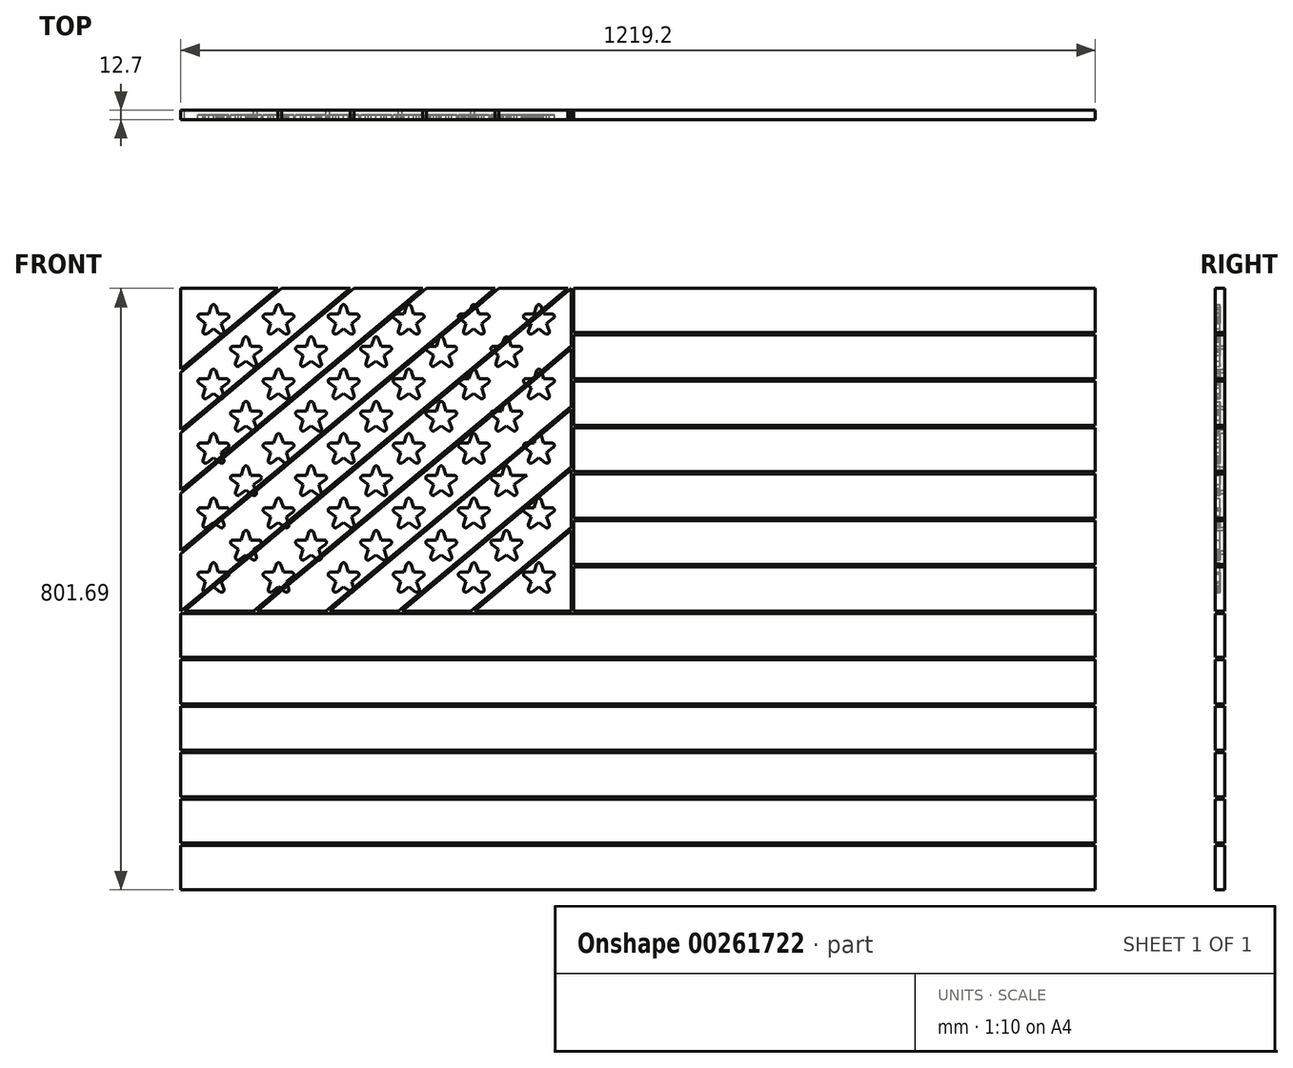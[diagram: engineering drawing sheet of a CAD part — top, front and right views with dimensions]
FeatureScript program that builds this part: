
annotation { "Feature Type Name" : "Feature", "Feature Type Description" : "" }
export const myFeature = defineFeature(function(context is Context, id is Id, definition is map)
    precondition{}
    {
        {
            var Q0;
            Q0=qCreatedBy(makeId("Front.planeOp"),FACE);
            var sketch = newSketch(context, id + "F0", { "sketchPlane" : qUnion([Q0])});
            skLineSegment(sketch, "E0.bottom", {"start": v(0, 0) * mm, "end": v(1219.2, 0) * mm});
            skLineSegment(sketch, "E0.top", {"start": v(0, 58.74) * mm, "end": v(1219.2, 58.74) * mm});
            skLineSegment(sketch, "E0.left", {"start": v(0, 0) * mm, "end": v(0, 58.74) * mm});
            skLineSegment(sketch, "E0.right", {"start": v(1219.2, 0) * mm, "end": v(1219.2, 58.74) * mm});
            skLineSegment(sketch, "E1.0.1.0", {"start": v(0, 120.65) * mm, "end": v(1219.2, 120.65) * mm});
            skLineSegment(sketch, "E1.0.1.1", {"start": v(0, 61.91) * mm, "end": v(1219.2, 61.91) * mm});
            skLineSegment(sketch, "E1.0.1.2", {"start": v(0, 61.91) * mm, "end": v(0, 120.65) * mm});
            skLineSegment(sketch, "E1.0.1.3", {"start": v(1219.2, 61.91) * mm, "end": v(1219.2, 120.65) * mm});
            skLineSegment(sketch, "E1.0.2.0", {"start": v(0, 182.56) * mm, "end": v(1219.2, 182.56) * mm});
            skLineSegment(sketch, "E1.0.2.1", {"start": v(0, 123.82) * mm, "end": v(1219.2, 123.82) * mm});
            skLineSegment(sketch, "E1.0.2.2", {"start": v(0, 123.82) * mm, "end": v(0, 182.56) * mm});
            skLineSegment(sketch, "E1.0.2.3", {"start": v(1219.2, 123.82) * mm, "end": v(1219.2, 182.56) * mm});
            skLineSegment(sketch, "E1.0.3.0", {"start": v(0, 244.47) * mm, "end": v(1219.2, 244.47) * mm});
            skLineSegment(sketch, "E1.0.3.1", {"start": v(0, 185.74) * mm, "end": v(1219.2, 185.74) * mm});
            skLineSegment(sketch, "E1.0.3.2", {"start": v(0, 185.74) * mm, "end": v(0, 244.47) * mm});
            skLineSegment(sketch, "E1.0.3.3", {"start": v(1219.2, 185.74) * mm, "end": v(1219.2, 244.47) * mm});
            skLineSegment(sketch, "E1.0.4.0", {"start": v(0, 306.39) * mm, "end": v(1219.2, 306.39) * mm});
            skLineSegment(sketch, "E1.0.4.1", {"start": v(0, 247.65) * mm, "end": v(1219.2, 247.65) * mm});
            skLineSegment(sketch, "E1.0.4.2", {"start": v(0, 247.65) * mm, "end": v(0, 306.39) * mm});
            skLineSegment(sketch, "E1.0.4.3", {"start": v(1219.2, 247.65) * mm, "end": v(1219.2, 306.39) * mm});
            skLineSegment(sketch, "E1.0.5.0", {"start": v(0, 368.3) * mm, "end": v(1219.2, 368.3) * mm});
            skLineSegment(sketch, "E1.0.5.1", {"start": v(0, 309.56) * mm, "end": v(1219.2, 309.56) * mm});
            skLineSegment(sketch, "E1.0.5.2", {"start": v(0, 309.56) * mm, "end": v(0, 368.3) * mm});
            skLineSegment(sketch, "E1.0.5.3", {"start": v(1219.2, 309.56) * mm, "end": v(1219.2, 368.3) * mm});
            skLineSegment(sketch, "E1.direction1", {"start": v(0, 0) * mm, "end": v(1219.2, 0) * mm, "construction": true});
            skLineSegment(sketch, "E1.direction2", {"start": v(0, 0) * mm, "end": v(0, 61.91) * mm, "construction": true});
            skLineSegment(sketch, "E2.bottom", {"start": v(523.88, 371.48) * mm, "end": v(1219.2, 371.48) * mm});
            skLineSegment(sketch, "E2.top", {"start": v(523.88, 430.21) * mm, "end": v(1219.2, 430.21) * mm});
            skLineSegment(sketch, "E2.left", {"start": v(523.88, 371.48) * mm, "end": v(523.88, 430.21) * mm});
            skLineSegment(sketch, "E2.right", {"start": v(1219.2, 371.48) * mm, "end": v(1219.2, 430.21) * mm});
            skLineSegment(sketch, "E3.0.1.0", {"start": v(523.88, 492.12) * mm, "end": v(1219.2, 492.12) * mm});
            skLineSegment(sketch, "E3.0.1.1", {"start": v(1219.2, 433.39) * mm, "end": v(1219.2, 492.12) * mm});
            skLineSegment(sketch, "E3.0.1.2", {"start": v(523.88, 433.39) * mm, "end": v(523.88, 492.12) * mm});
            skLineSegment(sketch, "E3.0.1.3", {"start": v(523.88, 433.39) * mm, "end": v(1219.2, 433.39) * mm});
            skLineSegment(sketch, "E3.0.2.0", {"start": v(523.88, 554.04) * mm, "end": v(1219.2, 554.04) * mm});
            skLineSegment(sketch, "E3.0.2.1", {"start": v(1219.2, 495.3) * mm, "end": v(1219.2, 554.04) * mm});
            skLineSegment(sketch, "E3.0.2.2", {"start": v(523.88, 495.3) * mm, "end": v(523.88, 554.04) * mm});
            skLineSegment(sketch, "E3.0.2.3", {"start": v(523.88, 495.3) * mm, "end": v(1219.2, 495.3) * mm});
            skLineSegment(sketch, "E3.0.3.0", {"start": v(523.88, 615.95) * mm, "end": v(1219.2, 615.95) * mm});
            skLineSegment(sketch, "E3.0.3.1", {"start": v(1219.2, 557.21) * mm, "end": v(1219.2, 615.95) * mm});
            skLineSegment(sketch, "E3.0.3.2", {"start": v(523.88, 557.21) * mm, "end": v(523.88, 615.95) * mm});
            skLineSegment(sketch, "E3.0.3.3", {"start": v(523.88, 557.21) * mm, "end": v(1219.2, 557.21) * mm});
            skLineSegment(sketch, "E3.0.4.0", {"start": v(523.88, 677.86) * mm, "end": v(1219.2, 677.86) * mm});
            skLineSegment(sketch, "E3.0.4.1", {"start": v(1219.2, 619.12) * mm, "end": v(1219.2, 677.86) * mm});
            skLineSegment(sketch, "E3.0.4.2", {"start": v(523.88, 619.12) * mm, "end": v(523.88, 677.86) * mm});
            skLineSegment(sketch, "E3.0.4.3", {"start": v(523.88, 619.12) * mm, "end": v(1219.2, 619.12) * mm});
            skLineSegment(sketch, "E3.0.5.0", {"start": v(523.88, 739.77) * mm, "end": v(1219.2, 739.77) * mm});
            skLineSegment(sketch, "E3.0.5.1", {"start": v(1219.2, 681.04) * mm, "end": v(1219.2, 739.77) * mm});
            skLineSegment(sketch, "E3.0.5.2", {"start": v(523.88, 681.04) * mm, "end": v(523.88, 739.77) * mm});
            skLineSegment(sketch, "E3.0.5.3", {"start": v(523.88, 681.04) * mm, "end": v(1219.2, 681.04) * mm});
            skLineSegment(sketch, "E3.0.6.0", {"start": v(523.88, 801.69) * mm, "end": v(1219.2, 801.69) * mm});
            skLineSegment(sketch, "E3.0.6.1", {"start": v(1219.2, 742.95) * mm, "end": v(1219.2, 801.69) * mm});
            skLineSegment(sketch, "E3.0.6.2", {"start": v(523.88, 742.95) * mm, "end": v(523.88, 801.69) * mm});
            skLineSegment(sketch, "E3.0.6.3", {"start": v(523.88, 742.95) * mm, "end": v(1219.2, 742.95) * mm});
            skLineSegment(sketch, "E3.direction1", {"start": v(523.88, 371.48) * mm, "end": v(1219.2, 371.48) * mm, "construction": true});
            skLineSegment(sketch, "E3.direction2", {"start": v(523.88, 371.48) * mm, "end": v(523.88, 433.39) * mm, "construction": true});
            skLineSegment(sketch, "E4", {"start": v(520.7, 801.69) * mm, "end": v(4.96, 371.47) * mm});
            skLineSegment(sketch, "E5", {"start": v(520.7, 725.2) * mm, "end": v(96.65, 371.47) * mm});
            skLineSegment(sketch, "E6", {"start": v(520.7, 721.06) * mm, "end": v(101.61, 371.47) * mm});
            skLineSegment(sketch, "E7", {"start": v(193.3, 371.47) * mm, "end": v(520.7, 644.57) * mm});
            skLineSegment(sketch, "E8", {"start": v(520.7, 640.44) * mm, "end": v(198.26, 371.47) * mm});
            skLineSegment(sketch, "E9", {"start": v(520.7, 563.95) * mm, "end": v(289.96, 371.47) * mm});
            skLineSegment(sketch, "E10", {"start": v(520.7, 483.32) * mm, "end": v(386.62, 371.48) * mm});
            skLineSegment(sketch, "E11", {"start": v(520.7, 559.81) * mm, "end": v(294.92, 371.47) * mm});
            skLineSegment(sketch, "E12", {"start": v(520.7, 479.19) * mm, "end": v(391.57, 371.47) * mm});
            skLineSegment(sketch, "E13", {"start": v(520.7, 801.69) * mm, "end": v(520.7, 725.2) * mm});
            skLineSegment(sketch, "E14", {"start": v(520.7, 721.06) * mm, "end": v(520.7, 644.57) * mm});
            skLineSegment(sketch, "E15", {"start": v(520.7, 640.44) * mm, "end": v(520.7, 563.95) * mm});
            skLineSegment(sketch, "E16", {"start": v(520.7, 559.81) * mm, "end": v(520.7, 483.32) * mm});
            skLineSegment(sketch, "E17", {"start": v(520.7, 479.19) * mm, "end": v(520.7, 371.48) * mm});
            skLineSegment(sketch, "E18", {"start": v(4.96, 371.47) * mm, "end": v(96.65, 371.47) * mm});
            skLineSegment(sketch, "E19", {"start": v(193.3, 371.47) * mm, "end": v(101.61, 371.47) * mm});
            skLineSegment(sketch, "E20", {"start": v(198.26, 371.47) * mm, "end": v(289.96, 371.47) * mm});
            skLineSegment(sketch, "E21", {"start": v(294.92, 371.47) * mm, "end": v(386.62, 371.47) * mm});
            skLineSegment(sketch, "E22", {"start": v(391.57, 371.47) * mm, "end": v(520.7, 371.48) * mm});
            skLineSegment(sketch, "E23", {"start": v(515.74, 801.69) * mm, "end": v(0, 371.47) * mm});
            skLineSegment(sketch, "E24", {"start": v(424.05, 801.69) * mm, "end": v(0, 447.97) * mm});
            skLineSegment(sketch, "E25", {"start": v(0, 452.1) * mm, "end": v(419.09, 801.69) * mm});
            skLineSegment(sketch, "E26", {"start": v(0, 528.59) * mm, "end": v(327.4, 801.69) * mm});
            skLineSegment(sketch, "E27", {"start": v(322.44, 801.69) * mm, "end": v(0, 532.72) * mm});
            skLineSegment(sketch, "E28", {"start": v(0, 609.21) * mm, "end": v(230.74, 801.69) * mm});
            skLineSegment(sketch, "E29", {"start": v(225.78, 801.69) * mm, "end": v(0, 613.35) * mm});
            skLineSegment(sketch, "E30", {"start": v(134.08, 801.69) * mm, "end": v(0, 689.84) * mm});
            skLineSegment(sketch, "E31", {"start": v(129.13, 801.69) * mm, "end": v(0, 693.97) * mm});
            skLineSegment(sketch, "E32", {"start": v(0, 447.97) * mm, "end": v(0, 371.47) * mm});
            skLineSegment(sketch, "E33", {"start": v(0, 528.59) * mm, "end": v(0, 452.1) * mm});
            skLineSegment(sketch, "E34", {"start": v(0, 532.72) * mm, "end": v(0, 609.21) * mm});
            skLineSegment(sketch, "E35", {"start": v(0, 613.35) * mm, "end": v(0, 689.84) * mm});
            skLineSegment(sketch, "E36", {"start": v(0, 693.97) * mm, "end": v(0, 801.69) * mm});
            skLineSegment(sketch, "E37", {"start": v(515.74, 801.69) * mm, "end": v(424.05, 801.69) * mm});
            skLineSegment(sketch, "E38", {"start": v(419.09, 801.69) * mm, "end": v(327.4, 801.69) * mm});
            skLineSegment(sketch, "E39", {"start": v(322.44, 801.69) * mm, "end": v(230.74, 801.69) * mm});
            skLineSegment(sketch, "E40", {"start": v(225.78, 801.69) * mm, "end": v(134.08, 801.69) * mm});
            skLineSegment(sketch, "E41", {"start": v(129.13, 801.69) * mm, "end": v(0, 801.69) * mm});
            skSolve(sketch);
        }
        {
            var Q0;
            Q0=qCreatedBy(makeId("Front.planeOp"),FACE);
            var sketch = newSketch(context, id + "F1", { "sketchPlane" : qUnion([Q0])});
            skLineSegment(sketch, "E42", {"start": v(43.4, 801.69) * mm, "end": v(43.4, 371.47) * mm, "construction": true});
            skLineSegment(sketch, "E43", {"start": v(520.7, 801.69) * mm, "end": v(0, 801.69) * mm, "construction": true});
            skLineSegment(sketch, "E44", {"start": v(0, 801.69) * mm, "end": v(0, 371.47) * mm, "construction": true});
            skLineSegment(sketch, "E45", {"start": v(0, 371.47) * mm, "end": v(520.7, 371.47) * mm, "construction": true});
            skLineSegment(sketch, "E46", {"start": v(520.7, 371.48) * mm, "end": v(520.7, 801.69) * mm, "construction": true});
            skLineSegment(sketch, "E47", {"start": v(0, 414.5) * mm, "end": v(520.7, 414.5) * mm, "construction": true});
            skLineSegment(sketch, "E48.1.0.0", {"start": v(86.78, 801.69) * mm, "end": v(86.78, 371.47) * mm, "construction": true});
            skLineSegment(sketch, "E48.2.0.0", {"start": v(130.17, 801.69) * mm, "end": v(130.17, 371.47) * mm, "construction": true});
            skLineSegment(sketch, "E48.3.0.0", {"start": v(173.56, 801.69) * mm, "end": v(173.56, 371.47) * mm, "construction": true});
            skLineSegment(sketch, "E48.4.0.0", {"start": v(216.95, 801.69) * mm, "end": v(216.95, 371.47) * mm, "construction": true});
            skLineSegment(sketch, "E48.5.0.0", {"start": v(260.34, 801.69) * mm, "end": v(260.34, 371.47) * mm, "construction": true});
            skLineSegment(sketch, "E48.6.0.0", {"start": v(303.74, 801.69) * mm, "end": v(303.74, 371.47) * mm, "construction": true});
            skLineSegment(sketch, "E48.7.0.0", {"start": v(347.13, 801.69) * mm, "end": v(347.13, 371.47) * mm, "construction": true});
            skLineSegment(sketch, "E48.8.0.0", {"start": v(390.52, 801.69) * mm, "end": v(390.52, 371.47) * mm, "construction": true});
            skLineSegment(sketch, "E48.9.0.0", {"start": v(433.9, 801.69) * mm, "end": v(433.9, 371.47) * mm, "construction": true});
            skLineSegment(sketch, "E48.10.0.0", {"start": v(477.3, 801.69) * mm, "end": v(477.3, 371.47) * mm, "construction": true});
            skLineSegment(sketch, "E48.direction1", {"start": v(43.4, 371.47) * mm, "end": v(86.78, 371.47) * mm, "construction": true});
            skLineSegment(sketch, "E49", {"start": v(43.4, 371.47) * mm, "end": v(0, 371.47) * mm, "construction": true});
            skLineSegment(sketch, "E50", {"start": v(0, 414.5) * mm, "end": v(0, 371.47) * mm, "construction": true});
            skLineSegment(sketch, "E51.0.1.0", {"start": v(0, 457.51) * mm, "end": v(520.7, 457.51) * mm, "construction": true});
            skLineSegment(sketch, "E51.0.2.0", {"start": v(0, 500.53) * mm, "end": v(520.7, 500.53) * mm, "construction": true});
            skLineSegment(sketch, "E51.0.3.0", {"start": v(0, 543.55) * mm, "end": v(520.7, 543.55) * mm, "construction": true});
            skLineSegment(sketch, "E51.0.4.0", {"start": v(0, 586.57) * mm, "end": v(520.7, 586.57) * mm, "construction": true});
            skLineSegment(sketch, "E51.0.5.0", {"start": v(0, 629.6) * mm, "end": v(520.7, 629.6) * mm, "construction": true});
            skLineSegment(sketch, "E51.0.6.0", {"start": v(0, 672.61) * mm, "end": v(520.7, 672.61) * mm, "construction": true});
            skLineSegment(sketch, "E51.0.7.0", {"start": v(0, 715.63) * mm, "end": v(520.7, 715.63) * mm, "construction": true});
            skLineSegment(sketch, "E51.0.8.0", {"start": v(0, 758.65) * mm, "end": v(520.7, 758.65) * mm, "construction": true});
            skLineSegment(sketch, "E51.direction2", {"start": v(0, 414.5) * mm, "end": v(0, 457.51) * mm, "construction": true});
            skPoint(sketch, "E52", {"position": v(43.4, 758.65) * mm});
            skPoint(sketch, "E53", {"position": v(130.17, 758.65) * mm});
            skPoint(sketch, "E54", {"position": v(216.95, 758.65) * mm});
            skPoint(sketch, "E55", {"position": v(303.74, 758.65) * mm});
            skPoint(sketch, "E56", {"position": v(390.52, 758.65) * mm});
            skPoint(sketch, "E57", {"position": v(477.3, 758.65) * mm});
            skPoint(sketch, "E58", {"position": v(86.78, 715.63) * mm});
            skPoint(sketch, "E59", {"position": v(173.56, 715.63) * mm});
            skPoint(sketch, "E60", {"position": v(260.34, 715.63) * mm});
            skPoint(sketch, "E61", {"position": v(347.13, 715.63) * mm});
            skPoint(sketch, "E62", {"position": v(433.9, 715.63) * mm});
            skPoint(sketch, "E63", {"position": v(477.3, 672.61) * mm});
            skPoint(sketch, "E64", {"position": v(390.52, 672.61) * mm});
            skPoint(sketch, "E65", {"position": v(303.74, 672.61) * mm});
            skPoint(sketch, "E66", {"position": v(216.95, 672.61) * mm});
            skPoint(sketch, "E67", {"position": v(130.17, 672.61) * mm});
            skPoint(sketch, "E68", {"position": v(43.4, 672.61) * mm});
            skPoint(sketch, "E69", {"position": v(86.78, 629.6) * mm});
            skPoint(sketch, "E70", {"position": v(173.56, 629.6) * mm});
            skPoint(sketch, "E71", {"position": v(260.34, 629.6) * mm});
            skPoint(sketch, "E72", {"position": v(347.13, 629.6) * mm});
            skPoint(sketch, "E73", {"position": v(433.9, 629.6) * mm});
            skPoint(sketch, "E74", {"position": v(130.17, 586.57) * mm});
            skPoint(sketch, "E75", {"position": v(216.95, 586.57) * mm});
            skPoint(sketch, "E76", {"position": v(303.74, 586.57) * mm});
            skPoint(sketch, "E77", {"position": v(390.52, 586.57) * mm});
            skPoint(sketch, "E78", {"position": v(433.9, 543.55) * mm});
            skPoint(sketch, "E79", {"position": v(260.34, 543.55) * mm});
            skPoint(sketch, "E80", {"position": v(173.56, 543.55) * mm});
            skPoint(sketch, "E81", {"position": v(130.17, 500.53) * mm});
            skPoint(sketch, "E82", {"position": v(216.95, 500.53) * mm});
            skPoint(sketch, "E83", {"position": v(390.52, 500.53) * mm});
            skPoint(sketch, "E84", {"position": v(477.3, 500.53) * mm});
            skPoint(sketch, "E85", {"position": v(433.9, 457.51) * mm});
            skPoint(sketch, "E86", {"position": v(347.13, 457.51) * mm});
            skPoint(sketch, "E87", {"position": v(173.56, 457.51) * mm});
            skPoint(sketch, "E88", {"position": v(86.78, 457.51) * mm});
            skPoint(sketch, "E89", {"position": v(130.17, 414.5) * mm});
            skPoint(sketch, "E90", {"position": v(216.95, 414.5) * mm});
            skPoint(sketch, "E91", {"position": v(303.74, 414.5) * mm});
            skPoint(sketch, "E92", {"position": v(477.3, 414.5) * mm});
            skCircle(sketch, "E93", {"center": v(0, 845.78) * mm, "radius": 28.58 * mm, "construction": true});
            skLineSegment(sketch, "E94", {"start": v(-27.18, 854.61) * mm, "end": v(-6.42, 854.61) * mm, "construction": true});
            skLineSegment(sketch, "E95", {"start": v(27.18, 854.61) * mm, "end": v(10.38, 842.4) * mm, "construction": true});
            skLineSegment(sketch, "E96", {"start": v(-6.42, 854.61) * mm, "end": v(0, 874.36) * mm, "construction": true});
            skLineSegment(sketch, "E97", {"start": v(0, 874.36) * mm, "end": v(6.42, 854.61) * mm, "construction": true});
            skLineSegment(sketch, "E98", {"start": v(16.8, 822.66) * mm, "end": v(0, 834.87) * mm, "construction": true});
            skLineSegment(sketch, "E99", {"start": v(-16.8, 822.66) * mm, "end": v(0, 834.87) * mm, "construction": true});
            skLineSegment(sketch, "E100", {"start": v(-27.18, 854.61) * mm, "end": v(-10.38, 842.4) * mm, "construction": true});
            skLineSegment(sketch, "E101", {"start": v(-10.38, 842.4) * mm, "end": v(-16.8, 822.66) * mm, "construction": true});
            skLineSegment(sketch, "E102", {"start": v(16.8, 822.66) * mm, "end": v(10.38, 842.4) * mm, "construction": true});
            skLineSegment(sketch, "E103", {"start": v(27.18, 854.61) * mm, "end": v(6.42, 854.61) * mm, "construction": true});
            skCircle(sketch, "E104", {"center": v(43.4, 758.65) * mm, "radius": 28.58 * mm, "construction": true});
            skLineSegment(sketch, "E105", {"start": v(16.21, 767.48) * mm, "end": v(36.98, 767.48) * mm});
            skLineSegment(sketch, "E106", {"start": v(70.57, 767.48) * mm, "end": v(53.77, 755.28) * mm});
            skLineSegment(sketch, "E107", {"start": v(36.98, 767.48) * mm, "end": v(43.4, 787.23) * mm});
            skLineSegment(sketch, "E108", {"start": v(43.4, 787.23) * mm, "end": v(49.8, 767.48) * mm});
            skLineSegment(sketch, "E109", {"start": v(60.19, 735.54) * mm, "end": v(43.4, 747.74) * mm});
            skLineSegment(sketch, "E110", {"start": v(26.6, 735.54) * mm, "end": v(43.4, 747.74) * mm});
            skLineSegment(sketch, "E111", {"start": v(16.21, 767.48) * mm, "end": v(33.01, 755.28) * mm});
            skLineSegment(sketch, "E112", {"start": v(33.01, 755.28) * mm, "end": v(26.6, 735.54) * mm});
            skLineSegment(sketch, "E113", {"start": v(60.19, 735.54) * mm, "end": v(53.77, 755.28) * mm});
            skLineSegment(sketch, "E114", {"start": v(70.57, 767.48) * mm, "end": v(49.8, 767.48) * mm});
            skCircle(sketch, "E115", {"center": v(477.3, 586.57) * mm, "radius": 28.58 * mm, "construction": true});
            skLineSegment(sketch, "E116", {"start": v(450.12, 595.4) * mm, "end": v(470.88, 595.4) * mm});
            skLineSegment(sketch, "E117", {"start": v(504.48, 595.4) * mm, "end": v(487.68, 583.2) * mm});
            skLineSegment(sketch, "E118", {"start": v(470.88, 595.4) * mm, "end": v(477.3, 615.15) * mm});
            skLineSegment(sketch, "E119", {"start": v(477.3, 615.15) * mm, "end": v(483.71, 595.4) * mm});
            skLineSegment(sketch, "E120", {"start": v(494.1, 563.46) * mm, "end": v(477.3, 575.66) * mm});
            skLineSegment(sketch, "E121", {"start": v(460.5, 563.46) * mm, "end": v(477.3, 575.66) * mm});
            skLineSegment(sketch, "E122", {"start": v(450.12, 595.4) * mm, "end": v(466.92, 583.2) * mm});
            skLineSegment(sketch, "E123", {"start": v(466.92, 583.2) * mm, "end": v(460.5, 563.46) * mm});
            skLineSegment(sketch, "E124", {"start": v(494.1, 563.46) * mm, "end": v(487.68, 583.2) * mm});
            skLineSegment(sketch, "E125", {"start": v(504.48, 595.4) * mm, "end": v(483.71, 595.4) * mm});
            skCircle(sketch, "E126", {"center": v(390.52, 758.65) * mm, "radius": 28.58 * mm, "construction": true});
            skLineSegment(sketch, "E127", {"start": v(363.34, 767.48) * mm, "end": v(384.1, 767.48) * mm});
            skLineSegment(sketch, "E128", {"start": v(417.7, 767.48) * mm, "end": v(400.9, 755.28) * mm});
            skLineSegment(sketch, "E129", {"start": v(384.1, 767.48) * mm, "end": v(390.52, 787.23) * mm});
            skLineSegment(sketch, "E130", {"start": v(390.52, 787.23) * mm, "end": v(396.93, 767.48) * mm});
            skLineSegment(sketch, "E131", {"start": v(407.31, 735.54) * mm, "end": v(390.52, 747.74) * mm});
            skLineSegment(sketch, "E132", {"start": v(373.72, 735.54) * mm, "end": v(390.52, 747.74) * mm});
            skLineSegment(sketch, "E133", {"start": v(363.34, 767.48) * mm, "end": v(380.14, 755.28) * mm});
            skLineSegment(sketch, "E134", {"start": v(380.14, 755.28) * mm, "end": v(373.72, 735.54) * mm});
            skLineSegment(sketch, "E135", {"start": v(407.31, 735.54) * mm, "end": v(400.9, 755.28) * mm});
            skLineSegment(sketch, "E136", {"start": v(417.7, 767.48) * mm, "end": v(396.93, 767.48) * mm});
            skCircle(sketch, "E137", {"center": v(303.74, 758.65) * mm, "radius": 28.58 * mm, "construction": true});
            skLineSegment(sketch, "E138", {"start": v(276.56, 767.48) * mm, "end": v(297.32, 767.48) * mm});
            skLineSegment(sketch, "E139", {"start": v(330.91, 767.48) * mm, "end": v(314.12, 755.28) * mm});
            skLineSegment(sketch, "E140", {"start": v(297.32, 767.48) * mm, "end": v(303.74, 787.23) * mm});
            skLineSegment(sketch, "E141", {"start": v(303.74, 787.23) * mm, "end": v(310.15, 767.48) * mm});
            skLineSegment(sketch, "E142", {"start": v(320.53, 735.54) * mm, "end": v(303.74, 747.74) * mm});
            skLineSegment(sketch, "E143", {"start": v(286.94, 735.54) * mm, "end": v(303.74, 747.74) * mm});
            skLineSegment(sketch, "E144", {"start": v(276.56, 767.48) * mm, "end": v(293.36, 755.28) * mm});
            skLineSegment(sketch, "E145", {"start": v(293.36, 755.28) * mm, "end": v(286.94, 735.54) * mm});
            skLineSegment(sketch, "E146", {"start": v(320.53, 735.54) * mm, "end": v(314.12, 755.28) * mm});
            skLineSegment(sketch, "E147", {"start": v(330.91, 767.48) * mm, "end": v(310.15, 767.48) * mm});
            skCircle(sketch, "E148", {"center": v(216.95, 758.65) * mm, "radius": 28.58 * mm, "construction": true});
            skLineSegment(sketch, "E149", {"start": v(189.78, 767.48) * mm, "end": v(210.54, 767.48) * mm});
            skLineSegment(sketch, "E150", {"start": v(244.13, 767.48) * mm, "end": v(227.33, 755.28) * mm});
            skLineSegment(sketch, "E151", {"start": v(210.54, 767.48) * mm, "end": v(216.95, 787.23) * mm});
            skLineSegment(sketch, "E152", {"start": v(216.95, 787.23) * mm, "end": v(223.37, 767.48) * mm});
            skLineSegment(sketch, "E153", {"start": v(233.75, 735.54) * mm, "end": v(216.95, 747.74) * mm});
            skLineSegment(sketch, "E154", {"start": v(200.16, 735.54) * mm, "end": v(216.95, 747.74) * mm});
            skLineSegment(sketch, "E155", {"start": v(189.78, 767.48) * mm, "end": v(206.57, 755.28) * mm});
            skLineSegment(sketch, "E156", {"start": v(206.57, 755.28) * mm, "end": v(200.16, 735.54) * mm});
            skLineSegment(sketch, "E157", {"start": v(233.75, 735.54) * mm, "end": v(227.33, 755.28) * mm});
            skLineSegment(sketch, "E158", {"start": v(244.13, 767.48) * mm, "end": v(223.37, 767.48) * mm});
            skCircle(sketch, "E159", {"center": v(130.17, 758.65) * mm, "radius": 28.58 * mm, "construction": true});
            skLineSegment(sketch, "E160", {"start": v(103, 767.48) * mm, "end": v(123.76, 767.48) * mm});
            skLineSegment(sketch, "E161", {"start": v(157.35, 767.48) * mm, "end": v(140.55, 755.28) * mm});
            skLineSegment(sketch, "E162", {"start": v(123.76, 767.48) * mm, "end": v(130.17, 787.23) * mm});
            skLineSegment(sketch, "E163", {"start": v(130.17, 787.23) * mm, "end": v(136.59, 767.48) * mm});
            skLineSegment(sketch, "E164", {"start": v(146.97, 735.54) * mm, "end": v(130.17, 747.74) * mm});
            skLineSegment(sketch, "E165", {"start": v(113.38, 735.54) * mm, "end": v(130.17, 747.74) * mm});
            skLineSegment(sketch, "E166", {"start": v(103, 767.48) * mm, "end": v(119.8, 755.28) * mm});
            skLineSegment(sketch, "E167", {"start": v(119.8, 755.28) * mm, "end": v(113.38, 735.54) * mm});
            skLineSegment(sketch, "E168", {"start": v(146.97, 735.54) * mm, "end": v(140.55, 755.28) * mm});
            skLineSegment(sketch, "E169", {"start": v(157.35, 767.48) * mm, "end": v(136.59, 767.48) * mm});
            skCircle(sketch, "E170", {"center": v(477.3, 758.65) * mm, "radius": 28.58 * mm, "construction": true});
            skLineSegment(sketch, "E171", {"start": v(450.12, 767.48) * mm, "end": v(470.88, 767.48) * mm});
            skLineSegment(sketch, "E172", {"start": v(504.48, 767.48) * mm, "end": v(487.68, 755.28) * mm});
            skLineSegment(sketch, "E173", {"start": v(470.88, 767.48) * mm, "end": v(477.3, 787.23) * mm});
            skLineSegment(sketch, "E174", {"start": v(477.3, 787.23) * mm, "end": v(483.71, 767.48) * mm});
            skLineSegment(sketch, "E175", {"start": v(494.1, 735.54) * mm, "end": v(477.3, 747.74) * mm});
            skLineSegment(sketch, "E176", {"start": v(460.5, 735.54) * mm, "end": v(477.3, 747.74) * mm});
            skLineSegment(sketch, "E177", {"start": v(450.12, 767.48) * mm, "end": v(466.92, 755.28) * mm});
            skLineSegment(sketch, "E178", {"start": v(466.92, 755.28) * mm, "end": v(460.5, 735.54) * mm});
            skLineSegment(sketch, "E179", {"start": v(494.1, 735.54) * mm, "end": v(487.68, 755.28) * mm});
            skLineSegment(sketch, "E180", {"start": v(504.48, 767.48) * mm, "end": v(483.71, 767.48) * mm});
            skCircle(sketch, "E181", {"center": v(347.13, 715.63) * mm, "radius": 28.58 * mm, "construction": true});
            skLineSegment(sketch, "E182", {"start": v(319.95, 724.47) * mm, "end": v(340.71, 724.47) * mm});
            skLineSegment(sketch, "E183", {"start": v(374.3, 724.47) * mm, "end": v(357.5, 712.26) * mm});
            skLineSegment(sketch, "E184", {"start": v(340.71, 724.47) * mm, "end": v(347.13, 744.2) * mm});
            skLineSegment(sketch, "E185", {"start": v(347.13, 744.2) * mm, "end": v(353.54, 724.47) * mm});
            skLineSegment(sketch, "E186", {"start": v(363.92, 692.52) * mm, "end": v(347.13, 704.72) * mm});
            skLineSegment(sketch, "E187", {"start": v(330.33, 692.52) * mm, "end": v(347.13, 704.72) * mm});
            skLineSegment(sketch, "E188", {"start": v(319.95, 724.47) * mm, "end": v(336.75, 712.26) * mm});
            skLineSegment(sketch, "E189", {"start": v(336.75, 712.26) * mm, "end": v(330.33, 692.52) * mm});
            skLineSegment(sketch, "E190", {"start": v(363.92, 692.52) * mm, "end": v(357.5, 712.26) * mm});
            skLineSegment(sketch, "E191", {"start": v(374.3, 724.47) * mm, "end": v(353.54, 724.47) * mm});
            skCircle(sketch, "E192", {"center": v(260.34, 715.63) * mm, "radius": 28.58 * mm, "construction": true});
            skLineSegment(sketch, "E193", {"start": v(233.17, 724.47) * mm, "end": v(253.93, 724.47) * mm});
            skLineSegment(sketch, "E194", {"start": v(287.52, 724.47) * mm, "end": v(270.73, 712.26) * mm});
            skLineSegment(sketch, "E195", {"start": v(253.93, 724.47) * mm, "end": v(260.34, 744.2) * mm});
            skLineSegment(sketch, "E196", {"start": v(260.34, 744.2) * mm, "end": v(266.76, 724.47) * mm});
            skLineSegment(sketch, "E197", {"start": v(277.14, 692.52) * mm, "end": v(260.34, 704.72) * mm});
            skLineSegment(sketch, "E198", {"start": v(243.55, 692.52) * mm, "end": v(260.34, 704.72) * mm});
            skLineSegment(sketch, "E199", {"start": v(233.17, 724.47) * mm, "end": v(249.96, 712.26) * mm});
            skLineSegment(sketch, "E200", {"start": v(249.96, 712.26) * mm, "end": v(243.55, 692.52) * mm});
            skLineSegment(sketch, "E201", {"start": v(277.14, 692.52) * mm, "end": v(270.73, 712.26) * mm});
            skLineSegment(sketch, "E202", {"start": v(287.52, 724.47) * mm, "end": v(266.76, 724.47) * mm});
            skCircle(sketch, "E203", {"center": v(173.56, 715.63) * mm, "radius": 28.58 * mm, "construction": true});
            skLineSegment(sketch, "E204", {"start": v(146.39, 724.47) * mm, "end": v(167.15, 724.47) * mm});
            skLineSegment(sketch, "E205", {"start": v(200.74, 724.47) * mm, "end": v(183.94, 712.26) * mm});
            skLineSegment(sketch, "E206", {"start": v(167.15, 724.47) * mm, "end": v(173.56, 744.2) * mm});
            skLineSegment(sketch, "E207", {"start": v(173.56, 744.2) * mm, "end": v(179.98, 724.47) * mm});
            skLineSegment(sketch, "E208", {"start": v(190.36, 692.52) * mm, "end": v(173.56, 704.72) * mm});
            skLineSegment(sketch, "E209", {"start": v(156.77, 692.52) * mm, "end": v(173.56, 704.72) * mm});
            skLineSegment(sketch, "E210", {"start": v(146.39, 724.47) * mm, "end": v(163.18, 712.26) * mm});
            skLineSegment(sketch, "E211", {"start": v(163.18, 712.26) * mm, "end": v(156.77, 692.52) * mm});
            skLineSegment(sketch, "E212", {"start": v(190.36, 692.52) * mm, "end": v(183.94, 712.26) * mm});
            skLineSegment(sketch, "E213", {"start": v(200.74, 724.47) * mm, "end": v(179.98, 724.47) * mm});
            skCircle(sketch, "E214", {"center": v(86.78, 715.63) * mm, "radius": 28.58 * mm, "construction": true});
            skLineSegment(sketch, "E215", {"start": v(59.6, 724.47) * mm, "end": v(80.37, 724.47) * mm});
            skLineSegment(sketch, "E216", {"start": v(113.96, 724.47) * mm, "end": v(97.16, 712.26) * mm});
            skLineSegment(sketch, "E217", {"start": v(80.37, 724.47) * mm, "end": v(86.78, 744.2) * mm});
            skLineSegment(sketch, "E218", {"start": v(86.78, 744.2) * mm, "end": v(93.2, 724.47) * mm});
            skLineSegment(sketch, "E219", {"start": v(103.58, 692.52) * mm, "end": v(86.78, 704.72) * mm});
            skLineSegment(sketch, "E220", {"start": v(69.99, 692.52) * mm, "end": v(86.78, 704.72) * mm});
            skLineSegment(sketch, "E221", {"start": v(59.6, 724.47) * mm, "end": v(76.4, 712.26) * mm});
            skLineSegment(sketch, "E222", {"start": v(76.4, 712.26) * mm, "end": v(69.99, 692.52) * mm});
            skLineSegment(sketch, "E223", {"start": v(103.58, 692.52) * mm, "end": v(97.16, 712.26) * mm});
            skLineSegment(sketch, "E224", {"start": v(113.96, 724.47) * mm, "end": v(93.2, 724.47) * mm});
            skCircle(sketch, "E225", {"center": v(433.9, 715.63) * mm, "radius": 28.58 * mm, "construction": true});
            skLineSegment(sketch, "E226", {"start": v(406.73, 724.47) * mm, "end": v(427.5, 724.47) * mm});
            skLineSegment(sketch, "E227", {"start": v(461.08, 724.47) * mm, "end": v(444.29, 712.26) * mm});
            skLineSegment(sketch, "E228", {"start": v(427.5, 724.47) * mm, "end": v(433.9, 744.2) * mm});
            skLineSegment(sketch, "E229", {"start": v(433.9, 744.2) * mm, "end": v(440.32, 724.47) * mm});
            skLineSegment(sketch, "E230", {"start": v(450.7, 692.52) * mm, "end": v(433.9, 704.72) * mm});
            skLineSegment(sketch, "E231", {"start": v(417.11, 692.52) * mm, "end": v(433.9, 704.72) * mm});
            skLineSegment(sketch, "E232", {"start": v(406.73, 724.47) * mm, "end": v(423.53, 712.26) * mm});
            skLineSegment(sketch, "E233", {"start": v(423.53, 712.26) * mm, "end": v(417.11, 692.52) * mm});
            skLineSegment(sketch, "E234", {"start": v(450.7, 692.52) * mm, "end": v(444.29, 712.26) * mm});
            skLineSegment(sketch, "E235", {"start": v(461.08, 724.47) * mm, "end": v(440.32, 724.47) * mm});
            skCircle(sketch, "E236", {"center": v(130.17, 672.61) * mm, "radius": 28.58 * mm, "construction": true});
            skLineSegment(sketch, "E237", {"start": v(103, 681.45) * mm, "end": v(123.76, 681.45) * mm});
            skLineSegment(sketch, "E238", {"start": v(157.35, 681.45) * mm, "end": v(140.55, 669.24) * mm});
            skLineSegment(sketch, "E239", {"start": v(123.76, 681.45) * mm, "end": v(130.17, 701.19) * mm});
            skLineSegment(sketch, "E240", {"start": v(130.17, 701.19) * mm, "end": v(136.59, 681.45) * mm});
            skLineSegment(sketch, "E241", {"start": v(146.97, 649.5) * mm, "end": v(130.17, 661.7) * mm});
            skLineSegment(sketch, "E242", {"start": v(113.38, 649.5) * mm, "end": v(130.17, 661.7) * mm});
            skLineSegment(sketch, "E243", {"start": v(103, 681.45) * mm, "end": v(119.8, 669.24) * mm});
            skLineSegment(sketch, "E244", {"start": v(119.8, 669.24) * mm, "end": v(113.38, 649.5) * mm});
            skLineSegment(sketch, "E245", {"start": v(146.97, 649.5) * mm, "end": v(140.55, 669.24) * mm});
            skLineSegment(sketch, "E246", {"start": v(157.35, 681.45) * mm, "end": v(136.59, 681.45) * mm});
            skPoint(sketch, "E247", {"position": v(43.4, 586.57) * mm});
            skCircle(sketch, "E248", {"center": v(130.17, 586.57) * mm, "radius": 28.58 * mm, "construction": true});
            skLineSegment(sketch, "E249", {"start": v(103, 595.4) * mm, "end": v(123.76, 595.4) * mm});
            skLineSegment(sketch, "E250", {"start": v(157.35, 595.4) * mm, "end": v(140.55, 583.2) * mm});
            skLineSegment(sketch, "E251", {"start": v(123.76, 595.4) * mm, "end": v(130.17, 615.15) * mm});
            skLineSegment(sketch, "E252", {"start": v(130.17, 615.15) * mm, "end": v(136.59, 595.4) * mm});
            skLineSegment(sketch, "E253", {"start": v(146.97, 563.46) * mm, "end": v(130.17, 575.66) * mm});
            skLineSegment(sketch, "E254", {"start": v(113.38, 563.46) * mm, "end": v(130.17, 575.66) * mm});
            skLineSegment(sketch, "E255", {"start": v(103, 595.4) * mm, "end": v(119.8, 583.2) * mm});
            skLineSegment(sketch, "E256", {"start": v(119.8, 583.2) * mm, "end": v(113.38, 563.46) * mm});
            skLineSegment(sketch, "E257", {"start": v(146.97, 563.46) * mm, "end": v(140.55, 583.2) * mm});
            skLineSegment(sketch, "E258", {"start": v(157.35, 595.4) * mm, "end": v(136.59, 595.4) * mm});
            skCircle(sketch, "E259", {"center": v(173.56, 629.6) * mm, "radius": 28.58 * mm, "construction": true});
            skLineSegment(sketch, "E260", {"start": v(146.39, 638.43) * mm, "end": v(167.15, 638.43) * mm});
            skLineSegment(sketch, "E261", {"start": v(200.74, 638.43) * mm, "end": v(183.94, 626.22) * mm});
            skLineSegment(sketch, "E262", {"start": v(167.15, 638.43) * mm, "end": v(173.56, 658.17) * mm});
            skLineSegment(sketch, "E263", {"start": v(173.56, 658.17) * mm, "end": v(179.98, 638.43) * mm});
            skLineSegment(sketch, "E264", {"start": v(190.36, 606.48) * mm, "end": v(173.56, 618.68) * mm});
            skLineSegment(sketch, "E265", {"start": v(156.77, 606.48) * mm, "end": v(173.56, 618.68) * mm});
            skLineSegment(sketch, "E266", {"start": v(146.39, 638.43) * mm, "end": v(163.18, 626.22) * mm});
            skLineSegment(sketch, "E267", {"start": v(163.18, 626.22) * mm, "end": v(156.77, 606.48) * mm});
            skLineSegment(sketch, "E268", {"start": v(190.36, 606.48) * mm, "end": v(183.94, 626.22) * mm});
            skLineSegment(sketch, "E269", {"start": v(200.74, 638.43) * mm, "end": v(179.98, 638.43) * mm});
            skCircle(sketch, "E270", {"center": v(390.52, 672.61) * mm, "radius": 28.58 * mm, "construction": true});
            skLineSegment(sketch, "E271", {"start": v(363.34, 681.45) * mm, "end": v(384.1, 681.45) * mm});
            skLineSegment(sketch, "E272", {"start": v(417.7, 681.45) * mm, "end": v(400.9, 669.24) * mm});
            skLineSegment(sketch, "E273", {"start": v(384.1, 681.45) * mm, "end": v(390.52, 701.19) * mm});
            skLineSegment(sketch, "E274", {"start": v(390.52, 701.19) * mm, "end": v(396.93, 681.45) * mm});
            skLineSegment(sketch, "E275", {"start": v(407.31, 649.5) * mm, "end": v(390.52, 661.7) * mm});
            skLineSegment(sketch, "E276", {"start": v(373.72, 649.5) * mm, "end": v(390.52, 661.7) * mm});
            skLineSegment(sketch, "E277", {"start": v(363.34, 681.45) * mm, "end": v(380.14, 669.24) * mm});
            skLineSegment(sketch, "E278", {"start": v(380.14, 669.24) * mm, "end": v(373.72, 649.5) * mm});
            skLineSegment(sketch, "E279", {"start": v(407.31, 649.5) * mm, "end": v(400.9, 669.24) * mm});
            skLineSegment(sketch, "E280", {"start": v(417.7, 681.45) * mm, "end": v(396.93, 681.45) * mm});
            skCircle(sketch, "E281", {"center": v(347.13, 629.6) * mm, "radius": 28.58 * mm, "construction": true});
            skLineSegment(sketch, "E282", {"start": v(319.95, 638.43) * mm, "end": v(340.71, 638.43) * mm});
            skLineSegment(sketch, "E283", {"start": v(374.3, 638.43) * mm, "end": v(357.5, 626.22) * mm});
            skLineSegment(sketch, "E284", {"start": v(340.71, 638.43) * mm, "end": v(347.13, 658.17) * mm});
            skLineSegment(sketch, "E285", {"start": v(347.13, 658.17) * mm, "end": v(353.54, 638.43) * mm});
            skLineSegment(sketch, "E286", {"start": v(363.92, 606.48) * mm, "end": v(347.13, 618.68) * mm});
            skLineSegment(sketch, "E287", {"start": v(330.33, 606.48) * mm, "end": v(347.13, 618.68) * mm});
            skLineSegment(sketch, "E288", {"start": v(319.95, 638.43) * mm, "end": v(336.75, 626.22) * mm});
            skLineSegment(sketch, "E289", {"start": v(336.75, 626.22) * mm, "end": v(330.33, 606.48) * mm});
            skLineSegment(sketch, "E290", {"start": v(363.92, 606.48) * mm, "end": v(357.5, 626.22) * mm});
            skLineSegment(sketch, "E291", {"start": v(374.3, 638.43) * mm, "end": v(353.54, 638.43) * mm});
            skCircle(sketch, "E292", {"center": v(43.4, 672.61) * mm, "radius": 28.58 * mm, "construction": true});
            skLineSegment(sketch, "E293", {"start": v(16.21, 681.45) * mm, "end": v(36.98, 681.45) * mm});
            skLineSegment(sketch, "E294", {"start": v(70.57, 681.45) * mm, "end": v(53.77, 669.24) * mm});
            skLineSegment(sketch, "E295", {"start": v(36.98, 681.45) * mm, "end": v(43.4, 701.19) * mm});
            skLineSegment(sketch, "E296", {"start": v(43.4, 701.19) * mm, "end": v(49.8, 681.45) * mm});
            skLineSegment(sketch, "E297", {"start": v(60.19, 649.5) * mm, "end": v(43.4, 661.7) * mm});
            skLineSegment(sketch, "E298", {"start": v(26.6, 649.5) * mm, "end": v(43.4, 661.7) * mm});
            skLineSegment(sketch, "E299", {"start": v(16.21, 681.45) * mm, "end": v(33.01, 669.24) * mm});
            skLineSegment(sketch, "E300", {"start": v(33.01, 669.24) * mm, "end": v(26.6, 649.5) * mm});
            skLineSegment(sketch, "E301", {"start": v(60.19, 649.5) * mm, "end": v(53.77, 669.24) * mm});
            skLineSegment(sketch, "E302", {"start": v(70.57, 681.45) * mm, "end": v(49.8, 681.45) * mm});
            skCircle(sketch, "E303", {"center": v(260.34, 629.6) * mm, "radius": 28.58 * mm, "construction": true});
            skLineSegment(sketch, "E304", {"start": v(233.17, 638.43) * mm, "end": v(253.93, 638.43) * mm});
            skLineSegment(sketch, "E305", {"start": v(287.52, 638.43) * mm, "end": v(270.73, 626.22) * mm});
            skLineSegment(sketch, "E306", {"start": v(253.93, 638.43) * mm, "end": v(260.34, 658.17) * mm});
            skLineSegment(sketch, "E307", {"start": v(260.34, 658.17) * mm, "end": v(266.76, 638.43) * mm});
            skLineSegment(sketch, "E308", {"start": v(277.14, 606.48) * mm, "end": v(260.34, 618.68) * mm});
            skLineSegment(sketch, "E309", {"start": v(243.55, 606.48) * mm, "end": v(260.34, 618.68) * mm});
            skLineSegment(sketch, "E310", {"start": v(233.17, 638.43) * mm, "end": v(249.96, 626.22) * mm});
            skLineSegment(sketch, "E311", {"start": v(249.96, 626.22) * mm, "end": v(243.55, 606.48) * mm});
            skLineSegment(sketch, "E312", {"start": v(277.14, 606.48) * mm, "end": v(270.73, 626.22) * mm});
            skLineSegment(sketch, "E313", {"start": v(287.52, 638.43) * mm, "end": v(266.76, 638.43) * mm});
            skCircle(sketch, "E314", {"center": v(433.9, 629.6) * mm, "radius": 28.58 * mm, "construction": true});
            skLineSegment(sketch, "E315", {"start": v(406.73, 638.43) * mm, "end": v(427.5, 638.43) * mm});
            skLineSegment(sketch, "E316", {"start": v(461.08, 638.43) * mm, "end": v(444.29, 626.22) * mm});
            skLineSegment(sketch, "E317", {"start": v(427.5, 638.43) * mm, "end": v(433.9, 658.17) * mm});
            skLineSegment(sketch, "E318", {"start": v(433.9, 658.17) * mm, "end": v(440.32, 638.43) * mm});
            skLineSegment(sketch, "E319", {"start": v(450.7, 606.48) * mm, "end": v(433.9, 618.68) * mm});
            skLineSegment(sketch, "E320", {"start": v(417.11, 606.48) * mm, "end": v(433.9, 618.68) * mm});
            skLineSegment(sketch, "E321", {"start": v(406.73, 638.43) * mm, "end": v(423.53, 626.22) * mm});
            skLineSegment(sketch, "E322", {"start": v(423.53, 626.22) * mm, "end": v(417.11, 606.48) * mm});
            skLineSegment(sketch, "E323", {"start": v(450.7, 606.48) * mm, "end": v(444.29, 626.22) * mm});
            skLineSegment(sketch, "E324", {"start": v(461.08, 638.43) * mm, "end": v(440.32, 638.43) * mm});
            skCircle(sketch, "E325", {"center": v(43.4, 586.57) * mm, "radius": 28.58 * mm, "construction": true});
            skLineSegment(sketch, "E326", {"start": v(16.21, 595.4) * mm, "end": v(36.98, 595.4) * mm});
            skLineSegment(sketch, "E327", {"start": v(70.57, 595.4) * mm, "end": v(53.77, 583.2) * mm});
            skLineSegment(sketch, "E328", {"start": v(36.98, 595.4) * mm, "end": v(43.4, 615.15) * mm});
            skLineSegment(sketch, "E329", {"start": v(43.4, 615.15) * mm, "end": v(49.8, 595.4) * mm});
            skLineSegment(sketch, "E330", {"start": v(60.19, 563.46) * mm, "end": v(43.4, 575.66) * mm});
            skLineSegment(sketch, "E331", {"start": v(26.6, 563.46) * mm, "end": v(43.4, 575.66) * mm});
            skLineSegment(sketch, "E332", {"start": v(16.21, 595.4) * mm, "end": v(33.01, 583.2) * mm});
            skLineSegment(sketch, "E333", {"start": v(33.01, 583.2) * mm, "end": v(26.6, 563.46) * mm});
            skLineSegment(sketch, "E334", {"start": v(60.19, 563.46) * mm, "end": v(53.77, 583.2) * mm});
            skLineSegment(sketch, "E335", {"start": v(70.57, 595.4) * mm, "end": v(49.8, 595.4) * mm});
            skCircle(sketch, "E336", {"center": v(86.78, 629.6) * mm, "radius": 28.58 * mm, "construction": true});
            skLineSegment(sketch, "E337", {"start": v(59.6, 638.43) * mm, "end": v(80.37, 638.43) * mm});
            skLineSegment(sketch, "E338", {"start": v(113.96, 638.43) * mm, "end": v(97.16, 626.22) * mm});
            skLineSegment(sketch, "E339", {"start": v(80.37, 638.43) * mm, "end": v(86.78, 658.17) * mm});
            skLineSegment(sketch, "E340", {"start": v(86.78, 658.17) * mm, "end": v(93.2, 638.43) * mm});
            skLineSegment(sketch, "E341", {"start": v(103.58, 606.48) * mm, "end": v(86.78, 618.68) * mm});
            skLineSegment(sketch, "E342", {"start": v(69.99, 606.48) * mm, "end": v(86.78, 618.68) * mm});
            skLineSegment(sketch, "E343", {"start": v(59.6, 638.43) * mm, "end": v(76.4, 626.22) * mm});
            skLineSegment(sketch, "E344", {"start": v(76.4, 626.22) * mm, "end": v(69.99, 606.48) * mm});
            skLineSegment(sketch, "E345", {"start": v(103.58, 606.48) * mm, "end": v(97.16, 626.22) * mm});
            skLineSegment(sketch, "E346", {"start": v(113.96, 638.43) * mm, "end": v(93.2, 638.43) * mm});
            skCircle(sketch, "E347", {"center": v(390.52, 586.57) * mm, "radius": 28.58 * mm, "construction": true});
            skLineSegment(sketch, "E348", {"start": v(363.34, 595.4) * mm, "end": v(384.1, 595.4) * mm});
            skLineSegment(sketch, "E349", {"start": v(417.7, 595.4) * mm, "end": v(400.9, 583.2) * mm});
            skLineSegment(sketch, "E350", {"start": v(384.1, 595.4) * mm, "end": v(390.52, 615.15) * mm});
            skLineSegment(sketch, "E351", {"start": v(390.52, 615.15) * mm, "end": v(396.93, 595.4) * mm});
            skLineSegment(sketch, "E352", {"start": v(407.31, 563.46) * mm, "end": v(390.52, 575.66) * mm});
            skLineSegment(sketch, "E353", {"start": v(373.72, 563.46) * mm, "end": v(390.52, 575.66) * mm});
            skLineSegment(sketch, "E354", {"start": v(363.34, 595.4) * mm, "end": v(380.14, 583.2) * mm});
            skLineSegment(sketch, "E355", {"start": v(380.14, 583.2) * mm, "end": v(373.72, 563.46) * mm});
            skLineSegment(sketch, "E356", {"start": v(407.31, 563.46) * mm, "end": v(400.9, 583.2) * mm});
            skLineSegment(sketch, "E357", {"start": v(417.7, 595.4) * mm, "end": v(396.93, 595.4) * mm});
            skCircle(sketch, "E358", {"center": v(303.74, 672.61) * mm, "radius": 28.58 * mm, "construction": true});
            skLineSegment(sketch, "E359", {"start": v(276.56, 681.45) * mm, "end": v(297.32, 681.45) * mm});
            skLineSegment(sketch, "E360", {"start": v(330.91, 681.45) * mm, "end": v(314.12, 669.24) * mm});
            skLineSegment(sketch, "E361", {"start": v(297.32, 681.45) * mm, "end": v(303.74, 701.19) * mm});
            skLineSegment(sketch, "E362", {"start": v(303.74, 701.19) * mm, "end": v(310.15, 681.45) * mm});
            skLineSegment(sketch, "E363", {"start": v(320.53, 649.5) * mm, "end": v(303.74, 661.7) * mm});
            skLineSegment(sketch, "E364", {"start": v(286.94, 649.5) * mm, "end": v(303.74, 661.7) * mm});
            skLineSegment(sketch, "E365", {"start": v(276.56, 681.45) * mm, "end": v(293.36, 669.24) * mm});
            skLineSegment(sketch, "E366", {"start": v(293.36, 669.24) * mm, "end": v(286.94, 649.5) * mm});
            skLineSegment(sketch, "E367", {"start": v(320.53, 649.5) * mm, "end": v(314.12, 669.24) * mm});
            skLineSegment(sketch, "E368", {"start": v(330.91, 681.45) * mm, "end": v(310.15, 681.45) * mm});
            skCircle(sketch, "E369", {"center": v(477.3, 672.61) * mm, "radius": 28.58 * mm, "construction": true});
            skLineSegment(sketch, "E370", {"start": v(450.12, 681.45) * mm, "end": v(470.88, 681.45) * mm});
            skLineSegment(sketch, "E371", {"start": v(504.48, 681.45) * mm, "end": v(487.68, 669.24) * mm});
            skLineSegment(sketch, "E372", {"start": v(470.88, 681.45) * mm, "end": v(477.3, 701.19) * mm});
            skLineSegment(sketch, "E373", {"start": v(477.3, 701.19) * mm, "end": v(483.71, 681.45) * mm});
            skLineSegment(sketch, "E374", {"start": v(494.1, 649.5) * mm, "end": v(477.3, 661.7) * mm});
            skLineSegment(sketch, "E375", {"start": v(460.5, 649.5) * mm, "end": v(477.3, 661.7) * mm});
            skLineSegment(sketch, "E376", {"start": v(450.12, 681.45) * mm, "end": v(466.92, 669.24) * mm});
            skLineSegment(sketch, "E377", {"start": v(466.92, 669.24) * mm, "end": v(460.5, 649.5) * mm});
            skLineSegment(sketch, "E378", {"start": v(494.1, 649.5) * mm, "end": v(487.68, 669.24) * mm});
            skLineSegment(sketch, "E379", {"start": v(504.48, 681.45) * mm, "end": v(483.71, 681.45) * mm});
            skCircle(sketch, "E380", {"center": v(216.95, 586.57) * mm, "radius": 28.58 * mm, "construction": true});
            skLineSegment(sketch, "E381", {"start": v(189.78, 595.4) * mm, "end": v(210.54, 595.4) * mm});
            skLineSegment(sketch, "E382", {"start": v(244.13, 595.4) * mm, "end": v(227.33, 583.2) * mm});
            skLineSegment(sketch, "E383", {"start": v(210.54, 595.4) * mm, "end": v(216.95, 615.15) * mm});
            skLineSegment(sketch, "E384", {"start": v(216.95, 615.15) * mm, "end": v(223.37, 595.4) * mm});
            skLineSegment(sketch, "E385", {"start": v(233.75, 563.46) * mm, "end": v(216.95, 575.66) * mm});
            skLineSegment(sketch, "E386", {"start": v(200.16, 563.46) * mm, "end": v(216.95, 575.66) * mm});
            skLineSegment(sketch, "E387", {"start": v(189.78, 595.4) * mm, "end": v(206.57, 583.2) * mm});
            skLineSegment(sketch, "E388", {"start": v(206.57, 583.2) * mm, "end": v(200.16, 563.46) * mm});
            skLineSegment(sketch, "E389", {"start": v(233.75, 563.46) * mm, "end": v(227.33, 583.2) * mm});
            skLineSegment(sketch, "E390", {"start": v(244.13, 595.4) * mm, "end": v(223.37, 595.4) * mm});
            skCircle(sketch, "E391", {"center": v(303.74, 586.57) * mm, "radius": 28.58 * mm, "construction": true});
            skLineSegment(sketch, "E392", {"start": v(276.56, 595.4) * mm, "end": v(297.32, 595.4) * mm});
            skLineSegment(sketch, "E393", {"start": v(330.91, 595.4) * mm, "end": v(314.12, 583.2) * mm});
            skLineSegment(sketch, "E394", {"start": v(297.32, 595.4) * mm, "end": v(303.74, 615.15) * mm});
            skLineSegment(sketch, "E395", {"start": v(303.74, 615.15) * mm, "end": v(310.15, 595.4) * mm});
            skLineSegment(sketch, "E396", {"start": v(320.53, 563.46) * mm, "end": v(303.74, 575.66) * mm});
            skLineSegment(sketch, "E397", {"start": v(286.94, 563.46) * mm, "end": v(303.74, 575.66) * mm});
            skLineSegment(sketch, "E398", {"start": v(276.56, 595.4) * mm, "end": v(293.36, 583.2) * mm});
            skLineSegment(sketch, "E399", {"start": v(293.36, 583.2) * mm, "end": v(286.94, 563.46) * mm});
            skLineSegment(sketch, "E400", {"start": v(320.53, 563.46) * mm, "end": v(314.12, 583.2) * mm});
            skLineSegment(sketch, "E401", {"start": v(330.91, 595.4) * mm, "end": v(310.15, 595.4) * mm});
            skCircle(sketch, "E402", {"center": v(216.95, 672.61) * mm, "radius": 28.58 * mm, "construction": true});
            skLineSegment(sketch, "E403", {"start": v(189.78, 681.45) * mm, "end": v(210.54, 681.45) * mm});
            skLineSegment(sketch, "E404", {"start": v(244.13, 681.45) * mm, "end": v(227.33, 669.24) * mm});
            skLineSegment(sketch, "E405", {"start": v(210.54, 681.45) * mm, "end": v(216.95, 701.19) * mm});
            skLineSegment(sketch, "E406", {"start": v(216.95, 701.19) * mm, "end": v(223.37, 681.45) * mm});
            skLineSegment(sketch, "E407", {"start": v(233.75, 649.5) * mm, "end": v(216.95, 661.7) * mm});
            skLineSegment(sketch, "E408", {"start": v(200.16, 649.5) * mm, "end": v(216.95, 661.7) * mm});
            skLineSegment(sketch, "E409", {"start": v(189.78, 681.45) * mm, "end": v(206.57, 669.24) * mm});
            skLineSegment(sketch, "E410", {"start": v(206.57, 669.24) * mm, "end": v(200.16, 649.5) * mm});
            skLineSegment(sketch, "E411", {"start": v(233.75, 649.5) * mm, "end": v(227.33, 669.24) * mm});
            skLineSegment(sketch, "E412", {"start": v(244.13, 681.45) * mm, "end": v(223.37, 681.45) * mm});
            skPoint(sketch, "E413", {"position": v(86.78, 543.55) * mm});
            skCircle(sketch, "E414", {"center": v(477.3, 500.53) * mm, "radius": 28.58 * mm, "construction": true});
            skLineSegment(sketch, "E415", {"start": v(450.12, 509.37) * mm, "end": v(470.88, 509.37) * mm});
            skLineSegment(sketch, "E416", {"start": v(504.48, 509.37) * mm, "end": v(487.68, 497.16) * mm});
            skLineSegment(sketch, "E417", {"start": v(470.88, 509.37) * mm, "end": v(477.3, 529.1) * mm});
            skLineSegment(sketch, "E418", {"start": v(477.3, 529.1) * mm, "end": v(483.71, 509.37) * mm});
            skLineSegment(sketch, "E419", {"start": v(494.1, 477.42) * mm, "end": v(477.3, 489.62) * mm});
            skLineSegment(sketch, "E420", {"start": v(460.5, 477.42) * mm, "end": v(477.3, 489.62) * mm});
            skLineSegment(sketch, "E421", {"start": v(450.12, 509.37) * mm, "end": v(466.92, 497.16) * mm});
            skLineSegment(sketch, "E422", {"start": v(466.92, 497.16) * mm, "end": v(460.5, 477.42) * mm});
            skLineSegment(sketch, "E423", {"start": v(494.1, 477.42) * mm, "end": v(487.68, 497.16) * mm});
            skLineSegment(sketch, "E424", {"start": v(504.48, 509.37) * mm, "end": v(483.71, 509.37) * mm});
            skCircle(sketch, "E425", {"center": v(433.9, 543.55) * mm, "radius": 28.58 * mm, "construction": true});
            skLineSegment(sketch, "E426", {"start": v(406.73, 552.39) * mm, "end": v(427.5, 552.39) * mm});
            skLineSegment(sketch, "E427", {"start": v(461.08, 552.39) * mm, "end": v(444.29, 540.18) * mm});
            skLineSegment(sketch, "E428", {"start": v(427.5, 552.39) * mm, "end": v(433.9, 572.13) * mm});
            skLineSegment(sketch, "E429", {"start": v(433.9, 572.13) * mm, "end": v(440.32, 552.39) * mm});
            skLineSegment(sketch, "E430", {"start": v(450.7, 520.44) * mm, "end": v(433.9, 532.64) * mm});
            skLineSegment(sketch, "E431", {"start": v(417.11, 520.44) * mm, "end": v(433.9, 532.64) * mm});
            skLineSegment(sketch, "E432", {"start": v(406.73, 552.39) * mm, "end": v(423.53, 540.18) * mm});
            skLineSegment(sketch, "E433", {"start": v(423.53, 540.18) * mm, "end": v(417.11, 520.44) * mm});
            skLineSegment(sketch, "E434", {"start": v(450.7, 520.44) * mm, "end": v(444.29, 540.18) * mm});
            skLineSegment(sketch, "E435", {"start": v(461.08, 552.39) * mm, "end": v(440.32, 552.39) * mm});
            skCircle(sketch, "E436", {"center": v(477.3, 414.5) * mm, "radius": 28.58 * mm, "construction": true});
            skLineSegment(sketch, "E437", {"start": v(450.12, 423.33) * mm, "end": v(470.88, 423.33) * mm});
            skLineSegment(sketch, "E438", {"start": v(504.48, 423.33) * mm, "end": v(487.68, 411.12) * mm});
            skLineSegment(sketch, "E439", {"start": v(470.88, 423.33) * mm, "end": v(477.3, 443.07) * mm});
            skLineSegment(sketch, "E440", {"start": v(477.3, 443.07) * mm, "end": v(483.71, 423.33) * mm});
            skLineSegment(sketch, "E441", {"start": v(494.1, 391.38) * mm, "end": v(477.3, 403.58) * mm});
            skLineSegment(sketch, "E442", {"start": v(460.5, 391.38) * mm, "end": v(477.3, 403.58) * mm});
            skLineSegment(sketch, "E443", {"start": v(450.12, 423.33) * mm, "end": v(466.92, 411.12) * mm});
            skLineSegment(sketch, "E444", {"start": v(466.92, 411.12) * mm, "end": v(460.5, 391.38) * mm});
            skLineSegment(sketch, "E445", {"start": v(494.1, 391.38) * mm, "end": v(487.68, 411.12) * mm});
            skLineSegment(sketch, "E446", {"start": v(504.48, 423.33) * mm, "end": v(483.71, 423.33) * mm});
            skCircle(sketch, "E447", {"center": v(433.9, 457.51) * mm, "radius": 28.58 * mm, "construction": true});
            skLineSegment(sketch, "E448", {"start": v(406.73, 466.35) * mm, "end": v(427.5, 466.35) * mm});
            skLineSegment(sketch, "E449", {"start": v(461.08, 466.35) * mm, "end": v(444.29, 454.14) * mm});
            skLineSegment(sketch, "E450", {"start": v(427.5, 466.35) * mm, "end": v(433.9, 486.09) * mm});
            skLineSegment(sketch, "E451", {"start": v(433.9, 486.09) * mm, "end": v(440.32, 466.35) * mm});
            skLineSegment(sketch, "E452", {"start": v(450.7, 434.4) * mm, "end": v(433.9, 446.6) * mm});
            skLineSegment(sketch, "E453", {"start": v(417.11, 434.4) * mm, "end": v(433.9, 446.6) * mm});
            skLineSegment(sketch, "E454", {"start": v(406.73, 466.35) * mm, "end": v(423.53, 454.14) * mm});
            skLineSegment(sketch, "E455", {"start": v(423.53, 454.14) * mm, "end": v(417.11, 434.4) * mm});
            skLineSegment(sketch, "E456", {"start": v(450.7, 434.4) * mm, "end": v(444.29, 454.14) * mm});
            skLineSegment(sketch, "E457", {"start": v(461.08, 466.35) * mm, "end": v(440.32, 466.35) * mm});
            skCircle(sketch, "E458", {"center": v(260.34, 543.55) * mm, "radius": 28.58 * mm, "construction": true});
            skLineSegment(sketch, "E459", {"start": v(233.17, 552.39) * mm, "end": v(253.93, 552.39) * mm});
            skLineSegment(sketch, "E460", {"start": v(287.52, 552.39) * mm, "end": v(270.73, 540.18) * mm});
            skLineSegment(sketch, "E461", {"start": v(253.93, 552.39) * mm, "end": v(260.34, 572.13) * mm});
            skLineSegment(sketch, "E462", {"start": v(260.34, 572.13) * mm, "end": v(266.76, 552.39) * mm});
            skLineSegment(sketch, "E463", {"start": v(277.14, 520.44) * mm, "end": v(260.34, 532.64) * mm});
            skLineSegment(sketch, "E464", {"start": v(243.55, 520.44) * mm, "end": v(260.34, 532.64) * mm});
            skLineSegment(sketch, "E465", {"start": v(233.17, 552.39) * mm, "end": v(249.96, 540.18) * mm});
            skLineSegment(sketch, "E466", {"start": v(249.96, 540.18) * mm, "end": v(243.55, 520.44) * mm});
            skLineSegment(sketch, "E467", {"start": v(277.14, 520.44) * mm, "end": v(270.73, 540.18) * mm});
            skLineSegment(sketch, "E468", {"start": v(287.52, 552.39) * mm, "end": v(266.76, 552.39) * mm});
            skCircle(sketch, "E469", {"center": v(260.34, 457.51) * mm, "radius": 28.58 * mm, "construction": true});
            skLineSegment(sketch, "E470", {"start": v(233.17, 466.35) * mm, "end": v(253.93, 466.35) * mm});
            skLineSegment(sketch, "E471", {"start": v(287.52, 466.35) * mm, "end": v(270.73, 454.14) * mm});
            skLineSegment(sketch, "E472", {"start": v(253.93, 466.35) * mm, "end": v(260.34, 486.09) * mm});
            skLineSegment(sketch, "E473", {"start": v(260.34, 486.09) * mm, "end": v(266.76, 466.35) * mm});
            skLineSegment(sketch, "E474", {"start": v(277.14, 434.4) * mm, "end": v(260.34, 446.6) * mm});
            skLineSegment(sketch, "E475", {"start": v(243.55, 434.4) * mm, "end": v(260.34, 446.6) * mm});
            skLineSegment(sketch, "E476", {"start": v(233.17, 466.35) * mm, "end": v(249.96, 454.14) * mm});
            skLineSegment(sketch, "E477", {"start": v(249.96, 454.14) * mm, "end": v(243.55, 434.4) * mm});
            skLineSegment(sketch, "E478", {"start": v(277.14, 434.4) * mm, "end": v(270.73, 454.14) * mm});
            skLineSegment(sketch, "E479", {"start": v(287.52, 466.35) * mm, "end": v(266.76, 466.35) * mm});
            skCircle(sketch, "E480", {"center": v(347.13, 457.51) * mm, "radius": 28.57 * mm, "construction": true});
            skLineSegment(sketch, "E481", {"start": v(319.95, 466.35) * mm, "end": v(340.71, 466.35) * mm});
            skLineSegment(sketch, "E482", {"start": v(374.3, 466.35) * mm, "end": v(357.5, 454.14) * mm});
            skLineSegment(sketch, "E483", {"start": v(340.71, 466.35) * mm, "end": v(347.13, 486.09) * mm});
            skLineSegment(sketch, "E484", {"start": v(347.13, 486.09) * mm, "end": v(353.54, 466.35) * mm});
            skLineSegment(sketch, "E485", {"start": v(363.92, 434.4) * mm, "end": v(347.13, 446.6) * mm});
            skLineSegment(sketch, "E486", {"start": v(330.33, 434.4) * mm, "end": v(347.13, 446.6) * mm});
            skLineSegment(sketch, "E487", {"start": v(319.95, 466.35) * mm, "end": v(336.75, 454.14) * mm});
            skLineSegment(sketch, "E488", {"start": v(336.75, 454.14) * mm, "end": v(330.33, 434.4) * mm});
            skLineSegment(sketch, "E489", {"start": v(363.92, 434.4) * mm, "end": v(357.5, 454.14) * mm});
            skLineSegment(sketch, "E490", {"start": v(374.3, 466.35) * mm, "end": v(353.54, 466.35) * mm});
            skCircle(sketch, "E491", {"center": v(390.52, 414.5) * mm, "radius": 28.58 * mm, "construction": true});
            skLineSegment(sketch, "E492", {"start": v(363.34, 423.33) * mm, "end": v(384.1, 423.33) * mm});
            skLineSegment(sketch, "E493", {"start": v(417.7, 423.33) * mm, "end": v(400.9, 411.12) * mm});
            skLineSegment(sketch, "E494", {"start": v(384.1, 423.33) * mm, "end": v(390.52, 443.07) * mm});
            skLineSegment(sketch, "E495", {"start": v(390.52, 443.07) * mm, "end": v(396.93, 423.33) * mm});
            skLineSegment(sketch, "E496", {"start": v(407.31, 391.38) * mm, "end": v(390.52, 403.58) * mm});
            skLineSegment(sketch, "E497", {"start": v(373.72, 391.38) * mm, "end": v(390.52, 403.58) * mm});
            skLineSegment(sketch, "E498", {"start": v(363.34, 423.33) * mm, "end": v(380.14, 411.12) * mm});
            skLineSegment(sketch, "E499", {"start": v(380.14, 411.12) * mm, "end": v(373.72, 391.38) * mm});
            skLineSegment(sketch, "E500", {"start": v(407.31, 391.38) * mm, "end": v(400.9, 411.12) * mm});
            skLineSegment(sketch, "E501", {"start": v(417.7, 423.33) * mm, "end": v(396.93, 423.33) * mm});
            skCircle(sketch, "E502", {"center": v(390.52, 500.53) * mm, "radius": 28.58 * mm, "construction": true});
            skLineSegment(sketch, "E503", {"start": v(363.34, 509.37) * mm, "end": v(384.1, 509.37) * mm});
            skLineSegment(sketch, "E504", {"start": v(417.7, 509.37) * mm, "end": v(400.9, 497.16) * mm});
            skLineSegment(sketch, "E505", {"start": v(384.1, 509.37) * mm, "end": v(390.52, 529.1) * mm});
            skLineSegment(sketch, "E506", {"start": v(390.52, 529.1) * mm, "end": v(396.93, 509.37) * mm});
            skLineSegment(sketch, "E507", {"start": v(407.31, 477.42) * mm, "end": v(390.52, 489.62) * mm});
            skLineSegment(sketch, "E508", {"start": v(373.72, 477.42) * mm, "end": v(390.52, 489.62) * mm});
            skLineSegment(sketch, "E509", {"start": v(363.34, 509.37) * mm, "end": v(380.14, 497.16) * mm});
            skLineSegment(sketch, "E510", {"start": v(380.14, 497.16) * mm, "end": v(373.72, 477.42) * mm});
            skLineSegment(sketch, "E511", {"start": v(407.31, 477.42) * mm, "end": v(400.9, 497.16) * mm});
            skLineSegment(sketch, "E512", {"start": v(417.7, 509.37) * mm, "end": v(396.93, 509.37) * mm});
            skPoint(sketch, "E513", {"position": v(43.4, 500.53) * mm});
            skPoint(sketch, "E514", {"position": v(303.74, 500.53) * mm});
            skPoint(sketch, "E515", {"position": v(347.13, 543.55) * mm});
            skCircle(sketch, "E516", {"center": v(303.74, 500.53) * mm, "radius": 28.58 * mm, "construction": true});
            skLineSegment(sketch, "E517", {"start": v(276.56, 509.37) * mm, "end": v(297.32, 509.37) * mm});
            skLineSegment(sketch, "E518", {"start": v(330.91, 509.37) * mm, "end": v(314.12, 497.16) * mm});
            skLineSegment(sketch, "E519", {"start": v(297.32, 509.37) * mm, "end": v(303.74, 529.1) * mm});
            skLineSegment(sketch, "E520", {"start": v(303.74, 529.1) * mm, "end": v(310.15, 509.37) * mm});
            skLineSegment(sketch, "E521", {"start": v(320.53, 477.42) * mm, "end": v(303.74, 489.62) * mm});
            skLineSegment(sketch, "E522", {"start": v(286.94, 477.42) * mm, "end": v(303.74, 489.62) * mm});
            skLineSegment(sketch, "E523", {"start": v(276.56, 509.37) * mm, "end": v(293.36, 497.16) * mm});
            skLineSegment(sketch, "E524", {"start": v(293.36, 497.16) * mm, "end": v(286.94, 477.42) * mm});
            skLineSegment(sketch, "E525", {"start": v(320.53, 477.42) * mm, "end": v(314.12, 497.16) * mm});
            skLineSegment(sketch, "E526", {"start": v(330.91, 509.37) * mm, "end": v(310.15, 509.37) * mm});
            skCircle(sketch, "E527", {"center": v(347.13, 543.55) * mm, "radius": 28.58 * mm, "construction": true});
            skLineSegment(sketch, "E528", {"start": v(319.95, 552.39) * mm, "end": v(340.71, 552.39) * mm});
            skLineSegment(sketch, "E529", {"start": v(374.3, 552.39) * mm, "end": v(357.5, 540.18) * mm});
            skLineSegment(sketch, "E530", {"start": v(340.71, 552.39) * mm, "end": v(347.13, 572.13) * mm});
            skLineSegment(sketch, "E531", {"start": v(347.13, 572.13) * mm, "end": v(353.54, 552.39) * mm});
            skLineSegment(sketch, "E532", {"start": v(363.92, 520.44) * mm, "end": v(347.13, 532.64) * mm});
            skLineSegment(sketch, "E533", {"start": v(330.33, 520.44) * mm, "end": v(347.13, 532.64) * mm});
            skLineSegment(sketch, "E534", {"start": v(319.95, 552.39) * mm, "end": v(336.75, 540.18) * mm});
            skLineSegment(sketch, "E535", {"start": v(336.75, 540.18) * mm, "end": v(330.33, 520.44) * mm});
            skLineSegment(sketch, "E536", {"start": v(363.92, 520.44) * mm, "end": v(357.5, 540.18) * mm});
            skLineSegment(sketch, "E537", {"start": v(374.3, 552.39) * mm, "end": v(353.54, 552.39) * mm});
            skCircle(sketch, "E538", {"center": v(303.74, 414.5) * mm, "radius": 28.58 * mm, "construction": true});
            skLineSegment(sketch, "E539", {"start": v(276.56, 423.33) * mm, "end": v(297.32, 423.33) * mm});
            skLineSegment(sketch, "E540", {"start": v(330.91, 423.33) * mm, "end": v(314.12, 411.12) * mm});
            skLineSegment(sketch, "E541", {"start": v(297.32, 423.33) * mm, "end": v(303.74, 443.07) * mm});
            skLineSegment(sketch, "E542", {"start": v(303.74, 443.07) * mm, "end": v(310.15, 423.33) * mm});
            skLineSegment(sketch, "E543", {"start": v(320.53, 391.38) * mm, "end": v(303.74, 403.58) * mm});
            skLineSegment(sketch, "E544", {"start": v(286.94, 391.38) * mm, "end": v(303.74, 403.58) * mm});
            skLineSegment(sketch, "E545", {"start": v(276.56, 423.33) * mm, "end": v(293.36, 411.12) * mm});
            skLineSegment(sketch, "E546", {"start": v(293.36, 411.12) * mm, "end": v(286.94, 391.38) * mm});
            skLineSegment(sketch, "E547", {"start": v(320.53, 391.38) * mm, "end": v(314.12, 411.12) * mm});
            skLineSegment(sketch, "E548", {"start": v(330.91, 423.33) * mm, "end": v(310.15, 423.33) * mm});
            skCircle(sketch, "E549", {"center": v(216.95, 414.5) * mm, "radius": 28.58 * mm, "construction": true});
            skLineSegment(sketch, "E550", {"start": v(189.78, 423.33) * mm, "end": v(210.54, 423.33) * mm});
            skLineSegment(sketch, "E551", {"start": v(244.13, 423.33) * mm, "end": v(227.33, 411.12) * mm});
            skLineSegment(sketch, "E552", {"start": v(210.54, 423.33) * mm, "end": v(216.95, 443.07) * mm});
            skLineSegment(sketch, "E553", {"start": v(216.95, 443.07) * mm, "end": v(223.37, 423.33) * mm});
            skLineSegment(sketch, "E554", {"start": v(233.75, 391.38) * mm, "end": v(216.95, 403.58) * mm});
            skLineSegment(sketch, "E555", {"start": v(200.16, 391.38) * mm, "end": v(216.95, 403.58) * mm});
            skLineSegment(sketch, "E556", {"start": v(189.78, 423.33) * mm, "end": v(206.57, 411.12) * mm});
            skLineSegment(sketch, "E557", {"start": v(206.57, 411.12) * mm, "end": v(200.16, 391.38) * mm});
            skLineSegment(sketch, "E558", {"start": v(233.75, 391.38) * mm, "end": v(227.33, 411.12) * mm});
            skLineSegment(sketch, "E559", {"start": v(244.13, 423.33) * mm, "end": v(223.37, 423.33) * mm});
            skCircle(sketch, "E560", {"center": v(130.17, 414.5) * mm, "radius": 28.58 * mm, "construction": true});
            skLineSegment(sketch, "E561", {"start": v(103, 423.33) * mm, "end": v(123.76, 423.33) * mm});
            skLineSegment(sketch, "E562", {"start": v(157.35, 423.33) * mm, "end": v(140.55, 411.12) * mm});
            skLineSegment(sketch, "E563", {"start": v(123.76, 423.33) * mm, "end": v(130.17, 443.07) * mm});
            skLineSegment(sketch, "E564", {"start": v(130.17, 443.07) * mm, "end": v(136.59, 423.33) * mm});
            skLineSegment(sketch, "E565", {"start": v(146.97, 391.38) * mm, "end": v(130.17, 403.58) * mm});
            skLineSegment(sketch, "E566", {"start": v(113.38, 391.38) * mm, "end": v(130.17, 403.58) * mm});
            skLineSegment(sketch, "E567", {"start": v(103, 423.33) * mm, "end": v(119.8, 411.12) * mm});
            skLineSegment(sketch, "E568", {"start": v(119.8, 411.12) * mm, "end": v(113.38, 391.38) * mm});
            skLineSegment(sketch, "E569", {"start": v(146.97, 391.38) * mm, "end": v(140.55, 411.12) * mm});
            skLineSegment(sketch, "E570", {"start": v(157.35, 423.33) * mm, "end": v(136.59, 423.33) * mm});
            skCircle(sketch, "E571", {"center": v(173.56, 457.51) * mm, "radius": 28.58 * mm, "construction": true});
            skLineSegment(sketch, "E572", {"start": v(146.39, 466.35) * mm, "end": v(167.15, 466.35) * mm});
            skLineSegment(sketch, "E573", {"start": v(200.74, 466.35) * mm, "end": v(183.94, 454.14) * mm});
            skLineSegment(sketch, "E574", {"start": v(167.15, 466.35) * mm, "end": v(173.56, 486.09) * mm});
            skLineSegment(sketch, "E575", {"start": v(173.56, 486.09) * mm, "end": v(179.98, 466.35) * mm});
            skLineSegment(sketch, "E576", {"start": v(190.36, 434.4) * mm, "end": v(173.56, 446.6) * mm});
            skLineSegment(sketch, "E577", {"start": v(156.77, 434.4) * mm, "end": v(173.56, 446.6) * mm});
            skLineSegment(sketch, "E578", {"start": v(146.39, 466.35) * mm, "end": v(163.18, 454.14) * mm});
            skLineSegment(sketch, "E579", {"start": v(163.18, 454.14) * mm, "end": v(156.77, 434.4) * mm});
            skLineSegment(sketch, "E580", {"start": v(190.36, 434.4) * mm, "end": v(183.94, 454.14) * mm});
            skLineSegment(sketch, "E581", {"start": v(200.74, 466.35) * mm, "end": v(179.98, 466.35) * mm});
            skCircle(sketch, "E582", {"center": v(216.95, 500.53) * mm, "radius": 28.58 * mm, "construction": true});
            skLineSegment(sketch, "E583", {"start": v(189.78, 509.37) * mm, "end": v(210.54, 509.37) * mm});
            skLineSegment(sketch, "E584", {"start": v(244.13, 509.37) * mm, "end": v(227.33, 497.16) * mm});
            skLineSegment(sketch, "E585", {"start": v(210.54, 509.37) * mm, "end": v(216.95, 529.1) * mm});
            skLineSegment(sketch, "E586", {"start": v(216.95, 529.1) * mm, "end": v(223.37, 509.37) * mm});
            skLineSegment(sketch, "E587", {"start": v(233.75, 477.42) * mm, "end": v(216.95, 489.62) * mm});
            skLineSegment(sketch, "E588", {"start": v(200.16, 477.42) * mm, "end": v(216.95, 489.62) * mm});
            skLineSegment(sketch, "E589", {"start": v(189.78, 509.37) * mm, "end": v(206.57, 497.16) * mm});
            skLineSegment(sketch, "E590", {"start": v(206.57, 497.16) * mm, "end": v(200.16, 477.42) * mm});
            skLineSegment(sketch, "E591", {"start": v(233.75, 477.42) * mm, "end": v(227.33, 497.16) * mm});
            skLineSegment(sketch, "E592", {"start": v(244.13, 509.37) * mm, "end": v(223.37, 509.37) * mm});
            skCircle(sketch, "E593", {"center": v(86.78, 457.51) * mm, "radius": 28.58 * mm, "construction": true});
            skLineSegment(sketch, "E594", {"start": v(59.6, 466.35) * mm, "end": v(80.37, 466.35) * mm});
            skLineSegment(sketch, "E595", {"start": v(113.96, 466.35) * mm, "end": v(97.16, 454.14) * mm});
            skLineSegment(sketch, "E596", {"start": v(80.37, 466.35) * mm, "end": v(86.78, 486.09) * mm});
            skLineSegment(sketch, "E597", {"start": v(86.78, 486.09) * mm, "end": v(93.2, 466.35) * mm});
            skLineSegment(sketch, "E598", {"start": v(103.58, 434.4) * mm, "end": v(86.78, 446.6) * mm});
            skLineSegment(sketch, "E599", {"start": v(69.99, 434.4) * mm, "end": v(86.78, 446.6) * mm});
            skLineSegment(sketch, "E600", {"start": v(59.6, 466.35) * mm, "end": v(76.4, 454.14) * mm});
            skLineSegment(sketch, "E601", {"start": v(76.4, 454.14) * mm, "end": v(69.99, 434.4) * mm});
            skLineSegment(sketch, "E602", {"start": v(103.58, 434.4) * mm, "end": v(97.16, 454.14) * mm});
            skLineSegment(sketch, "E603", {"start": v(113.96, 466.35) * mm, "end": v(93.2, 466.35) * mm});
            skCircle(sketch, "E604", {"center": v(130.17, 500.53) * mm, "radius": 28.58 * mm, "construction": true});
            skLineSegment(sketch, "E605", {"start": v(103, 509.37) * mm, "end": v(123.76, 509.37) * mm});
            skLineSegment(sketch, "E606", {"start": v(157.35, 509.37) * mm, "end": v(140.55, 497.16) * mm});
            skLineSegment(sketch, "E607", {"start": v(123.76, 509.37) * mm, "end": v(130.17, 529.1) * mm});
            skLineSegment(sketch, "E608", {"start": v(130.17, 529.1) * mm, "end": v(136.59, 509.37) * mm});
            skLineSegment(sketch, "E609", {"start": v(146.97, 477.42) * mm, "end": v(130.17, 489.62) * mm});
            skLineSegment(sketch, "E610", {"start": v(113.38, 477.42) * mm, "end": v(130.17, 489.62) * mm});
            skLineSegment(sketch, "E611", {"start": v(103, 509.37) * mm, "end": v(119.8, 497.16) * mm});
            skLineSegment(sketch, "E612", {"start": v(119.8, 497.16) * mm, "end": v(113.38, 477.42) * mm});
            skLineSegment(sketch, "E613", {"start": v(146.97, 477.42) * mm, "end": v(140.55, 497.16) * mm});
            skLineSegment(sketch, "E614", {"start": v(157.35, 509.37) * mm, "end": v(136.59, 509.37) * mm});
            skPoint(sketch, "E615", {"position": v(43.4, 414.5) * mm});
            skCircle(sketch, "E616", {"center": v(43.4, 414.5) * mm, "radius": 28.58 * mm, "construction": true});
            skLineSegment(sketch, "E617", {"start": v(16.21, 423.33) * mm, "end": v(36.98, 423.33) * mm});
            skLineSegment(sketch, "E618", {"start": v(70.57, 423.33) * mm, "end": v(53.77, 411.12) * mm});
            skLineSegment(sketch, "E619", {"start": v(36.98, 423.33) * mm, "end": v(43.4, 443.07) * mm});
            skLineSegment(sketch, "E620", {"start": v(43.4, 443.07) * mm, "end": v(49.8, 423.33) * mm});
            skLineSegment(sketch, "E621", {"start": v(60.19, 391.38) * mm, "end": v(43.4, 403.58) * mm});
            skLineSegment(sketch, "E622", {"start": v(26.6, 391.38) * mm, "end": v(43.4, 403.58) * mm});
            skLineSegment(sketch, "E623", {"start": v(16.21, 423.33) * mm, "end": v(33.01, 411.12) * mm});
            skLineSegment(sketch, "E624", {"start": v(33.01, 411.12) * mm, "end": v(26.6, 391.38) * mm});
            skLineSegment(sketch, "E625", {"start": v(60.19, 391.38) * mm, "end": v(53.77, 411.12) * mm});
            skLineSegment(sketch, "E626", {"start": v(70.57, 423.33) * mm, "end": v(49.8, 423.33) * mm});
            skCircle(sketch, "E627", {"center": v(43.4, 500.53) * mm, "radius": 28.58 * mm, "construction": true});
            skLineSegment(sketch, "E628", {"start": v(16.21, 509.37) * mm, "end": v(36.98, 509.37) * mm});
            skLineSegment(sketch, "E629", {"start": v(70.57, 509.37) * mm, "end": v(53.77, 497.16) * mm});
            skLineSegment(sketch, "E630", {"start": v(36.98, 509.37) * mm, "end": v(43.4, 529.1) * mm});
            skLineSegment(sketch, "E631", {"start": v(43.4, 529.1) * mm, "end": v(49.8, 509.37) * mm});
            skLineSegment(sketch, "E632", {"start": v(60.19, 477.42) * mm, "end": v(43.4, 489.62) * mm});
            skLineSegment(sketch, "E633", {"start": v(26.6, 477.42) * mm, "end": v(43.4, 489.62) * mm});
            skLineSegment(sketch, "E634", {"start": v(16.21, 509.37) * mm, "end": v(33.01, 497.16) * mm});
            skLineSegment(sketch, "E635", {"start": v(33.01, 497.16) * mm, "end": v(26.6, 477.42) * mm});
            skLineSegment(sketch, "E636", {"start": v(60.19, 477.42) * mm, "end": v(53.77, 497.16) * mm});
            skLineSegment(sketch, "E637", {"start": v(70.57, 509.37) * mm, "end": v(49.8, 509.37) * mm});
            skCircle(sketch, "E638", {"center": v(86.78, 543.55) * mm, "radius": 28.58 * mm, "construction": true});
            skLineSegment(sketch, "E639", {"start": v(59.6, 552.39) * mm, "end": v(80.37, 552.39) * mm});
            skLineSegment(sketch, "E640", {"start": v(113.96, 552.39) * mm, "end": v(97.16, 540.18) * mm});
            skLineSegment(sketch, "E641", {"start": v(80.37, 552.39) * mm, "end": v(86.78, 572.13) * mm});
            skLineSegment(sketch, "E642", {"start": v(86.78, 572.13) * mm, "end": v(93.2, 552.39) * mm});
            skLineSegment(sketch, "E643", {"start": v(103.58, 520.44) * mm, "end": v(86.78, 532.64) * mm});
            skLineSegment(sketch, "E644", {"start": v(69.99, 520.44) * mm, "end": v(86.78, 532.64) * mm});
            skLineSegment(sketch, "E645", {"start": v(59.6, 552.39) * mm, "end": v(76.4, 540.18) * mm});
            skLineSegment(sketch, "E646", {"start": v(76.4, 540.18) * mm, "end": v(69.99, 520.44) * mm});
            skLineSegment(sketch, "E647", {"start": v(103.58, 520.44) * mm, "end": v(97.16, 540.18) * mm});
            skLineSegment(sketch, "E648", {"start": v(113.96, 552.39) * mm, "end": v(93.2, 552.39) * mm});
            skCircle(sketch, "E649", {"center": v(173.56, 543.55) * mm, "radius": 28.58 * mm, "construction": true});
            skLineSegment(sketch, "E650", {"start": v(146.39, 552.39) * mm, "end": v(167.15, 552.39) * mm});
            skLineSegment(sketch, "E651", {"start": v(200.74, 552.39) * mm, "end": v(183.94, 540.18) * mm});
            skLineSegment(sketch, "E652", {"start": v(167.15, 552.39) * mm, "end": v(173.56, 572.13) * mm});
            skLineSegment(sketch, "E653", {"start": v(173.56, 572.13) * mm, "end": v(179.98, 552.39) * mm});
            skLineSegment(sketch, "E654", {"start": v(190.36, 520.44) * mm, "end": v(173.56, 532.64) * mm});
            skLineSegment(sketch, "E655", {"start": v(156.77, 520.44) * mm, "end": v(173.56, 532.64) * mm});
            skLineSegment(sketch, "E656", {"start": v(146.39, 552.39) * mm, "end": v(163.18, 540.18) * mm});
            skLineSegment(sketch, "E657", {"start": v(163.18, 540.18) * mm, "end": v(156.77, 520.44) * mm});
            skLineSegment(sketch, "E658", {"start": v(190.36, 520.44) * mm, "end": v(183.94, 540.18) * mm});
            skLineSegment(sketch, "E659", {"start": v(200.74, 552.39) * mm, "end": v(179.98, 552.39) * mm});
            skSolve(sketch);
        }
        {
            var Q0;
            Q0=qCreatedBy(makeId("Front.planeOp"),FACE);
            var sketch = newSketch(context, id + "F2", { "sketchPlane" : qUnion([Q0])});
            skLineSegment(sketch, "E660.0.0", {"start": v(43.4, 747.74) * mm, "end": v(60.19, 735.54) * mm});
            skLineSegment(sketch, "E660.0.1", {"start": v(60.19, 735.54) * mm, "end": v(53.77, 755.28) * mm});
            skLineSegment(sketch, "E660.0.2", {"start": v(53.77, 755.28) * mm, "end": v(70.57, 767.48) * mm});
            skLineSegment(sketch, "E660.0.3", {"start": v(70.57, 767.48) * mm, "end": v(49.8, 767.48) * mm});
            skLineSegment(sketch, "E660.0.4", {"start": v(49.8, 767.48) * mm, "end": v(43.4, 787.23) * mm});
            skLineSegment(sketch, "E660.0.5", {"start": v(43.4, 787.23) * mm, "end": v(36.98, 767.48) * mm});
            skLineSegment(sketch, "E660.0.6", {"start": v(36.98, 767.48) * mm, "end": v(16.21, 767.48) * mm});
            skLineSegment(sketch, "E660.0.7", {"start": v(16.21, 767.48) * mm, "end": v(33.01, 755.28) * mm});
            skLineSegment(sketch, "E660.0.8", {"start": v(33.01, 755.28) * mm, "end": v(26.6, 735.54) * mm});
            skLineSegment(sketch, "E660.0.9", {"start": v(26.6, 735.54) * mm, "end": v(43.4, 747.74) * mm});
            skLineSegment(sketch, "E661.0.0", {"start": v(130.17, 747.74) * mm, "end": v(146.97, 735.54) * mm});
            skLineSegment(sketch, "E661.0.1", {"start": v(146.97, 735.54) * mm, "end": v(140.55, 755.28) * mm});
            skLineSegment(sketch, "E661.0.2", {"start": v(140.55, 755.28) * mm, "end": v(157.35, 767.48) * mm});
            skLineSegment(sketch, "E661.0.3", {"start": v(157.35, 767.48) * mm, "end": v(136.59, 767.48) * mm});
            skLineSegment(sketch, "E661.0.4", {"start": v(136.59, 767.48) * mm, "end": v(130.17, 787.23) * mm});
            skLineSegment(sketch, "E661.0.5", {"start": v(130.17, 787.23) * mm, "end": v(123.76, 767.48) * mm});
            skLineSegment(sketch, "E661.0.6", {"start": v(123.76, 767.48) * mm, "end": v(103, 767.48) * mm});
            skLineSegment(sketch, "E661.0.7", {"start": v(103, 767.48) * mm, "end": v(119.8, 755.28) * mm});
            skLineSegment(sketch, "E661.0.8", {"start": v(119.8, 755.28) * mm, "end": v(113.38, 735.54) * mm});
            skLineSegment(sketch, "E661.0.9", {"start": v(113.38, 735.54) * mm, "end": v(130.17, 747.74) * mm});
            skLineSegment(sketch, "E662.0.0", {"start": v(216.95, 747.74) * mm, "end": v(233.75, 735.54) * mm});
            skLineSegment(sketch, "E662.0.1", {"start": v(233.75, 735.54) * mm, "end": v(227.33, 755.28) * mm});
            skLineSegment(sketch, "E662.0.2", {"start": v(227.33, 755.28) * mm, "end": v(244.13, 767.48) * mm});
            skLineSegment(sketch, "E662.0.3", {"start": v(244.13, 767.48) * mm, "end": v(223.37, 767.48) * mm});
            skLineSegment(sketch, "E662.0.4", {"start": v(223.37, 767.48) * mm, "end": v(216.95, 787.23) * mm});
            skLineSegment(sketch, "E662.0.5", {"start": v(216.95, 787.23) * mm, "end": v(210.54, 767.48) * mm});
            skLineSegment(sketch, "E662.0.6", {"start": v(210.54, 767.48) * mm, "end": v(189.78, 767.48) * mm});
            skLineSegment(sketch, "E662.0.7", {"start": v(189.78, 767.48) * mm, "end": v(206.57, 755.28) * mm});
            skLineSegment(sketch, "E662.0.8", {"start": v(206.57, 755.28) * mm, "end": v(200.16, 735.54) * mm});
            skLineSegment(sketch, "E662.0.9", {"start": v(200.16, 735.54) * mm, "end": v(216.95, 747.74) * mm});
            skLineSegment(sketch, "E663.0.0", {"start": v(303.74, 747.74) * mm, "end": v(320.53, 735.54) * mm});
            skLineSegment(sketch, "E663.0.1", {"start": v(320.53, 735.54) * mm, "end": v(314.12, 755.28) * mm});
            skLineSegment(sketch, "E663.0.2", {"start": v(314.12, 755.28) * mm, "end": v(330.91, 767.48) * mm});
            skLineSegment(sketch, "E663.0.3", {"start": v(330.91, 767.48) * mm, "end": v(310.15, 767.48) * mm});
            skLineSegment(sketch, "E663.0.4", {"start": v(310.15, 767.48) * mm, "end": v(303.74, 787.23) * mm});
            skLineSegment(sketch, "E663.0.5", {"start": v(303.74, 787.23) * mm, "end": v(297.32, 767.48) * mm});
            skLineSegment(sketch, "E663.0.6", {"start": v(297.32, 767.48) * mm, "end": v(276.56, 767.48) * mm});
            skLineSegment(sketch, "E663.0.7", {"start": v(276.56, 767.48) * mm, "end": v(293.36, 755.28) * mm});
            skLineSegment(sketch, "E663.0.8", {"start": v(293.36, 755.28) * mm, "end": v(286.94, 735.54) * mm});
            skLineSegment(sketch, "E663.0.9", {"start": v(286.94, 735.54) * mm, "end": v(303.74, 747.74) * mm});
            skLineSegment(sketch, "E664.0.0", {"start": v(390.52, 747.74) * mm, "end": v(407.31, 735.54) * mm});
            skLineSegment(sketch, "E664.0.1", {"start": v(407.31, 735.54) * mm, "end": v(400.9, 755.28) * mm});
            skLineSegment(sketch, "E664.0.2", {"start": v(400.9, 755.28) * mm, "end": v(417.7, 767.48) * mm});
            skLineSegment(sketch, "E664.0.3", {"start": v(417.7, 767.48) * mm, "end": v(396.93, 767.48) * mm});
            skLineSegment(sketch, "E664.0.4", {"start": v(396.93, 767.48) * mm, "end": v(390.52, 787.23) * mm});
            skLineSegment(sketch, "E664.0.5", {"start": v(390.52, 787.23) * mm, "end": v(384.1, 767.48) * mm});
            skLineSegment(sketch, "E664.0.6", {"start": v(384.1, 767.48) * mm, "end": v(363.34, 767.48) * mm});
            skLineSegment(sketch, "E664.0.7", {"start": v(363.34, 767.48) * mm, "end": v(380.14, 755.28) * mm});
            skLineSegment(sketch, "E664.0.8", {"start": v(380.14, 755.28) * mm, "end": v(373.72, 735.54) * mm});
            skLineSegment(sketch, "E664.0.9", {"start": v(373.72, 735.54) * mm, "end": v(390.52, 747.74) * mm});
            skLineSegment(sketch, "E665.0.0", {"start": v(477.3, 747.74) * mm, "end": v(494.1, 735.54) * mm});
            skLineSegment(sketch, "E665.0.1", {"start": v(494.1, 735.54) * mm, "end": v(487.68, 755.28) * mm});
            skLineSegment(sketch, "E665.0.2", {"start": v(487.68, 755.28) * mm, "end": v(504.48, 767.48) * mm});
            skLineSegment(sketch, "E665.0.3", {"start": v(504.48, 767.48) * mm, "end": v(483.71, 767.48) * mm});
            skLineSegment(sketch, "E665.0.4", {"start": v(483.71, 767.48) * mm, "end": v(477.3, 787.23) * mm});
            skLineSegment(sketch, "E665.0.5", {"start": v(477.3, 787.23) * mm, "end": v(470.88, 767.48) * mm});
            skLineSegment(sketch, "E665.0.6", {"start": v(470.88, 767.48) * mm, "end": v(450.12, 767.48) * mm});
            skLineSegment(sketch, "E665.0.7", {"start": v(450.12, 767.48) * mm, "end": v(466.92, 755.28) * mm});
            skLineSegment(sketch, "E665.0.8", {"start": v(466.92, 755.28) * mm, "end": v(460.5, 735.54) * mm});
            skLineSegment(sketch, "E665.0.9", {"start": v(460.5, 735.54) * mm, "end": v(477.3, 747.74) * mm});
            skLineSegment(sketch, "E666.0.0", {"start": v(433.9, 704.72) * mm, "end": v(450.7, 692.52) * mm});
            skLineSegment(sketch, "E666.0.1", {"start": v(450.7, 692.52) * mm, "end": v(444.29, 712.26) * mm});
            skLineSegment(sketch, "E666.0.2", {"start": v(444.29, 712.26) * mm, "end": v(461.08, 724.47) * mm});
            skLineSegment(sketch, "E666.0.3", {"start": v(461.08, 724.47) * mm, "end": v(440.32, 724.47) * mm});
            skLineSegment(sketch, "E666.0.4", {"start": v(440.32, 724.47) * mm, "end": v(433.9, 744.2) * mm});
            skLineSegment(sketch, "E666.0.5", {"start": v(433.9, 744.2) * mm, "end": v(427.5, 724.47) * mm});
            skLineSegment(sketch, "E666.0.6", {"start": v(427.5, 724.47) * mm, "end": v(406.73, 724.47) * mm});
            skLineSegment(sketch, "E666.0.7", {"start": v(406.73, 724.47) * mm, "end": v(423.53, 712.26) * mm});
            skLineSegment(sketch, "E666.0.8", {"start": v(423.53, 712.26) * mm, "end": v(417.11, 692.52) * mm});
            skLineSegment(sketch, "E666.0.9", {"start": v(417.11, 692.52) * mm, "end": v(433.9, 704.72) * mm});
            skLineSegment(sketch, "E667.0.0", {"start": v(347.13, 704.72) * mm, "end": v(363.92, 692.52) * mm});
            skLineSegment(sketch, "E667.0.1", {"start": v(363.92, 692.52) * mm, "end": v(357.5, 712.26) * mm});
            skLineSegment(sketch, "E667.0.2", {"start": v(357.5, 712.26) * mm, "end": v(374.3, 724.47) * mm});
            skLineSegment(sketch, "E667.0.3", {"start": v(374.3, 724.47) * mm, "end": v(353.54, 724.47) * mm});
            skLineSegment(sketch, "E667.0.4", {"start": v(353.54, 724.47) * mm, "end": v(347.13, 744.2) * mm});
            skLineSegment(sketch, "E667.0.5", {"start": v(347.13, 744.2) * mm, "end": v(340.71, 724.47) * mm});
            skLineSegment(sketch, "E667.0.6", {"start": v(340.71, 724.47) * mm, "end": v(319.95, 724.47) * mm});
            skLineSegment(sketch, "E667.0.7", {"start": v(319.95, 724.47) * mm, "end": v(336.75, 712.26) * mm});
            skLineSegment(sketch, "E667.0.8", {"start": v(336.75, 712.26) * mm, "end": v(330.33, 692.52) * mm});
            skLineSegment(sketch, "E667.0.9", {"start": v(330.33, 692.52) * mm, "end": v(347.13, 704.72) * mm});
            skLineSegment(sketch, "E668.0.0", {"start": v(260.34, 704.72) * mm, "end": v(277.14, 692.52) * mm});
            skLineSegment(sketch, "E668.0.1", {"start": v(277.14, 692.52) * mm, "end": v(270.73, 712.26) * mm});
            skLineSegment(sketch, "E668.0.2", {"start": v(270.73, 712.26) * mm, "end": v(287.52, 724.47) * mm});
            skLineSegment(sketch, "E668.0.3", {"start": v(287.52, 724.47) * mm, "end": v(266.76, 724.47) * mm});
            skLineSegment(sketch, "E668.0.4", {"start": v(266.76, 724.47) * mm, "end": v(260.34, 744.2) * mm});
            skLineSegment(sketch, "E668.0.5", {"start": v(260.34, 744.2) * mm, "end": v(253.93, 724.47) * mm});
            skLineSegment(sketch, "E668.0.6", {"start": v(253.93, 724.47) * mm, "end": v(233.17, 724.47) * mm});
            skLineSegment(sketch, "E668.0.7", {"start": v(233.17, 724.47) * mm, "end": v(249.96, 712.26) * mm});
            skLineSegment(sketch, "E668.0.8", {"start": v(249.96, 712.26) * mm, "end": v(243.55, 692.52) * mm});
            skLineSegment(sketch, "E668.0.9", {"start": v(243.55, 692.52) * mm, "end": v(260.34, 704.72) * mm});
            skLineSegment(sketch, "E669.0.0", {"start": v(173.56, 704.72) * mm, "end": v(190.36, 692.52) * mm});
            skLineSegment(sketch, "E669.0.1", {"start": v(190.36, 692.52) * mm, "end": v(183.94, 712.26) * mm});
            skLineSegment(sketch, "E669.0.2", {"start": v(183.94, 712.26) * mm, "end": v(200.74, 724.47) * mm});
            skLineSegment(sketch, "E669.0.3", {"start": v(200.74, 724.47) * mm, "end": v(179.98, 724.47) * mm});
            skLineSegment(sketch, "E669.0.4", {"start": v(179.98, 724.47) * mm, "end": v(173.56, 744.2) * mm});
            skLineSegment(sketch, "E669.0.5", {"start": v(173.56, 744.2) * mm, "end": v(167.15, 724.47) * mm});
            skLineSegment(sketch, "E669.0.6", {"start": v(167.15, 724.47) * mm, "end": v(146.39, 724.47) * mm});
            skLineSegment(sketch, "E669.0.7", {"start": v(146.39, 724.47) * mm, "end": v(163.18, 712.26) * mm});
            skLineSegment(sketch, "E669.0.8", {"start": v(163.18, 712.26) * mm, "end": v(156.77, 692.52) * mm});
            skLineSegment(sketch, "E669.0.9", {"start": v(156.77, 692.52) * mm, "end": v(173.56, 704.72) * mm});
            skLineSegment(sketch, "E670.0.0", {"start": v(86.78, 704.72) * mm, "end": v(103.58, 692.52) * mm});
            skLineSegment(sketch, "E670.0.1", {"start": v(103.58, 692.52) * mm, "end": v(97.16, 712.26) * mm});
            skLineSegment(sketch, "E670.0.2", {"start": v(97.16, 712.26) * mm, "end": v(113.96, 724.47) * mm});
            skLineSegment(sketch, "E670.0.3", {"start": v(113.96, 724.47) * mm, "end": v(93.2, 724.47) * mm});
            skLineSegment(sketch, "E670.0.4", {"start": v(93.2, 724.47) * mm, "end": v(86.78, 744.2) * mm});
            skLineSegment(sketch, "E670.0.5", {"start": v(86.78, 744.2) * mm, "end": v(80.37, 724.47) * mm});
            skLineSegment(sketch, "E670.0.6", {"start": v(80.37, 724.47) * mm, "end": v(59.6, 724.47) * mm});
            skLineSegment(sketch, "E670.0.7", {"start": v(59.6, 724.47) * mm, "end": v(76.4, 712.26) * mm});
            skLineSegment(sketch, "E670.0.8", {"start": v(76.4, 712.26) * mm, "end": v(69.99, 692.52) * mm});
            skLineSegment(sketch, "E670.0.9", {"start": v(69.99, 692.52) * mm, "end": v(86.78, 704.72) * mm});
            skLineSegment(sketch, "E671.0.0", {"start": v(43.4, 661.7) * mm, "end": v(60.19, 649.5) * mm});
            skLineSegment(sketch, "E671.0.1", {"start": v(60.19, 649.5) * mm, "end": v(53.77, 669.24) * mm});
            skLineSegment(sketch, "E671.0.2", {"start": v(53.77, 669.24) * mm, "end": v(70.57, 681.45) * mm});
            skLineSegment(sketch, "E671.0.3", {"start": v(70.57, 681.45) * mm, "end": v(49.8, 681.45) * mm});
            skLineSegment(sketch, "E671.0.4", {"start": v(49.8, 681.45) * mm, "end": v(43.4, 701.19) * mm});
            skLineSegment(sketch, "E671.0.5", {"start": v(43.4, 701.19) * mm, "end": v(36.98, 681.45) * mm});
            skLineSegment(sketch, "E671.0.6", {"start": v(36.98, 681.45) * mm, "end": v(16.21, 681.45) * mm});
            skLineSegment(sketch, "E671.0.7", {"start": v(16.21, 681.45) * mm, "end": v(33.01, 669.24) * mm});
            skLineSegment(sketch, "E671.0.8", {"start": v(33.01, 669.24) * mm, "end": v(26.6, 649.5) * mm});
            skLineSegment(sketch, "E671.0.9", {"start": v(26.6, 649.5) * mm, "end": v(43.4, 661.7) * mm});
            skLineSegment(sketch, "E672.0.0", {"start": v(130.17, 661.7) * mm, "end": v(146.97, 649.5) * mm});
            skLineSegment(sketch, "E672.0.1", {"start": v(146.97, 649.5) * mm, "end": v(140.55, 669.24) * mm});
            skLineSegment(sketch, "E672.0.2", {"start": v(140.55, 669.24) * mm, "end": v(157.35, 681.45) * mm});
            skLineSegment(sketch, "E672.0.3", {"start": v(157.35, 681.45) * mm, "end": v(136.59, 681.45) * mm});
            skLineSegment(sketch, "E672.0.4", {"start": v(136.59, 681.45) * mm, "end": v(130.17, 701.19) * mm});
            skLineSegment(sketch, "E672.0.5", {"start": v(130.17, 701.19) * mm, "end": v(123.76, 681.45) * mm});
            skLineSegment(sketch, "E672.0.6", {"start": v(123.76, 681.45) * mm, "end": v(103, 681.45) * mm});
            skLineSegment(sketch, "E672.0.7", {"start": v(103, 681.45) * mm, "end": v(119.8, 669.24) * mm});
            skLineSegment(sketch, "E672.0.8", {"start": v(119.8, 669.24) * mm, "end": v(113.38, 649.5) * mm});
            skLineSegment(sketch, "E672.0.9", {"start": v(113.38, 649.5) * mm, "end": v(130.17, 661.7) * mm});
            skLineSegment(sketch, "E673.0.0", {"start": v(216.95, 661.7) * mm, "end": v(233.75, 649.5) * mm});
            skLineSegment(sketch, "E673.0.1", {"start": v(233.75, 649.5) * mm, "end": v(227.33, 669.24) * mm});
            skLineSegment(sketch, "E673.0.2", {"start": v(227.33, 669.24) * mm, "end": v(244.13, 681.45) * mm});
            skLineSegment(sketch, "E673.0.3", {"start": v(244.13, 681.45) * mm, "end": v(223.37, 681.45) * mm});
            skLineSegment(sketch, "E673.0.4", {"start": v(223.37, 681.45) * mm, "end": v(216.95, 701.19) * mm});
            skLineSegment(sketch, "E673.0.5", {"start": v(216.95, 701.19) * mm, "end": v(210.54, 681.45) * mm});
            skLineSegment(sketch, "E673.0.6", {"start": v(210.54, 681.45) * mm, "end": v(189.78, 681.45) * mm});
            skLineSegment(sketch, "E673.0.7", {"start": v(189.78, 681.45) * mm, "end": v(206.57, 669.24) * mm});
            skLineSegment(sketch, "E673.0.8", {"start": v(206.57, 669.24) * mm, "end": v(200.16, 649.5) * mm});
            skLineSegment(sketch, "E673.0.9", {"start": v(200.16, 649.5) * mm, "end": v(216.95, 661.7) * mm});
            skLineSegment(sketch, "E674.0.0", {"start": v(303.74, 661.7) * mm, "end": v(320.53, 649.5) * mm});
            skLineSegment(sketch, "E674.0.1", {"start": v(320.53, 649.5) * mm, "end": v(314.12, 669.24) * mm});
            skLineSegment(sketch, "E674.0.2", {"start": v(314.12, 669.24) * mm, "end": v(330.91, 681.45) * mm});
            skLineSegment(sketch, "E674.0.3", {"start": v(330.91, 681.45) * mm, "end": v(310.15, 681.45) * mm});
            skLineSegment(sketch, "E674.0.4", {"start": v(310.15, 681.45) * mm, "end": v(303.74, 701.19) * mm});
            skLineSegment(sketch, "E674.0.5", {"start": v(303.74, 701.19) * mm, "end": v(297.32, 681.45) * mm});
            skLineSegment(sketch, "E674.0.6", {"start": v(297.32, 681.45) * mm, "end": v(276.56, 681.45) * mm});
            skLineSegment(sketch, "E674.0.7", {"start": v(276.56, 681.45) * mm, "end": v(293.36, 669.24) * mm});
            skLineSegment(sketch, "E674.0.8", {"start": v(293.36, 669.24) * mm, "end": v(286.94, 649.5) * mm});
            skLineSegment(sketch, "E674.0.9", {"start": v(286.94, 649.5) * mm, "end": v(303.74, 661.7) * mm});
            skLineSegment(sketch, "E675.0.0", {"start": v(390.52, 661.7) * mm, "end": v(407.31, 649.5) * mm});
            skLineSegment(sketch, "E675.0.1", {"start": v(407.31, 649.5) * mm, "end": v(400.9, 669.24) * mm});
            skLineSegment(sketch, "E675.0.2", {"start": v(400.9, 669.24) * mm, "end": v(417.7, 681.45) * mm});
            skLineSegment(sketch, "E675.0.3", {"start": v(417.7, 681.45) * mm, "end": v(396.93, 681.45) * mm});
            skLineSegment(sketch, "E675.0.4", {"start": v(396.93, 681.45) * mm, "end": v(390.52, 701.19) * mm});
            skLineSegment(sketch, "E675.0.5", {"start": v(390.52, 701.19) * mm, "end": v(384.1, 681.45) * mm});
            skLineSegment(sketch, "E675.0.6", {"start": v(384.1, 681.45) * mm, "end": v(363.34, 681.45) * mm});
            skLineSegment(sketch, "E675.0.7", {"start": v(363.34, 681.45) * mm, "end": v(380.14, 669.24) * mm});
            skLineSegment(sketch, "E675.0.8", {"start": v(380.14, 669.24) * mm, "end": v(373.72, 649.5) * mm});
            skLineSegment(sketch, "E675.0.9", {"start": v(373.72, 649.5) * mm, "end": v(390.52, 661.7) * mm});
            skLineSegment(sketch, "E676.0.0", {"start": v(477.3, 661.7) * mm, "end": v(494.1, 649.5) * mm});
            skLineSegment(sketch, "E676.0.1", {"start": v(494.1, 649.5) * mm, "end": v(487.68, 669.24) * mm});
            skLineSegment(sketch, "E676.0.2", {"start": v(487.68, 669.24) * mm, "end": v(504.48, 681.45) * mm});
            skLineSegment(sketch, "E676.0.3", {"start": v(504.48, 681.45) * mm, "end": v(483.71, 681.45) * mm});
            skLineSegment(sketch, "E676.0.4", {"start": v(483.71, 681.45) * mm, "end": v(477.3, 701.19) * mm});
            skLineSegment(sketch, "E676.0.5", {"start": v(477.3, 701.19) * mm, "end": v(470.88, 681.45) * mm});
            skLineSegment(sketch, "E676.0.6", {"start": v(470.88, 681.45) * mm, "end": v(450.12, 681.45) * mm});
            skLineSegment(sketch, "E676.0.7", {"start": v(450.12, 681.45) * mm, "end": v(466.92, 669.24) * mm});
            skLineSegment(sketch, "E676.0.8", {"start": v(466.92, 669.24) * mm, "end": v(460.5, 649.5) * mm});
            skLineSegment(sketch, "E676.0.9", {"start": v(460.5, 649.5) * mm, "end": v(477.3, 661.7) * mm});
            skLineSegment(sketch, "E677.0.0", {"start": v(86.78, 618.68) * mm, "end": v(103.58, 606.48) * mm});
            skLineSegment(sketch, "E677.0.1", {"start": v(103.58, 606.48) * mm, "end": v(97.16, 626.22) * mm});
            skLineSegment(sketch, "E677.0.2", {"start": v(97.16, 626.22) * mm, "end": v(113.96, 638.43) * mm});
            skLineSegment(sketch, "E677.0.3", {"start": v(113.96, 638.43) * mm, "end": v(93.2, 638.43) * mm});
            skLineSegment(sketch, "E677.0.4", {"start": v(93.2, 638.43) * mm, "end": v(86.78, 658.17) * mm});
            skLineSegment(sketch, "E677.0.5", {"start": v(86.78, 658.17) * mm, "end": v(80.37, 638.43) * mm});
            skLineSegment(sketch, "E677.0.6", {"start": v(80.37, 638.43) * mm, "end": v(59.6, 638.43) * mm});
            skLineSegment(sketch, "E677.0.7", {"start": v(59.6, 638.43) * mm, "end": v(76.4, 626.22) * mm});
            skLineSegment(sketch, "E677.0.8", {"start": v(76.4, 626.22) * mm, "end": v(69.99, 606.48) * mm});
            skLineSegment(sketch, "E677.0.9", {"start": v(69.99, 606.48) * mm, "end": v(86.78, 618.68) * mm});
            skLineSegment(sketch, "E678.0.0", {"start": v(173.56, 618.68) * mm, "end": v(190.36, 606.48) * mm});
            skLineSegment(sketch, "E678.0.1", {"start": v(190.36, 606.48) * mm, "end": v(183.94, 626.22) * mm});
            skLineSegment(sketch, "E678.0.2", {"start": v(183.94, 626.22) * mm, "end": v(200.74, 638.43) * mm});
            skLineSegment(sketch, "E678.0.3", {"start": v(200.74, 638.43) * mm, "end": v(179.98, 638.43) * mm});
            skLineSegment(sketch, "E678.0.4", {"start": v(179.98, 638.43) * mm, "end": v(173.56, 658.17) * mm});
            skLineSegment(sketch, "E678.0.5", {"start": v(173.56, 658.17) * mm, "end": v(167.15, 638.43) * mm});
            skLineSegment(sketch, "E678.0.6", {"start": v(167.15, 638.43) * mm, "end": v(146.39, 638.43) * mm});
            skLineSegment(sketch, "E678.0.7", {"start": v(146.39, 638.43) * mm, "end": v(163.18, 626.22) * mm});
            skLineSegment(sketch, "E678.0.8", {"start": v(163.18, 626.22) * mm, "end": v(156.77, 606.48) * mm});
            skLineSegment(sketch, "E678.0.9", {"start": v(156.77, 606.48) * mm, "end": v(173.56, 618.68) * mm});
            skLineSegment(sketch, "E679.0.0", {"start": v(260.34, 618.68) * mm, "end": v(277.14, 606.48) * mm});
            skLineSegment(sketch, "E679.0.1", {"start": v(277.14, 606.48) * mm, "end": v(270.73, 626.22) * mm});
            skLineSegment(sketch, "E679.0.2", {"start": v(270.73, 626.22) * mm, "end": v(287.52, 638.43) * mm});
            skLineSegment(sketch, "E679.0.3", {"start": v(287.52, 638.43) * mm, "end": v(266.76, 638.43) * mm});
            skLineSegment(sketch, "E679.0.4", {"start": v(266.76, 638.43) * mm, "end": v(260.34, 658.17) * mm});
            skLineSegment(sketch, "E679.0.5", {"start": v(260.34, 658.17) * mm, "end": v(253.93, 638.43) * mm});
            skLineSegment(sketch, "E679.0.6", {"start": v(253.93, 638.43) * mm, "end": v(233.17, 638.43) * mm});
            skLineSegment(sketch, "E679.0.7", {"start": v(233.17, 638.43) * mm, "end": v(249.96, 626.22) * mm});
            skLineSegment(sketch, "E679.0.8", {"start": v(249.96, 626.22) * mm, "end": v(243.55, 606.48) * mm});
            skLineSegment(sketch, "E679.0.9", {"start": v(243.55, 606.48) * mm, "end": v(260.34, 618.68) * mm});
            skLineSegment(sketch, "E680.0.0", {"start": v(347.13, 618.68) * mm, "end": v(363.92, 606.48) * mm});
            skLineSegment(sketch, "E680.0.1", {"start": v(363.92, 606.48) * mm, "end": v(357.5, 626.22) * mm});
            skLineSegment(sketch, "E680.0.2", {"start": v(357.5, 626.22) * mm, "end": v(374.3, 638.43) * mm});
            skLineSegment(sketch, "E680.0.3", {"start": v(374.3, 638.43) * mm, "end": v(353.54, 638.43) * mm});
            skLineSegment(sketch, "E680.0.4", {"start": v(353.54, 638.43) * mm, "end": v(347.13, 658.17) * mm});
            skLineSegment(sketch, "E680.0.5", {"start": v(347.13, 658.17) * mm, "end": v(340.71, 638.43) * mm});
            skLineSegment(sketch, "E680.0.6", {"start": v(340.71, 638.43) * mm, "end": v(319.95, 638.43) * mm});
            skLineSegment(sketch, "E680.0.7", {"start": v(319.95, 638.43) * mm, "end": v(336.75, 626.22) * mm});
            skLineSegment(sketch, "E680.0.8", {"start": v(336.75, 626.22) * mm, "end": v(330.33, 606.48) * mm});
            skLineSegment(sketch, "E680.0.9", {"start": v(330.33, 606.48) * mm, "end": v(347.13, 618.68) * mm});
            skLineSegment(sketch, "E681.0.0", {"start": v(433.9, 618.68) * mm, "end": v(450.7, 606.48) * mm});
            skLineSegment(sketch, "E681.0.1", {"start": v(450.7, 606.48) * mm, "end": v(444.29, 626.22) * mm});
            skLineSegment(sketch, "E681.0.2", {"start": v(444.29, 626.22) * mm, "end": v(461.08, 638.43) * mm});
            skLineSegment(sketch, "E681.0.3", {"start": v(461.08, 638.43) * mm, "end": v(440.32, 638.43) * mm});
            skLineSegment(sketch, "E681.0.4", {"start": v(440.32, 638.43) * mm, "end": v(433.9, 658.17) * mm});
            skLineSegment(sketch, "E681.0.5", {"start": v(433.9, 658.17) * mm, "end": v(427.5, 638.43) * mm});
            skLineSegment(sketch, "E681.0.6", {"start": v(427.5, 638.43) * mm, "end": v(406.73, 638.43) * mm});
            skLineSegment(sketch, "E681.0.7", {"start": v(406.73, 638.43) * mm, "end": v(423.53, 626.22) * mm});
            skLineSegment(sketch, "E681.0.8", {"start": v(423.53, 626.22) * mm, "end": v(417.11, 606.48) * mm});
            skLineSegment(sketch, "E681.0.9", {"start": v(417.11, 606.48) * mm, "end": v(433.9, 618.68) * mm});
            skLineSegment(sketch, "E682.0.0", {"start": v(43.4, 575.66) * mm, "end": v(60.19, 563.46) * mm});
            skLineSegment(sketch, "E682.0.1", {"start": v(60.19, 563.46) * mm, "end": v(53.77, 583.2) * mm});
            skLineSegment(sketch, "E682.0.2", {"start": v(53.77, 583.2) * mm, "end": v(70.57, 595.4) * mm});
            skLineSegment(sketch, "E682.0.3", {"start": v(70.57, 595.4) * mm, "end": v(49.8, 595.4) * mm});
            skLineSegment(sketch, "E682.0.4", {"start": v(49.8, 595.4) * mm, "end": v(43.4, 615.15) * mm});
            skLineSegment(sketch, "E682.0.5", {"start": v(43.4, 615.15) * mm, "end": v(36.98, 595.4) * mm});
            skLineSegment(sketch, "E682.0.6", {"start": v(36.98, 595.4) * mm, "end": v(16.21, 595.4) * mm});
            skLineSegment(sketch, "E682.0.7", {"start": v(16.21, 595.4) * mm, "end": v(33.01, 583.2) * mm});
            skLineSegment(sketch, "E682.0.8", {"start": v(33.01, 583.2) * mm, "end": v(26.6, 563.46) * mm});
            skLineSegment(sketch, "E682.0.9", {"start": v(26.6, 563.46) * mm, "end": v(43.4, 575.66) * mm});
            skLineSegment(sketch, "E683.0.0", {"start": v(130.17, 575.66) * mm, "end": v(146.97, 563.46) * mm});
            skLineSegment(sketch, "E683.0.1", {"start": v(146.97, 563.46) * mm, "end": v(140.55, 583.2) * mm});
            skLineSegment(sketch, "E683.0.2", {"start": v(140.55, 583.2) * mm, "end": v(157.35, 595.4) * mm});
            skLineSegment(sketch, "E683.0.3", {"start": v(157.35, 595.4) * mm, "end": v(136.59, 595.4) * mm});
            skLineSegment(sketch, "E683.0.4", {"start": v(136.59, 595.4) * mm, "end": v(130.17, 615.15) * mm});
            skLineSegment(sketch, "E683.0.5", {"start": v(130.17, 615.15) * mm, "end": v(123.76, 595.4) * mm});
            skLineSegment(sketch, "E683.0.6", {"start": v(123.76, 595.4) * mm, "end": v(103, 595.4) * mm});
            skLineSegment(sketch, "E683.0.7", {"start": v(103, 595.4) * mm, "end": v(119.8, 583.2) * mm});
            skLineSegment(sketch, "E683.0.8", {"start": v(119.8, 583.2) * mm, "end": v(113.38, 563.46) * mm});
            skLineSegment(sketch, "E683.0.9", {"start": v(113.38, 563.46) * mm, "end": v(130.17, 575.66) * mm});
            skLineSegment(sketch, "E684.0.0", {"start": v(86.78, 532.64) * mm, "end": v(103.58, 520.44) * mm});
            skLineSegment(sketch, "E684.0.1", {"start": v(103.58, 520.44) * mm, "end": v(97.16, 540.18) * mm});
            skLineSegment(sketch, "E684.0.2", {"start": v(97.16, 540.18) * mm, "end": v(113.96, 552.39) * mm});
            skLineSegment(sketch, "E684.0.3", {"start": v(113.96, 552.39) * mm, "end": v(93.2, 552.39) * mm});
            skLineSegment(sketch, "E684.0.4", {"start": v(93.2, 552.39) * mm, "end": v(86.78, 572.13) * mm});
            skLineSegment(sketch, "E684.0.5", {"start": v(86.78, 572.13) * mm, "end": v(80.37, 552.39) * mm});
            skLineSegment(sketch, "E684.0.6", {"start": v(80.37, 552.39) * mm, "end": v(59.6, 552.39) * mm});
            skLineSegment(sketch, "E684.0.7", {"start": v(59.6, 552.39) * mm, "end": v(76.4, 540.18) * mm});
            skLineSegment(sketch, "E684.0.8", {"start": v(76.4, 540.18) * mm, "end": v(69.99, 520.44) * mm});
            skLineSegment(sketch, "E684.0.9", {"start": v(69.99, 520.44) * mm, "end": v(86.78, 532.64) * mm});
            skLineSegment(sketch, "E685.0.0", {"start": v(43.4, 489.62) * mm, "end": v(60.19, 477.42) * mm});
            skLineSegment(sketch, "E685.0.1", {"start": v(60.19, 477.42) * mm, "end": v(53.77, 497.16) * mm});
            skLineSegment(sketch, "E685.0.2", {"start": v(53.77, 497.16) * mm, "end": v(70.57, 509.37) * mm});
            skLineSegment(sketch, "E685.0.3", {"start": v(70.57, 509.37) * mm, "end": v(49.8, 509.37) * mm});
            skLineSegment(sketch, "E685.0.4", {"start": v(49.8, 509.37) * mm, "end": v(43.4, 529.1) * mm});
            skLineSegment(sketch, "E685.0.5", {"start": v(43.4, 529.1) * mm, "end": v(36.98, 509.37) * mm});
            skLineSegment(sketch, "E685.0.6", {"start": v(36.98, 509.37) * mm, "end": v(16.21, 509.37) * mm});
            skLineSegment(sketch, "E685.0.7", {"start": v(16.21, 509.37) * mm, "end": v(33.01, 497.16) * mm});
            skLineSegment(sketch, "E685.0.8", {"start": v(33.01, 497.16) * mm, "end": v(26.6, 477.42) * mm});
            skLineSegment(sketch, "E685.0.9", {"start": v(26.6, 477.42) * mm, "end": v(43.4, 489.62) * mm});
            skLineSegment(sketch, "E686.0.0", {"start": v(86.78, 446.6) * mm, "end": v(103.58, 434.4) * mm});
            skLineSegment(sketch, "E686.0.1", {"start": v(103.58, 434.4) * mm, "end": v(97.16, 454.14) * mm});
            skLineSegment(sketch, "E686.0.2", {"start": v(97.16, 454.14) * mm, "end": v(113.96, 466.35) * mm});
            skLineSegment(sketch, "E686.0.3", {"start": v(113.96, 466.35) * mm, "end": v(93.2, 466.35) * mm});
            skLineSegment(sketch, "E686.0.4", {"start": v(93.2, 466.35) * mm, "end": v(86.78, 486.09) * mm});
            skLineSegment(sketch, "E686.0.5", {"start": v(86.78, 486.09) * mm, "end": v(80.37, 466.35) * mm});
            skLineSegment(sketch, "E686.0.6", {"start": v(80.37, 466.35) * mm, "end": v(59.6, 466.35) * mm});
            skLineSegment(sketch, "E686.0.7", {"start": v(59.6, 466.35) * mm, "end": v(76.4, 454.14) * mm});
            skLineSegment(sketch, "E686.0.8", {"start": v(76.4, 454.14) * mm, "end": v(69.99, 434.4) * mm});
            skLineSegment(sketch, "E686.0.9", {"start": v(69.99, 434.4) * mm, "end": v(86.78, 446.6) * mm});
            skLineSegment(sketch, "E687.0.0", {"start": v(43.4, 403.58) * mm, "end": v(60.19, 391.38) * mm});
            skLineSegment(sketch, "E687.0.1", {"start": v(60.19, 391.38) * mm, "end": v(53.77, 411.12) * mm});
            skLineSegment(sketch, "E687.0.2", {"start": v(53.77, 411.12) * mm, "end": v(70.57, 423.33) * mm});
            skLineSegment(sketch, "E687.0.3", {"start": v(70.57, 423.33) * mm, "end": v(49.8, 423.33) * mm});
            skLineSegment(sketch, "E687.0.4", {"start": v(49.8, 423.33) * mm, "end": v(43.4, 443.07) * mm});
            skLineSegment(sketch, "E687.0.5", {"start": v(43.4, 443.07) * mm, "end": v(36.98, 423.33) * mm});
            skLineSegment(sketch, "E687.0.6", {"start": v(36.98, 423.33) * mm, "end": v(16.21, 423.33) * mm});
            skLineSegment(sketch, "E687.0.7", {"start": v(16.21, 423.33) * mm, "end": v(33.01, 411.12) * mm});
            skLineSegment(sketch, "E687.0.8", {"start": v(33.01, 411.12) * mm, "end": v(26.6, 391.38) * mm});
            skLineSegment(sketch, "E687.0.9", {"start": v(26.6, 391.38) * mm, "end": v(43.4, 403.58) * mm});
            skLineSegment(sketch, "E688.0.0", {"start": v(130.17, 489.62) * mm, "end": v(146.97, 477.42) * mm});
            skLineSegment(sketch, "E688.0.1", {"start": v(146.97, 477.42) * mm, "end": v(140.55, 497.16) * mm});
            skLineSegment(sketch, "E688.0.2", {"start": v(140.55, 497.16) * mm, "end": v(157.35, 509.37) * mm});
            skLineSegment(sketch, "E688.0.3", {"start": v(157.35, 509.37) * mm, "end": v(136.59, 509.37) * mm});
            skLineSegment(sketch, "E688.0.4", {"start": v(136.59, 509.37) * mm, "end": v(130.17, 529.1) * mm});
            skLineSegment(sketch, "E688.0.5", {"start": v(130.17, 529.1) * mm, "end": v(123.76, 509.37) * mm});
            skLineSegment(sketch, "E688.0.6", {"start": v(123.76, 509.37) * mm, "end": v(103, 509.37) * mm});
            skLineSegment(sketch, "E688.0.7", {"start": v(103, 509.37) * mm, "end": v(119.8, 497.16) * mm});
            skLineSegment(sketch, "E688.0.8", {"start": v(119.8, 497.16) * mm, "end": v(113.38, 477.42) * mm});
            skLineSegment(sketch, "E688.0.9", {"start": v(113.38, 477.42) * mm, "end": v(130.17, 489.62) * mm});
            skLineSegment(sketch, "E689.0.0", {"start": v(130.17, 403.58) * mm, "end": v(146.97, 391.38) * mm});
            skLineSegment(sketch, "E689.0.1", {"start": v(146.97, 391.38) * mm, "end": v(140.55, 411.12) * mm});
            skLineSegment(sketch, "E689.0.2", {"start": v(140.55, 411.12) * mm, "end": v(157.35, 423.33) * mm});
            skLineSegment(sketch, "E689.0.3", {"start": v(157.35, 423.33) * mm, "end": v(136.59, 423.33) * mm});
            skLineSegment(sketch, "E689.0.4", {"start": v(136.59, 423.33) * mm, "end": v(130.17, 443.07) * mm});
            skLineSegment(sketch, "E689.0.5", {"start": v(130.17, 443.07) * mm, "end": v(123.76, 423.33) * mm});
            skLineSegment(sketch, "E689.0.6", {"start": v(123.76, 423.33) * mm, "end": v(103, 423.33) * mm});
            skLineSegment(sketch, "E689.0.7", {"start": v(103, 423.33) * mm, "end": v(119.8, 411.12) * mm});
            skLineSegment(sketch, "E689.0.8", {"start": v(119.8, 411.12) * mm, "end": v(113.38, 391.38) * mm});
            skLineSegment(sketch, "E689.0.9", {"start": v(113.38, 391.38) * mm, "end": v(130.17, 403.58) * mm});
            skLineSegment(sketch, "E690.0.0", {"start": v(216.95, 575.66) * mm, "end": v(233.75, 563.46) * mm});
            skLineSegment(sketch, "E690.0.1", {"start": v(233.75, 563.46) * mm, "end": v(227.33, 583.2) * mm});
            skLineSegment(sketch, "E690.0.2", {"start": v(227.33, 583.2) * mm, "end": v(244.13, 595.4) * mm});
            skLineSegment(sketch, "E690.0.3", {"start": v(244.13, 595.4) * mm, "end": v(223.37, 595.4) * mm});
            skLineSegment(sketch, "E690.0.4", {"start": v(223.37, 595.4) * mm, "end": v(216.95, 615.15) * mm});
            skLineSegment(sketch, "E690.0.5", {"start": v(216.95, 615.15) * mm, "end": v(210.54, 595.4) * mm});
            skLineSegment(sketch, "E690.0.6", {"start": v(210.54, 595.4) * mm, "end": v(189.78, 595.4) * mm});
            skLineSegment(sketch, "E690.0.7", {"start": v(189.78, 595.4) * mm, "end": v(206.57, 583.2) * mm});
            skLineSegment(sketch, "E690.0.8", {"start": v(206.57, 583.2) * mm, "end": v(200.16, 563.46) * mm});
            skLineSegment(sketch, "E690.0.9", {"start": v(200.16, 563.46) * mm, "end": v(216.95, 575.66) * mm});
            skLineSegment(sketch, "E691.0.0", {"start": v(173.56, 532.64) * mm, "end": v(190.36, 520.44) * mm});
            skLineSegment(sketch, "E691.0.1", {"start": v(190.36, 520.44) * mm, "end": v(183.94, 540.18) * mm});
            skLineSegment(sketch, "E691.0.2", {"start": v(183.94, 540.18) * mm, "end": v(200.74, 552.39) * mm});
            skLineSegment(sketch, "E691.0.3", {"start": v(200.74, 552.39) * mm, "end": v(179.98, 552.39) * mm});
            skLineSegment(sketch, "E691.0.4", {"start": v(179.98, 552.39) * mm, "end": v(173.56, 572.13) * mm});
            skLineSegment(sketch, "E691.0.5", {"start": v(173.56, 572.13) * mm, "end": v(167.15, 552.39) * mm});
            skLineSegment(sketch, "E691.0.6", {"start": v(167.15, 552.39) * mm, "end": v(146.39, 552.39) * mm});
            skLineSegment(sketch, "E691.0.7", {"start": v(146.39, 552.39) * mm, "end": v(163.18, 540.18) * mm});
            skLineSegment(sketch, "E691.0.8", {"start": v(163.18, 540.18) * mm, "end": v(156.77, 520.44) * mm});
            skLineSegment(sketch, "E691.0.9", {"start": v(156.77, 520.44) * mm, "end": v(173.56, 532.64) * mm});
            skLineSegment(sketch, "E692.0.0", {"start": v(173.56, 446.6) * mm, "end": v(190.36, 434.4) * mm});
            skLineSegment(sketch, "E692.0.1", {"start": v(190.36, 434.4) * mm, "end": v(183.94, 454.14) * mm});
            skLineSegment(sketch, "E692.0.2", {"start": v(183.94, 454.14) * mm, "end": v(200.74, 466.35) * mm});
            skLineSegment(sketch, "E692.0.3", {"start": v(200.74, 466.35) * mm, "end": v(179.98, 466.35) * mm});
            skLineSegment(sketch, "E692.0.4", {"start": v(179.98, 466.35) * mm, "end": v(173.56, 486.09) * mm});
            skLineSegment(sketch, "E692.0.5", {"start": v(173.56, 486.09) * mm, "end": v(167.15, 466.35) * mm});
            skLineSegment(sketch, "E692.0.6", {"start": v(167.15, 466.35) * mm, "end": v(146.39, 466.35) * mm});
            skLineSegment(sketch, "E692.0.7", {"start": v(146.39, 466.35) * mm, "end": v(163.18, 454.14) * mm});
            skLineSegment(sketch, "E692.0.8", {"start": v(163.18, 454.14) * mm, "end": v(156.77, 434.4) * mm});
            skLineSegment(sketch, "E692.0.9", {"start": v(156.77, 434.4) * mm, "end": v(173.56, 446.6) * mm});
            skLineSegment(sketch, "E693.0.0", {"start": v(216.95, 403.58) * mm, "end": v(233.75, 391.38) * mm});
            skLineSegment(sketch, "E693.0.1", {"start": v(233.75, 391.38) * mm, "end": v(227.33, 411.12) * mm});
            skLineSegment(sketch, "E693.0.2", {"start": v(227.33, 411.12) * mm, "end": v(244.13, 423.33) * mm});
            skLineSegment(sketch, "E693.0.3", {"start": v(244.13, 423.33) * mm, "end": v(223.37, 423.33) * mm});
            skLineSegment(sketch, "E693.0.4", {"start": v(223.37, 423.33) * mm, "end": v(216.95, 443.07) * mm});
            skLineSegment(sketch, "E693.0.5", {"start": v(216.95, 443.07) * mm, "end": v(210.54, 423.33) * mm});
            skLineSegment(sketch, "E693.0.6", {"start": v(210.54, 423.33) * mm, "end": v(189.78, 423.33) * mm});
            skLineSegment(sketch, "E693.0.7", {"start": v(189.78, 423.33) * mm, "end": v(206.57, 411.12) * mm});
            skLineSegment(sketch, "E693.0.8", {"start": v(206.57, 411.12) * mm, "end": v(200.16, 391.38) * mm});
            skLineSegment(sketch, "E693.0.9", {"start": v(200.16, 391.38) * mm, "end": v(216.95, 403.58) * mm});
            skLineSegment(sketch, "E694.0.0", {"start": v(260.34, 532.64) * mm, "end": v(277.14, 520.44) * mm});
            skLineSegment(sketch, "E694.0.1", {"start": v(277.14, 520.44) * mm, "end": v(270.73, 540.18) * mm});
            skLineSegment(sketch, "E694.0.2", {"start": v(270.73, 540.18) * mm, "end": v(287.52, 552.39) * mm});
            skLineSegment(sketch, "E694.0.3", {"start": v(287.52, 552.39) * mm, "end": v(266.76, 552.39) * mm});
            skLineSegment(sketch, "E694.0.4", {"start": v(266.76, 552.39) * mm, "end": v(260.34, 572.13) * mm});
            skLineSegment(sketch, "E694.0.5", {"start": v(260.34, 572.13) * mm, "end": v(253.93, 552.39) * mm});
            skLineSegment(sketch, "E694.0.6", {"start": v(253.93, 552.39) * mm, "end": v(233.17, 552.39) * mm});
            skLineSegment(sketch, "E694.0.7", {"start": v(233.17, 552.39) * mm, "end": v(249.96, 540.18) * mm});
            skLineSegment(sketch, "E694.0.8", {"start": v(249.96, 540.18) * mm, "end": v(243.55, 520.44) * mm});
            skLineSegment(sketch, "E694.0.9", {"start": v(243.55, 520.44) * mm, "end": v(260.34, 532.64) * mm});
            skLineSegment(sketch, "E695.0.0", {"start": v(303.74, 575.66) * mm, "end": v(320.53, 563.46) * mm});
            skLineSegment(sketch, "E695.0.1", {"start": v(320.53, 563.46) * mm, "end": v(314.12, 583.2) * mm});
            skLineSegment(sketch, "E695.0.2", {"start": v(314.12, 583.2) * mm, "end": v(330.91, 595.4) * mm});
            skLineSegment(sketch, "E695.0.3", {"start": v(330.91, 595.4) * mm, "end": v(310.15, 595.4) * mm});
            skLineSegment(sketch, "E695.0.4", {"start": v(310.15, 595.4) * mm, "end": v(303.74, 615.15) * mm});
            skLineSegment(sketch, "E695.0.5", {"start": v(303.74, 615.15) * mm, "end": v(297.32, 595.4) * mm});
            skLineSegment(sketch, "E695.0.6", {"start": v(297.32, 595.4) * mm, "end": v(276.56, 595.4) * mm});
            skLineSegment(sketch, "E695.0.7", {"start": v(276.56, 595.4) * mm, "end": v(293.36, 583.2) * mm});
            skLineSegment(sketch, "E695.0.8", {"start": v(293.36, 583.2) * mm, "end": v(286.94, 563.46) * mm});
            skLineSegment(sketch, "E695.0.9", {"start": v(286.94, 563.46) * mm, "end": v(303.74, 575.66) * mm});
            skLineSegment(sketch, "E696.0.0", {"start": v(260.34, 446.6) * mm, "end": v(277.14, 434.4) * mm});
            skLineSegment(sketch, "E696.0.1", {"start": v(277.14, 434.4) * mm, "end": v(270.73, 454.14) * mm});
            skLineSegment(sketch, "E696.0.2", {"start": v(270.73, 454.14) * mm, "end": v(287.52, 466.35) * mm});
            skLineSegment(sketch, "E696.0.3", {"start": v(287.52, 466.35) * mm, "end": v(266.76, 466.35) * mm});
            skLineSegment(sketch, "E696.0.4", {"start": v(266.76, 466.35) * mm, "end": v(260.34, 486.09) * mm});
            skLineSegment(sketch, "E696.0.5", {"start": v(260.34, 486.09) * mm, "end": v(253.93, 466.35) * mm});
            skLineSegment(sketch, "E696.0.6", {"start": v(253.93, 466.35) * mm, "end": v(233.17, 466.35) * mm});
            skLineSegment(sketch, "E696.0.7", {"start": v(233.17, 466.35) * mm, "end": v(249.96, 454.14) * mm});
            skLineSegment(sketch, "E696.0.8", {"start": v(249.96, 454.14) * mm, "end": v(243.55, 434.4) * mm});
            skLineSegment(sketch, "E696.0.9", {"start": v(243.55, 434.4) * mm, "end": v(260.34, 446.6) * mm});
            skLineSegment(sketch, "E697.0.0", {"start": v(303.74, 403.58) * mm, "end": v(320.53, 391.38) * mm});
            skLineSegment(sketch, "E697.0.1", {"start": v(320.53, 391.38) * mm, "end": v(314.12, 411.12) * mm});
            skLineSegment(sketch, "E697.0.2", {"start": v(314.12, 411.12) * mm, "end": v(330.91, 423.33) * mm});
            skLineSegment(sketch, "E697.0.3", {"start": v(330.91, 423.33) * mm, "end": v(310.15, 423.33) * mm});
            skLineSegment(sketch, "E697.0.4", {"start": v(310.15, 423.33) * mm, "end": v(303.74, 443.07) * mm});
            skLineSegment(sketch, "E697.0.5", {"start": v(303.74, 443.07) * mm, "end": v(297.32, 423.33) * mm});
            skLineSegment(sketch, "E697.0.6", {"start": v(297.32, 423.33) * mm, "end": v(276.56, 423.33) * mm});
            skLineSegment(sketch, "E697.0.7", {"start": v(276.56, 423.33) * mm, "end": v(293.36, 411.12) * mm});
            skLineSegment(sketch, "E697.0.8", {"start": v(293.36, 411.12) * mm, "end": v(286.94, 391.38) * mm});
            skLineSegment(sketch, "E697.0.9", {"start": v(286.94, 391.38) * mm, "end": v(303.74, 403.58) * mm});
            skLineSegment(sketch, "E698.0.0", {"start": v(347.13, 446.6) * mm, "end": v(363.92, 434.4) * mm});
            skLineSegment(sketch, "E698.0.1", {"start": v(363.92, 434.4) * mm, "end": v(357.5, 454.14) * mm});
            skLineSegment(sketch, "E698.0.2", {"start": v(357.5, 454.14) * mm, "end": v(374.3, 466.35) * mm});
            skLineSegment(sketch, "E698.0.3", {"start": v(374.3, 466.35) * mm, "end": v(353.54, 466.35) * mm});
            skLineSegment(sketch, "E698.0.4", {"start": v(353.54, 466.35) * mm, "end": v(347.13, 486.09) * mm});
            skLineSegment(sketch, "E698.0.5", {"start": v(347.13, 486.09) * mm, "end": v(340.71, 466.35) * mm});
            skLineSegment(sketch, "E698.0.6", {"start": v(340.71, 466.35) * mm, "end": v(319.95, 466.35) * mm});
            skLineSegment(sketch, "E698.0.7", {"start": v(319.95, 466.35) * mm, "end": v(336.75, 454.14) * mm});
            skLineSegment(sketch, "E698.0.8", {"start": v(336.75, 454.14) * mm, "end": v(330.33, 434.4) * mm});
            skLineSegment(sketch, "E698.0.9", {"start": v(330.33, 434.4) * mm, "end": v(347.13, 446.6) * mm});
            skLineSegment(sketch, "E699.0.0", {"start": v(216.95, 489.62) * mm, "end": v(233.75, 477.42) * mm});
            skLineSegment(sketch, "E699.0.1", {"start": v(233.75, 477.42) * mm, "end": v(227.33, 497.16) * mm});
            skLineSegment(sketch, "E699.0.2", {"start": v(227.33, 497.16) * mm, "end": v(244.13, 509.37) * mm});
            skLineSegment(sketch, "E699.0.3", {"start": v(244.13, 509.37) * mm, "end": v(223.37, 509.37) * mm});
            skLineSegment(sketch, "E699.0.4", {"start": v(223.37, 509.37) * mm, "end": v(216.95, 529.1) * mm});
            skLineSegment(sketch, "E699.0.5", {"start": v(216.95, 529.1) * mm, "end": v(210.54, 509.37) * mm});
            skLineSegment(sketch, "E699.0.6", {"start": v(210.54, 509.37) * mm, "end": v(189.78, 509.37) * mm});
            skLineSegment(sketch, "E699.0.7", {"start": v(189.78, 509.37) * mm, "end": v(206.57, 497.16) * mm});
            skLineSegment(sketch, "E699.0.8", {"start": v(206.57, 497.16) * mm, "end": v(200.16, 477.42) * mm});
            skLineSegment(sketch, "E699.0.9", {"start": v(200.16, 477.42) * mm, "end": v(216.95, 489.62) * mm});
            skLineSegment(sketch, "E700.0.0", {"start": v(303.74, 489.62) * mm, "end": v(320.53, 477.42) * mm});
            skLineSegment(sketch, "E700.0.1", {"start": v(320.53, 477.42) * mm, "end": v(314.12, 497.16) * mm});
            skLineSegment(sketch, "E700.0.2", {"start": v(314.12, 497.16) * mm, "end": v(330.91, 509.37) * mm});
            skLineSegment(sketch, "E700.0.3", {"start": v(330.91, 509.37) * mm, "end": v(310.15, 509.37) * mm});
            skLineSegment(sketch, "E700.0.4", {"start": v(310.15, 509.37) * mm, "end": v(303.74, 529.1) * mm});
            skLineSegment(sketch, "E700.0.5", {"start": v(303.74, 529.1) * mm, "end": v(297.32, 509.37) * mm});
            skLineSegment(sketch, "E700.0.6", {"start": v(297.32, 509.37) * mm, "end": v(276.56, 509.37) * mm});
            skLineSegment(sketch, "E700.0.7", {"start": v(276.56, 509.37) * mm, "end": v(293.36, 497.16) * mm});
            skLineSegment(sketch, "E700.0.8", {"start": v(293.36, 497.16) * mm, "end": v(286.94, 477.42) * mm});
            skLineSegment(sketch, "E700.0.9", {"start": v(286.94, 477.42) * mm, "end": v(303.74, 489.62) * mm});
            skLineSegment(sketch, "E701.0.0", {"start": v(347.13, 532.64) * mm, "end": v(363.92, 520.44) * mm});
            skLineSegment(sketch, "E701.0.1", {"start": v(363.92, 520.44) * mm, "end": v(357.5, 540.18) * mm});
            skLineSegment(sketch, "E701.0.2", {"start": v(357.5, 540.18) * mm, "end": v(374.3, 552.39) * mm});
            skLineSegment(sketch, "E701.0.3", {"start": v(374.3, 552.39) * mm, "end": v(353.54, 552.39) * mm});
            skLineSegment(sketch, "E701.0.4", {"start": v(353.54, 552.39) * mm, "end": v(347.13, 572.13) * mm});
            skLineSegment(sketch, "E701.0.5", {"start": v(347.13, 572.13) * mm, "end": v(340.71, 552.39) * mm});
            skLineSegment(sketch, "E701.0.6", {"start": v(340.71, 552.39) * mm, "end": v(319.95, 552.39) * mm});
            skLineSegment(sketch, "E701.0.7", {"start": v(319.95, 552.39) * mm, "end": v(336.75, 540.18) * mm});
            skLineSegment(sketch, "E701.0.8", {"start": v(336.75, 540.18) * mm, "end": v(330.33, 520.44) * mm});
            skLineSegment(sketch, "E701.0.9", {"start": v(330.33, 520.44) * mm, "end": v(347.13, 532.64) * mm});
            skLineSegment(sketch, "E702.0.0", {"start": v(390.52, 489.62) * mm, "end": v(407.31, 477.42) * mm});
            skLineSegment(sketch, "E702.0.1", {"start": v(407.31, 477.42) * mm, "end": v(400.9, 497.16) * mm});
            skLineSegment(sketch, "E702.0.2", {"start": v(400.9, 497.16) * mm, "end": v(417.7, 509.37) * mm});
            skLineSegment(sketch, "E702.0.3", {"start": v(417.7, 509.37) * mm, "end": v(396.93, 509.37) * mm});
            skLineSegment(sketch, "E702.0.4", {"start": v(396.93, 509.37) * mm, "end": v(390.52, 529.1) * mm});
            skLineSegment(sketch, "E702.0.5", {"start": v(390.52, 529.1) * mm, "end": v(384.1, 509.37) * mm});
            skLineSegment(sketch, "E702.0.6", {"start": v(384.1, 509.37) * mm, "end": v(363.34, 509.37) * mm});
            skLineSegment(sketch, "E702.0.7", {"start": v(363.34, 509.37) * mm, "end": v(380.14, 497.16) * mm});
            skLineSegment(sketch, "E702.0.8", {"start": v(380.14, 497.16) * mm, "end": v(373.72, 477.42) * mm});
            skLineSegment(sketch, "E702.0.9", {"start": v(373.72, 477.42) * mm, "end": v(390.52, 489.62) * mm});
            skLineSegment(sketch, "E703.0.0", {"start": v(433.9, 532.64) * mm, "end": v(450.7, 520.44) * mm});
            skLineSegment(sketch, "E703.0.1", {"start": v(450.7, 520.44) * mm, "end": v(444.29, 540.18) * mm});
            skLineSegment(sketch, "E703.0.2", {"start": v(444.29, 540.18) * mm, "end": v(461.08, 552.39) * mm});
            skLineSegment(sketch, "E703.0.3", {"start": v(461.08, 552.39) * mm, "end": v(440.32, 552.39) * mm});
            skLineSegment(sketch, "E703.0.4", {"start": v(440.32, 552.39) * mm, "end": v(433.9, 572.13) * mm});
            skLineSegment(sketch, "E703.0.5", {"start": v(433.9, 572.13) * mm, "end": v(427.5, 552.39) * mm});
            skLineSegment(sketch, "E703.0.6", {"start": v(427.5, 552.39) * mm, "end": v(406.73, 552.39) * mm});
            skLineSegment(sketch, "E703.0.7", {"start": v(406.73, 552.39) * mm, "end": v(423.53, 540.18) * mm});
            skLineSegment(sketch, "E703.0.8", {"start": v(423.53, 540.18) * mm, "end": v(417.11, 520.44) * mm});
            skLineSegment(sketch, "E703.0.9", {"start": v(417.11, 520.44) * mm, "end": v(433.9, 532.64) * mm});
            skLineSegment(sketch, "E704.0.0", {"start": v(477.3, 489.62) * mm, "end": v(494.1, 477.42) * mm});
            skLineSegment(sketch, "E704.0.1", {"start": v(494.1, 477.42) * mm, "end": v(487.68, 497.16) * mm});
            skLineSegment(sketch, "E704.0.2", {"start": v(487.68, 497.16) * mm, "end": v(504.48, 509.37) * mm});
            skLineSegment(sketch, "E704.0.3", {"start": v(504.48, 509.37) * mm, "end": v(483.71, 509.37) * mm});
            skLineSegment(sketch, "E704.0.4", {"start": v(483.71, 509.37) * mm, "end": v(477.3, 529.1) * mm});
            skLineSegment(sketch, "E704.0.5", {"start": v(477.3, 529.1) * mm, "end": v(470.88, 509.37) * mm});
            skLineSegment(sketch, "E704.0.6", {"start": v(470.88, 509.37) * mm, "end": v(450.12, 509.37) * mm});
            skLineSegment(sketch, "E704.0.7", {"start": v(450.12, 509.37) * mm, "end": v(466.92, 497.16) * mm});
            skLineSegment(sketch, "E704.0.8", {"start": v(466.92, 497.16) * mm, "end": v(460.5, 477.42) * mm});
            skLineSegment(sketch, "E704.0.9", {"start": v(460.5, 477.42) * mm, "end": v(477.3, 489.62) * mm});
            skLineSegment(sketch, "E705.0.0", {"start": v(433.9, 446.6) * mm, "end": v(450.7, 434.4) * mm});
            skLineSegment(sketch, "E705.0.1", {"start": v(450.7, 434.4) * mm, "end": v(444.29, 454.14) * mm});
            skLineSegment(sketch, "E705.0.2", {"start": v(444.29, 454.14) * mm, "end": v(461.08, 466.35) * mm});
            skLineSegment(sketch, "E705.0.3", {"start": v(461.08, 466.35) * mm, "end": v(440.32, 466.35) * mm});
            skLineSegment(sketch, "E705.0.4", {"start": v(440.32, 466.35) * mm, "end": v(433.9, 486.09) * mm});
            skLineSegment(sketch, "E705.0.5", {"start": v(433.9, 486.09) * mm, "end": v(427.5, 466.35) * mm});
            skLineSegment(sketch, "E705.0.6", {"start": v(427.5, 466.35) * mm, "end": v(406.73, 466.35) * mm});
            skLineSegment(sketch, "E705.0.7", {"start": v(406.73, 466.35) * mm, "end": v(423.53, 454.14) * mm});
            skLineSegment(sketch, "E705.0.8", {"start": v(423.53, 454.14) * mm, "end": v(417.11, 434.4) * mm});
            skLineSegment(sketch, "E705.0.9", {"start": v(417.11, 434.4) * mm, "end": v(433.9, 446.6) * mm});
            skLineSegment(sketch, "E706.0.0", {"start": v(390.52, 575.66) * mm, "end": v(407.31, 563.46) * mm});
            skLineSegment(sketch, "E706.0.1", {"start": v(407.31, 563.46) * mm, "end": v(400.9, 583.2) * mm});
            skLineSegment(sketch, "E706.0.2", {"start": v(400.9, 583.2) * mm, "end": v(417.7, 595.4) * mm});
            skLineSegment(sketch, "E706.0.3", {"start": v(417.7, 595.4) * mm, "end": v(396.93, 595.4) * mm});
            skLineSegment(sketch, "E706.0.4", {"start": v(396.93, 595.4) * mm, "end": v(390.52, 615.15) * mm});
            skLineSegment(sketch, "E706.0.5", {"start": v(390.52, 615.15) * mm, "end": v(384.1, 595.4) * mm});
            skLineSegment(sketch, "E706.0.6", {"start": v(384.1, 595.4) * mm, "end": v(363.34, 595.4) * mm});
            skLineSegment(sketch, "E706.0.7", {"start": v(363.34, 595.4) * mm, "end": v(380.14, 583.2) * mm});
            skLineSegment(sketch, "E706.0.8", {"start": v(380.14, 583.2) * mm, "end": v(373.72, 563.46) * mm});
            skLineSegment(sketch, "E706.0.9", {"start": v(373.72, 563.46) * mm, "end": v(390.52, 575.66) * mm});
            skLineSegment(sketch, "E707.0.0", {"start": v(477.3, 575.66) * mm, "end": v(494.1, 563.46) * mm});
            skLineSegment(sketch, "E707.0.1", {"start": v(494.1, 563.46) * mm, "end": v(487.68, 583.2) * mm});
            skLineSegment(sketch, "E707.0.2", {"start": v(487.68, 583.2) * mm, "end": v(504.48, 595.4) * mm});
            skLineSegment(sketch, "E707.0.3", {"start": v(504.48, 595.4) * mm, "end": v(483.71, 595.4) * mm});
            skLineSegment(sketch, "E707.0.4", {"start": v(483.71, 595.4) * mm, "end": v(477.3, 615.15) * mm});
            skLineSegment(sketch, "E707.0.5", {"start": v(477.3, 615.15) * mm, "end": v(470.88, 595.4) * mm});
            skLineSegment(sketch, "E707.0.6", {"start": v(470.88, 595.4) * mm, "end": v(450.12, 595.4) * mm});
            skLineSegment(sketch, "E707.0.7", {"start": v(450.12, 595.4) * mm, "end": v(466.92, 583.2) * mm});
            skLineSegment(sketch, "E707.0.8", {"start": v(466.92, 583.2) * mm, "end": v(460.5, 563.46) * mm});
            skLineSegment(sketch, "E707.0.9", {"start": v(460.5, 563.46) * mm, "end": v(477.3, 575.66) * mm});
            skLineSegment(sketch, "E708.0.0", {"start": v(390.52, 403.58) * mm, "end": v(407.31, 391.38) * mm});
            skLineSegment(sketch, "E708.0.1", {"start": v(407.31, 391.38) * mm, "end": v(400.9, 411.12) * mm});
            skLineSegment(sketch, "E708.0.2", {"start": v(400.9, 411.12) * mm, "end": v(417.7, 423.33) * mm});
            skLineSegment(sketch, "E708.0.3", {"start": v(417.7, 423.33) * mm, "end": v(396.93, 423.33) * mm});
            skLineSegment(sketch, "E708.0.4", {"start": v(396.93, 423.33) * mm, "end": v(390.52, 443.07) * mm});
            skLineSegment(sketch, "E708.0.5", {"start": v(390.52, 443.07) * mm, "end": v(384.1, 423.33) * mm});
            skLineSegment(sketch, "E708.0.6", {"start": v(384.1, 423.33) * mm, "end": v(363.34, 423.33) * mm});
            skLineSegment(sketch, "E708.0.7", {"start": v(363.34, 423.33) * mm, "end": v(380.14, 411.12) * mm});
            skLineSegment(sketch, "E708.0.8", {"start": v(380.14, 411.12) * mm, "end": v(373.72, 391.38) * mm});
            skLineSegment(sketch, "E708.0.9", {"start": v(373.72, 391.38) * mm, "end": v(390.52, 403.58) * mm});
            skLineSegment(sketch, "E709.0.0", {"start": v(477.3, 403.58) * mm, "end": v(494.1, 391.38) * mm});
            skLineSegment(sketch, "E709.0.1", {"start": v(494.1, 391.38) * mm, "end": v(487.68, 411.12) * mm});
            skLineSegment(sketch, "E709.0.2", {"start": v(487.68, 411.12) * mm, "end": v(504.48, 423.33) * mm});
            skLineSegment(sketch, "E709.0.3", {"start": v(504.48, 423.33) * mm, "end": v(483.71, 423.33) * mm});
            skLineSegment(sketch, "E709.0.4", {"start": v(483.71, 423.33) * mm, "end": v(477.3, 443.07) * mm});
            skLineSegment(sketch, "E709.0.5", {"start": v(477.3, 443.07) * mm, "end": v(470.88, 423.33) * mm});
            skLineSegment(sketch, "E709.0.6", {"start": v(470.88, 423.33) * mm, "end": v(450.12, 423.33) * mm});
            skLineSegment(sketch, "E709.0.7", {"start": v(450.12, 423.33) * mm, "end": v(466.92, 411.12) * mm});
            skLineSegment(sketch, "E709.0.8", {"start": v(466.92, 411.12) * mm, "end": v(460.5, 391.38) * mm});
            skLineSegment(sketch, "E709.0.9", {"start": v(460.5, 391.38) * mm, "end": v(477.3, 403.58) * mm});
            skSolve(sketch);
        }
        {
            var Q0;
            Q0=makeQuery(id+"F0.imprint","IMPRINT",FACE,{"disambiguationData":[TD([[makeQuery(id+"F0.imprint","IMPRINT",EDGE,{"derivedFrom":sQuery(id+"F0.wireOp",EDGE,"E1.0.4.0")}),-1.0]])]});
            var Q1;
            Q1=makeQuery(id+"F0.imprint","IMPRINT",FACE,{"disambiguationData":[TD([[makeQuery(id+"F0.imprint","IMPRINT",EDGE,{"derivedFrom":sQuery(id+"F0.wireOp",EDGE,"E1.0.3.0")}),-1.0]])]});
            var Q2;
            Q2=makeQuery(id+"F0.imprint","IMPRINT",FACE,{"disambiguationData":[TD([[makeQuery(id+"F0.imprint","IMPRINT",EDGE,{"derivedFrom":sQuery(id+"F0.wireOp",EDGE,"E1.0.2.0")}),-1.0]])]});
            var Q3;
            Q3=makeQuery(id+"F0.imprint","IMPRINT",FACE,{"disambiguationData":[TD([[makeQuery(id+"F0.imprint","IMPRINT",EDGE,{"derivedFrom":sQuery(id+"F0.wireOp",EDGE,"E1.0.1.0")}),-1.0]])]});
            var Q4;
            Q4=makeQuery(id+"F0.imprint","IMPRINT",FACE,{"disambiguationData":[TD([[makeQuery(id+"F0.imprint","IMPRINT",EDGE,{"derivedFrom":sQuery(id+"F0.wireOp",EDGE,"E0.bottom")}),1.0]])]});
            var Q5;
            Q5=makeQuery(id+"F0.imprint","IMPRINT",FACE,{"disambiguationData":[TD([[makeQuery(id+"F0.imprint","IMPRINT",EDGE,{"derivedFrom":sQuery(id+"F0.wireOp",EDGE,"E1.0.5.0")}),-1.0]])]});
            var Q6;
            Q6=makeQuery(id+"F0.imprint","IMPRINT",FACE,{"disambiguationData":[TD([[makeQuery(id+"F0.imprint","IMPRINT",EDGE,{"derivedFrom":sQuery(id+"F0.wireOp",EDGE,"E2.bottom")}),1.0]])]});
            var Q7;
            Q7=makeQuery(id+"F0.imprint","IMPRINT",FACE,{"disambiguationData":[TD([[makeQuery(id+"F0.imprint","IMPRINT",EDGE,{"derivedFrom":sQuery(id+"F0.wireOp",EDGE,"E3.0.1.0")}),-1.0]])]});
            var Q8;
            Q8=makeQuery(id+"F0.imprint","IMPRINT",FACE,{"disambiguationData":[TD([[makeQuery(id+"F0.imprint","IMPRINT",EDGE,{"derivedFrom":sQuery(id+"F0.wireOp",EDGE,"E3.0.2.0")}),-1.0]])]});
            var Q9;
            Q9=makeQuery(id+"F0.imprint","IMPRINT",FACE,{"disambiguationData":[TD([[makeQuery(id+"F0.imprint","IMPRINT",EDGE,{"derivedFrom":sQuery(id+"F0.wireOp",EDGE,"E3.0.3.0")}),-1.0]])]});
            var Q10;
            Q10=makeQuery(id+"F0.imprint","IMPRINT",FACE,{"disambiguationData":[TD([[makeQuery(id+"F0.imprint","IMPRINT",EDGE,{"derivedFrom":sQuery(id+"F0.wireOp",EDGE,"E3.0.4.0")}),-1.0]])]});
            var Q11;
            Q11=makeQuery(id+"F0.imprint","IMPRINT",FACE,{"disambiguationData":[TD([[makeQuery(id+"F0.imprint","IMPRINT",EDGE,{"derivedFrom":sQuery(id+"F0.wireOp",EDGE,"E3.0.5.0")}),-1.0]])]});
            var Q12;
            Q12=makeQuery(id+"F0.imprint","IMPRINT",FACE,{"disambiguationData":[TD([[makeQuery(id+"F0.imprint","IMPRINT",EDGE,{"derivedFrom":sQuery(id+"F0.wireOp",EDGE,"E3.0.6.0")}),-1.0]])]});
            var Q13;
            Q13=makeQuery(id+"F0.imprint","IMPRINT",FACE,{"disambiguationData":[TD([[makeQuery(id+"F0.imprint","IMPRINT",EDGE,{"derivedFrom":sQuery(id+"F0.wireOp",EDGE,"4ZhGCmB5-MOtP-mJGD-FZ2T-YXOS8dpUORbb")}),-1.0]])]});
            var Q14;
            Q14=makeQuery(id+"F0.imprint","IMPRINT",FACE,{"disambiguationData":[TD([[makeQuery(id+"F0.imprint","IMPRINT",EDGE,{"derivedFrom":sQuery(id+"F0.wireOp",EDGE,"RfoXv4qA-jOX3-Eiq5-o1QQ-7IePg94zmo7s")}),1.0]])]});
            var Q15;
            Q15=makeQuery(id+"F0.imprint","IMPRINT",FACE,{"disambiguationData":[TD([[makeQuery(id+"F0.imprint","IMPRINT",EDGE,{"derivedFrom":sQuery(id+"F0.wireOp",EDGE,"E12")}),1.0]])]});
            var Q16;
            Q16=makeQuery(id+"F0.imprint","IMPRINT",FACE,{"disambiguationData":[TD([[makeQuery(id+"F0.imprint","IMPRINT",EDGE,{"derivedFrom":sQuery(id+"F0.wireOp",EDGE,"E10")}),-1.0]])]});
            var Q17;
            Q17=makeQuery(id+"F0.imprint","IMPRINT",FACE,{"disambiguationData":[TD([[makeQuery(id+"F0.imprint","IMPRINT",EDGE,{"derivedFrom":sQuery(id+"F0.wireOp",EDGE,"E8")}),1.0]])]});
            var Q18;
            Q18=makeQuery(id+"F0.imprint","IMPRINT",FACE,{"disambiguationData":[TD([[makeQuery(id+"F0.imprint","IMPRINT",EDGE,{"derivedFrom":sQuery(id+"F0.wireOp",EDGE,"E6")}),1.0]])]});
            var Q19;
            Q19=makeQuery(id+"F0.imprint","IMPRINT",FACE,{"disambiguationData":[TD([[makeQuery(id+"F0.imprint","IMPRINT",EDGE,{"derivedFrom":sQuery(id+"F0.wireOp",EDGE,"E4")}),1.0]])]});
            var Q20;
            Q20=makeQuery(id+"F0.imprint","IMPRINT",FACE,{"disambiguationData":[TD([[makeQuery(id+"F0.imprint","IMPRINT",EDGE,{"derivedFrom":sQuery(id+"F0.wireOp",EDGE,"E23")}),-1.0]])]});
            var Q21;
            Q21=makeQuery(id+"F0.imprint","IMPRINT",FACE,{"disambiguationData":[TD([[makeQuery(id+"F0.imprint","IMPRINT",EDGE,{"derivedFrom":sQuery(id+"F0.wireOp",EDGE,"E25")}),1.0]])]});
            var Q22;
            Q22=makeQuery(id+"F0.imprint","IMPRINT",FACE,{"disambiguationData":[TD([[makeQuery(id+"F0.imprint","IMPRINT",EDGE,{"derivedFrom":sQuery(id+"F0.wireOp",EDGE,"E27")}),-1.0]])]});
            var Q23;
            Q23=makeQuery(id+"F0.imprint","IMPRINT",FACE,{"disambiguationData":[TD([[makeQuery(id+"F0.imprint","IMPRINT",EDGE,{"derivedFrom":sQuery(id+"F0.wireOp",EDGE,"E29")}),-1.0]])]});
            var Q24;
            Q24=makeQuery(id+"F0.imprint","IMPRINT",FACE,{"disambiguationData":[TD([[makeQuery(id+"F0.imprint","IMPRINT",EDGE,{"derivedFrom":sQuery(id+"F0.wireOp",EDGE,"E31")}),-1.0]])]});
            extrude(context, id + "F3", {"entities" : qUnion([Q0, Q1, Q2, Q3, Q4, Q5, Q6, Q7, Q8, Q9, Q10, Q11, Q12, Q13, Q14, Q15, Q16, Q17, Q18, Q19, Q20, Q21, Q22, Q23, Q24]), "depth" : 12.7 * mm});
        }
        {
            var Q0;
            Q0=makeQuery(id+"F2.imprint","IMPRINT",FACE,{"disambiguationData":[TD([[makeQuery(id+"F2.imprint","IMPRINT",EDGE,{"derivedFrom":sQuery(id+"F2.wireOp",EDGE,"E677.0.0")}),1.0]])]});
            var Q1;
            Q1=makeQuery(id+"F2.imprint","IMPRINT",FACE,{"disambiguationData":[TD([[makeQuery(id+"F2.imprint","IMPRINT",EDGE,{"derivedFrom":sQuery(id+"F2.wireOp",EDGE,"E660.0.0")}),1.0]])]});
            var Q2;
            Q2=makeQuery(id+"F2.imprint","IMPRINT",FACE,{"disambiguationData":[TD([[makeQuery(id+"F2.imprint","IMPRINT",EDGE,{"derivedFrom":sQuery(id+"F2.wireOp",EDGE,"E661.0.0")}),1.0]])]});
            var Q3;
            Q3=makeQuery(id+"F2.imprint","IMPRINT",FACE,{"disambiguationData":[TD([[makeQuery(id+"F2.imprint","IMPRINT",EDGE,{"derivedFrom":sQuery(id+"F2.wireOp",EDGE,"E662.0.0")}),1.0]])]});
            var Q4;
            Q4=makeQuery(id+"F2.imprint","IMPRINT",FACE,{"disambiguationData":[TD([[makeQuery(id+"F2.imprint","IMPRINT",EDGE,{"derivedFrom":sQuery(id+"F2.wireOp",EDGE,"E663.0.0")}),1.0]])]});
            var Q5;
            Q5=makeQuery(id+"F2.imprint","IMPRINT",FACE,{"disambiguationData":[TD([[makeQuery(id+"F2.imprint","IMPRINT",EDGE,{"derivedFrom":sQuery(id+"F2.wireOp",EDGE,"E664.0.0")}),1.0]])]});
            var Q6;
            Q6=makeQuery(id+"F2.imprint","IMPRINT",FACE,{"disambiguationData":[TD([[makeQuery(id+"F2.imprint","IMPRINT",EDGE,{"derivedFrom":sQuery(id+"F2.wireOp",EDGE,"E665.0.0")}),1.0]])]});
            var Q7;
            Q7=makeQuery(id+"F2.imprint","IMPRINT",FACE,{"disambiguationData":[TD([[makeQuery(id+"F2.imprint","IMPRINT",EDGE,{"derivedFrom":sQuery(id+"F2.wireOp",EDGE,"E676.0.0")}),1.0]])]});
            var Q8;
            Q8=makeQuery(id+"F2.imprint","IMPRINT",FACE,{"disambiguationData":[TD([[makeQuery(id+"F2.imprint","IMPRINT",EDGE,{"derivedFrom":sQuery(id+"F2.wireOp",EDGE,"E666.0.0")}),1.0]])]});
            var Q9;
            Q9=makeQuery(id+"F2.imprint","IMPRINT",FACE,{"disambiguationData":[TD([[makeQuery(id+"F2.imprint","IMPRINT",EDGE,{"derivedFrom":sQuery(id+"F2.wireOp",EDGE,"E672.0.0")}),1.0]])]});
            var Q10;
            Q10=makeQuery(id+"F2.imprint","IMPRINT",FACE,{"disambiguationData":[TD([[makeQuery(id+"F2.imprint","IMPRINT",EDGE,{"derivedFrom":sQuery(id+"F2.wireOp",EDGE,"E691.0.0")}),1.0]])]});
            var Q11;
            Q11=makeQuery(id+"F2.imprint","IMPRINT",FACE,{"disambiguationData":[TD([[makeQuery(id+"F2.imprint","IMPRINT",EDGE,{"derivedFrom":sQuery(id+"F2.wireOp",EDGE,"E671.0.0")}),1.0]])]});
            var Q12;
            Q12=makeQuery(id+"F2.imprint","IMPRINT",FACE,{"disambiguationData":[TD([[makeQuery(id+"F2.imprint","IMPRINT",EDGE,{"derivedFrom":sQuery(id+"F2.wireOp",EDGE,"E699.0.0")}),1.0]])]});
            var Q13;
            Q13=makeQuery(id+"F2.imprint","IMPRINT",FACE,{"disambiguationData":[TD([[makeQuery(id+"F2.imprint","IMPRINT",EDGE,{"derivedFrom":sQuery(id+"F2.wireOp",EDGE,"E707.0.0")}),1.0]])]});
            var Q14;
            Q14=makeQuery(id+"F2.imprint","IMPRINT",FACE,{"disambiguationData":[TD([[makeQuery(id+"F2.imprint","IMPRINT",EDGE,{"derivedFrom":sQuery(id+"F2.wireOp",EDGE,"E705.0.0")}),1.0]])]});
            var Q15;
            Q15=makeQuery(id+"F2.imprint","IMPRINT",FACE,{"disambiguationData":[TD([[makeQuery(id+"F2.imprint","IMPRINT",EDGE,{"derivedFrom":sQuery(id+"F2.wireOp",EDGE,"E689.0.0")}),1.0]])]});
            var Q16;
            Q16=makeQuery(id+"F2.imprint","IMPRINT",FACE,{"disambiguationData":[TD([[makeQuery(id+"F2.imprint","IMPRINT",EDGE,{"derivedFrom":sQuery(id+"F2.wireOp",EDGE,"E675.0.0")}),1.0]])]});
            var Q17;
            Q17=makeQuery(id+"F2.imprint","IMPRINT",FACE,{"disambiguationData":[TD([[makeQuery(id+"F2.imprint","IMPRINT",EDGE,{"derivedFrom":sQuery(id+"F2.wireOp",EDGE,"E673.0.0")}),1.0]])]});
            var Q18;
            Q18=makeQuery(id+"F2.imprint","IMPRINT",FACE,{"disambiguationData":[TD([[makeQuery(id+"F2.imprint","IMPRINT",EDGE,{"derivedFrom":sQuery(id+"F2.wireOp",EDGE,"E674.0.0")}),1.0]])]});
            var Q19;
            Q19=makeQuery(id+"F2.imprint","IMPRINT",FACE,{"disambiguationData":[TD([[makeQuery(id+"F2.imprint","IMPRINT",EDGE,{"derivedFrom":sQuery(id+"F2.wireOp",EDGE,"E668.0.0")}),1.0]])]});
            var Q20;
            Q20=makeQuery(id+"F2.imprint","IMPRINT",FACE,{"disambiguationData":[TD([[makeQuery(id+"F2.imprint","IMPRINT",EDGE,{"derivedFrom":sQuery(id+"F2.wireOp",EDGE,"E667.0.0")}),1.0]])]});
            var Q21;
            Q21=makeQuery(id+"F2.imprint","IMPRINT",FACE,{"disambiguationData":[TD([[makeQuery(id+"F2.imprint","IMPRINT",EDGE,{"derivedFrom":sQuery(id+"F2.wireOp",EDGE,"E669.0.0")}),1.0]])]});
            var Q22;
            Q22=makeQuery(id+"F2.imprint","IMPRINT",FACE,{"disambiguationData":[TD([[makeQuery(id+"F2.imprint","IMPRINT",EDGE,{"derivedFrom":sQuery(id+"F2.wireOp",EDGE,"E706.0.0")}),1.0]])]});
            var Q23;
            Q23=makeQuery(id+"F2.imprint","IMPRINT",FACE,{"disambiguationData":[TD([[makeQuery(id+"F2.imprint","IMPRINT",EDGE,{"derivedFrom":sQuery(id+"F2.wireOp",EDGE,"E690.0.0")}),1.0]])]});
            var Q24;
            Q24=makeQuery(id+"F2.imprint","IMPRINT",FACE,{"disambiguationData":[TD([[makeQuery(id+"F2.imprint","IMPRINT",EDGE,{"derivedFrom":sQuery(id+"F2.wireOp",EDGE,"E670.0.0")}),1.0]])]});
            var Q25;
            Q25=makeQuery(id+"F2.imprint","IMPRINT",FACE,{"disambiguationData":[TD([[makeQuery(id+"F2.imprint","IMPRINT",EDGE,{"derivedFrom":sQuery(id+"F2.wireOp",EDGE,"E704.0.0")}),1.0]])]});
            var Q26;
            Q26=makeQuery(id+"F2.imprint","IMPRINT",FACE,{"disambiguationData":[TD([[makeQuery(id+"F2.imprint","IMPRINT",EDGE,{"derivedFrom":sQuery(id+"F2.wireOp",EDGE,"E703.0.0")}),1.0]])]});
            var Q27;
            Q27=makeQuery(id+"F2.imprint","IMPRINT",FACE,{"disambiguationData":[TD([[makeQuery(id+"F2.imprint","IMPRINT",EDGE,{"derivedFrom":sQuery(id+"F2.wireOp",EDGE,"E688.0.0")}),1.0]])]});
            var Q28;
            Q28=makeQuery(id+"F2.imprint","IMPRINT",FACE,{"disambiguationData":[TD([[makeQuery(id+"F2.imprint","IMPRINT",EDGE,{"derivedFrom":sQuery(id+"F2.wireOp",EDGE,"E687.0.0")}),1.0]])]});
            var Q29;
            Q29=makeQuery(id+"F2.imprint","IMPRINT",FACE,{"disambiguationData":[TD([[makeQuery(id+"F2.imprint","IMPRINT",EDGE,{"derivedFrom":sQuery(id+"F2.wireOp",EDGE,"E701.0.0")}),1.0]])]});
            var Q30;
            Q30=makeQuery(id+"F2.imprint","IMPRINT",FACE,{"disambiguationData":[TD([[makeQuery(id+"F2.imprint","IMPRINT",EDGE,{"derivedFrom":sQuery(id+"F2.wireOp",EDGE,"E702.0.0")}),1.0]])]});
            var Q31;
            Q31=makeQuery(id+"F2.imprint","IMPRINT",FACE,{"disambiguationData":[TD([[makeQuery(id+"F2.imprint","IMPRINT",EDGE,{"derivedFrom":sQuery(id+"F2.wireOp",EDGE,"E686.0.0")}),1.0]])]});
            var Q32;
            Q32=makeQuery(id+"F2.imprint","IMPRINT",FACE,{"disambiguationData":[TD([[makeQuery(id+"F2.imprint","IMPRINT",EDGE,{"derivedFrom":sQuery(id+"F2.wireOp",EDGE,"E700.0.0")}),1.0]])]});
            var Q33;
            Q33=makeQuery(id+"F2.imprint","IMPRINT",FACE,{"disambiguationData":[TD([[makeQuery(id+"F2.imprint","IMPRINT",EDGE,{"derivedFrom":sQuery(id+"F2.wireOp",EDGE,"E683.0.0")}),1.0]])]});
            var Q34;
            Q34=makeQuery(id+"F2.imprint","IMPRINT",FACE,{"disambiguationData":[TD([[makeQuery(id+"F2.imprint","IMPRINT",EDGE,{"derivedFrom":sQuery(id+"F2.wireOp",EDGE,"E685.0.0")}),1.0]])]});
            var Q35;
            Q35=makeQuery(id+"F2.imprint","IMPRINT",FACE,{"disambiguationData":[TD([[makeQuery(id+"F2.imprint","IMPRINT",EDGE,{"derivedFrom":sQuery(id+"F2.wireOp",EDGE,"E684.0.0")}),1.0]])]});
            var Q36;
            Q36=makeQuery(id+"F2.imprint","IMPRINT",FACE,{"disambiguationData":[TD([[makeQuery(id+"F2.imprint","IMPRINT",EDGE,{"derivedFrom":sQuery(id+"F2.wireOp",EDGE,"E698.0.0")}),1.0]])]});
            var Q37;
            Q37=makeQuery(id+"F2.imprint","IMPRINT",FACE,{"disambiguationData":[TD([[makeQuery(id+"F2.imprint","IMPRINT",EDGE,{"derivedFrom":sQuery(id+"F2.wireOp",EDGE,"E682.0.0")}),1.0]])]});
            var Q38;
            Q38=makeQuery(id+"F2.imprint","IMPRINT",FACE,{"disambiguationData":[TD([[makeQuery(id+"F2.imprint","IMPRINT",EDGE,{"derivedFrom":sQuery(id+"F2.wireOp",EDGE,"E681.0.0")}),1.0]])]});
            var Q39;
            Q39=makeQuery(id+"F2.imprint","IMPRINT",FACE,{"disambiguationData":[TD([[makeQuery(id+"F2.imprint","IMPRINT",EDGE,{"derivedFrom":sQuery(id+"F2.wireOp",EDGE,"E697.0.0")}),1.0]])]});
            var Q40;
            Q40=makeQuery(id+"F2.imprint","IMPRINT",FACE,{"disambiguationData":[TD([[makeQuery(id+"F2.imprint","IMPRINT",EDGE,{"derivedFrom":sQuery(id+"F2.wireOp",EDGE,"E680.0.0")}),1.0]])]});
            var Q41;
            Q41=makeQuery(id+"F2.imprint","IMPRINT",FACE,{"disambiguationData":[TD([[makeQuery(id+"F2.imprint","IMPRINT",EDGE,{"derivedFrom":sQuery(id+"F2.wireOp",EDGE,"E696.0.0")}),1.0]])]});
            var Q42;
            Q42=makeQuery(id+"F2.imprint","IMPRINT",FACE,{"disambiguationData":[TD([[makeQuery(id+"F2.imprint","IMPRINT",EDGE,{"derivedFrom":sQuery(id+"F2.wireOp",EDGE,"E679.0.0")}),1.0]])]});
            var Q43;
            Q43=makeQuery(id+"F2.imprint","IMPRINT",FACE,{"disambiguationData":[TD([[makeQuery(id+"F2.imprint","IMPRINT",EDGE,{"derivedFrom":sQuery(id+"F2.wireOp",EDGE,"E695.0.0")}),1.0]])]});
            var Q44;
            Q44=makeQuery(id+"F2.imprint","IMPRINT",FACE,{"disambiguationData":[TD([[makeQuery(id+"F2.imprint","IMPRINT",EDGE,{"derivedFrom":sQuery(id+"F2.wireOp",EDGE,"E678.0.0")}),1.0]])]});
            var Q45;
            Q45=makeQuery(id+"F2.imprint","IMPRINT",FACE,{"disambiguationData":[TD([[makeQuery(id+"F2.imprint","IMPRINT",EDGE,{"derivedFrom":sQuery(id+"F2.wireOp",EDGE,"E694.0.0")}),1.0]])]});
            var Q46;
            Q46=makeQuery(id+"F2.imprint","IMPRINT",FACE,{"disambiguationData":[TD([[makeQuery(id+"F2.imprint","IMPRINT",EDGE,{"derivedFrom":sQuery(id+"F2.wireOp",EDGE,"E693.0.0")}),1.0]])]});
            var Q47;
            Q47=makeQuery(id+"F2.imprint","IMPRINT",FACE,{"disambiguationData":[TD([[makeQuery(id+"F2.imprint","IMPRINT",EDGE,{"derivedFrom":sQuery(id+"F2.wireOp",EDGE,"E709.0.0")}),1.0]])]});
            var Q48;
            Q48=makeQuery(id+"F2.imprint","IMPRINT",FACE,{"disambiguationData":[TD([[makeQuery(id+"F2.imprint","IMPRINT",EDGE,{"derivedFrom":sQuery(id+"F2.wireOp",EDGE,"E692.0.0")}),1.0]])]});
            var Q49;
            Q49=makeQuery(id+"F2.imprint","IMPRINT",FACE,{"disambiguationData":[TD([[makeQuery(id+"F2.imprint","IMPRINT",EDGE,{"derivedFrom":sQuery(id+"F2.wireOp",EDGE,"E708.0.0")}),1.0]])]});
            extrude(context, id + "F4", {"entities" : qUnion([Q0, Q1, Q2, Q3, Q4, Q5, Q6, Q7, Q8, Q9, Q10, Q11, Q12, Q13, Q14, Q15, Q16, Q17, Q18, Q19, Q20, Q21, Q22, Q23, Q24, Q25, Q26, Q27, Q28, Q29, Q30, Q31, Q32, Q33, Q34, Q35, Q36, Q37, Q38, Q39, Q40, Q41, Q42, Q43, Q44, Q45, Q46, Q47, Q48, Q49]), "depth" : 15.24 * mm, "hasSecondDirection" : true, "secondDirectionOppositeDirection" : false, "secondDirectionDepth" : 6.35 * mm});
        }
        {
            var Q0;
            Q0=makeQuery(id+"F4.opExtrude","SWEPT_EDGE",EDGE,{"disambiguationData":[OSD([sQuery(id+"F2.wireOp",EDGE,"E665.0.4"),sQuery(id+"F2.wireOp",EDGE,"E665.0.5")])]});
            var Q1;
            Q1=makeQuery(id+"F4.opExtrude","SWEPT_EDGE",EDGE,{"disambiguationData":[OSD([sQuery(id+"F2.wireOp",EDGE,"E664.0.4"),sQuery(id+"F2.wireOp",EDGE,"E664.0.5")])]});
            var Q2;
            Q2=makeQuery(id+"F4.opExtrude","SWEPT_EDGE",EDGE,{"disambiguationData":[OSD([sQuery(id+"F2.wireOp",EDGE,"E665.0.2"),sQuery(id+"F2.wireOp",EDGE,"E665.0.3")])]});
            var Q3;
            Q3=makeQuery(id+"F4.opExtrude","SWEPT_EDGE",EDGE,{"disambiguationData":[OSD([sQuery(id+"F2.wireOp",EDGE,"E676.0.2"),sQuery(id+"F2.wireOp",EDGE,"E676.0.3")])]});
            var Q4;
            Q4=makeQuery(id+"F4.opExtrude","SWEPT_EDGE",EDGE,{"disambiguationData":[OSD([sQuery(id+"F2.wireOp",EDGE,"E676.0.4"),sQuery(id+"F2.wireOp",EDGE,"E676.0.5")])]});
            var Q5;
            Q5=makeQuery(id+"F4.opExtrude","SWEPT_EDGE",EDGE,{"disambiguationData":[OSD([sQuery(id+"F2.wireOp",EDGE,"E666.0.4"),sQuery(id+"F2.wireOp",EDGE,"E666.0.5")])]});
            var Q6;
            Q6=makeQuery(id+"F4.opExtrude","SWEPT_EDGE",EDGE,{"disambiguationData":[OSD([sQuery(id+"F2.wireOp",EDGE,"E666.0.6"),sQuery(id+"F2.wireOp",EDGE,"E666.0.7")])]});
            var Q7;
            Q7=makeQuery(id+"F4.opExtrude","SWEPT_EDGE",EDGE,{"disambiguationData":[OSD([sQuery(id+"F2.wireOp",EDGE,"E664.0.0"),sQuery(id+"F2.wireOp",EDGE,"E664.0.1")])]});
            var Q8;
            Q8=makeQuery(id+"F4.opExtrude","SWEPT_EDGE",EDGE,{"disambiguationData":[OSD([sQuery(id+"F2.wireOp",EDGE,"E664.0.6"),sQuery(id+"F2.wireOp",EDGE,"E664.0.7")])]});
            var Q9;
            Q9=makeQuery(id+"F4.opExtrude","SWEPT_EDGE",EDGE,{"disambiguationData":[OSD([sQuery(id+"F2.wireOp",EDGE,"E663.0.2"),sQuery(id+"F2.wireOp",EDGE,"E663.0.3")])]});
            var Q10;
            Q10=makeQuery(id+"F4.opExtrude","SWEPT_EDGE",EDGE,{"disambiguationData":[OSD([sQuery(id+"F2.wireOp",EDGE,"E667.0.4"),sQuery(id+"F2.wireOp",EDGE,"E667.0.5")])]});
            var Q11;
            Q11=makeQuery(id+"F4.opExtrude","SWEPT_EDGE",EDGE,{"disambiguationData":[OSD([sQuery(id+"F2.wireOp",EDGE,"E667.0.6"),sQuery(id+"F2.wireOp",EDGE,"E667.0.7")])]});
            var Q12;
            Q12=makeQuery(id+"F4.opExtrude","SWEPT_EDGE",EDGE,{"disambiguationData":[OSD([sQuery(id+"F2.wireOp",EDGE,"E680.0.4"),sQuery(id+"F2.wireOp",EDGE,"E680.0.5")])]});
            var Q13;
            Q13=makeQuery(id+"F4.opExtrude","SWEPT_EDGE",EDGE,{"disambiguationData":[OSD([sQuery(id+"F2.wireOp",EDGE,"E675.0.6"),sQuery(id+"F2.wireOp",EDGE,"E675.0.7")])]});
            var Q14;
            Q14=makeQuery(id+"F4.opExtrude","SWEPT_EDGE",EDGE,{"disambiguationData":[OSD([sQuery(id+"F2.wireOp",EDGE,"E706.0.4"),sQuery(id+"F2.wireOp",EDGE,"E706.0.5")])]});
            var Q15;
            Q15=makeQuery(id+"F4.opExtrude","SWEPT_EDGE",EDGE,{"disambiguationData":[OSD([sQuery(id+"F2.wireOp",EDGE,"E681.0.4"),sQuery(id+"F2.wireOp",EDGE,"E681.0.5")])]});
            var Q16;
            Q16=makeQuery(id+"F4.opExtrude","SWEPT_EDGE",EDGE,{"disambiguationData":[OSD([sQuery(id+"F2.wireOp",EDGE,"E703.0.4"),sQuery(id+"F2.wireOp",EDGE,"E703.0.5")])]});
            var Q17;
            Q17=makeQuery(id+"F4.opExtrude","SWEPT_EDGE",EDGE,{"disambiguationData":[OSD([sQuery(id+"F2.wireOp",EDGE,"E705.0.4"),sQuery(id+"F2.wireOp",EDGE,"E705.0.5")])]});
            var Q18;
            Q18=makeQuery(id+"F4.opExtrude","SWEPT_EDGE",EDGE,{"disambiguationData":[OSD([sQuery(id+"F2.wireOp",EDGE,"E704.0.6"),sQuery(id+"F2.wireOp",EDGE,"E704.0.7")])]});
            var Q19;
            Q19=makeQuery(id+"F4.opExtrude","SWEPT_EDGE",EDGE,{"disambiguationData":[OSD([sQuery(id+"F2.wireOp",EDGE,"E703.0.0"),sQuery(id+"F2.wireOp",EDGE,"E703.0.1")])]});
            var Q20;
            Q20=makeQuery(id+"F4.opExtrude","SWEPT_EDGE",EDGE,{"disambiguationData":[OSD([sQuery(id+"F2.wireOp",EDGE,"E704.0.4"),sQuery(id+"F2.wireOp",EDGE,"E704.0.5")])]});
            var Q21;
            Q21=makeQuery(id+"F4.opExtrude","SWEPT_EDGE",EDGE,{"disambiguationData":[OSD([sQuery(id+"F2.wireOp",EDGE,"E707.0.4"),sQuery(id+"F2.wireOp",EDGE,"E707.0.5")])]});
            var Q22;
            Q22=makeQuery(id+"F4.opExtrude","SWEPT_EDGE",EDGE,{"disambiguationData":[OSD([sQuery(id+"F2.wireOp",EDGE,"E707.0.2"),sQuery(id+"F2.wireOp",EDGE,"E707.0.3")])]});
            var Q23;
            Q23=makeQuery(id+"F4.opExtrude","SWEPT_EDGE",EDGE,{"disambiguationData":[OSD([sQuery(id+"F2.wireOp",EDGE,"E707.0.6"),sQuery(id+"F2.wireOp",EDGE,"E707.0.7")])]});
            var Q24;
            Q24=makeQuery(id+"F4.opExtrude","SWEPT_EDGE",EDGE,{"disambiguationData":[OSD([sQuery(id+"F2.wireOp",EDGE,"E681.0.0"),sQuery(id+"F2.wireOp",EDGE,"E681.0.1")])]});
            var Q25;
            Q25=makeQuery(id+"F4.opExtrude","SWEPT_EDGE",EDGE,{"disambiguationData":[OSD([sQuery(id+"F2.wireOp",EDGE,"E676.0.6"),sQuery(id+"F2.wireOp",EDGE,"E676.0.7")])]});
            var Q26;
            Q26=makeQuery(id+"F4.opExtrude","SWEPT_EDGE",EDGE,{"disambiguationData":[OSD([sQuery(id+"F2.wireOp",EDGE,"E666.0.0"),sQuery(id+"F2.wireOp",EDGE,"E666.0.1")])]});
            var Q27;
            Q27=makeQuery(id+"F4.opExtrude","SWEPT_EDGE",EDGE,{"disambiguationData":[OSD([sQuery(id+"F2.wireOp",EDGE,"E702.0.4"),sQuery(id+"F2.wireOp",EDGE,"E702.0.5")])]});
            var Q28;
            Q28=makeQuery(id+"F4.opExtrude","SWEPT_EDGE",EDGE,{"disambiguationData":[OSD([sQuery(id+"F2.wireOp",EDGE,"E708.0.4"),sQuery(id+"F2.wireOp",EDGE,"E708.0.5")])]});
            var Q29;
            Q29=makeQuery(id+"F4.opExtrude","SWEPT_EDGE",EDGE,{"disambiguationData":[OSD([sQuery(id+"F2.wireOp",EDGE,"E708.0.6"),sQuery(id+"F2.wireOp",EDGE,"E708.0.7")])]});
            var Q30;
            Q30=makeQuery(id+"F4.opExtrude","SWEPT_EDGE",EDGE,{"disambiguationData":[OSD([sQuery(id+"F2.wireOp",EDGE,"E698.0.4"),sQuery(id+"F2.wireOp",EDGE,"E698.0.5")])]});
            var Q31;
            Q31=makeQuery(id+"F4.opExtrude","SWEPT_EDGE",EDGE,{"disambiguationData":[OSD([sQuery(id+"F2.wireOp",EDGE,"E701.0.4"),sQuery(id+"F2.wireOp",EDGE,"E701.0.5")])]});
            var Q32;
            Q32=makeQuery(id+"F4.opExtrude","SWEPT_EDGE",EDGE,{"disambiguationData":[OSD([sQuery(id+"F2.wireOp",EDGE,"E665.0.0"),sQuery(id+"F2.wireOp",EDGE,"E665.0.1")])]});
            var Q33;
            Q33=makeQuery(id+"F4.opExtrude","SWEPT_EDGE",EDGE,{"disambiguationData":[OSD([sQuery(id+"F2.wireOp",EDGE,"E665.0.8"),sQuery(id+"F2.wireOp",EDGE,"E665.0.9")])]});
            var Q34;
            Q34=makeQuery(id+"F4.opExtrude","SWEPT_EDGE",EDGE,{"disambiguationData":[OSD([sQuery(id+"F2.wireOp",EDGE,"E666.0.2"),sQuery(id+"F2.wireOp",EDGE,"E666.0.3")])]});
            var Q35;
            Q35=makeQuery(id+"F4.opExtrude","SWEPT_EDGE",EDGE,{"disambiguationData":[OSD([sQuery(id+"F2.wireOp",EDGE,"E666.0.8"),sQuery(id+"F2.wireOp",EDGE,"E666.0.9")])]});
            var Q36;
            Q36=makeQuery(id+"F4.opExtrude","SWEPT_EDGE",EDGE,{"disambiguationData":[OSD([sQuery(id+"F2.wireOp",EDGE,"E675.0.2"),sQuery(id+"F2.wireOp",EDGE,"E675.0.3")])]});
            var Q37;
            Q37=makeQuery(id+"F4.opExtrude","SWEPT_EDGE",EDGE,{"disambiguationData":[OSD([sQuery(id+"F2.wireOp",EDGE,"E676.0.8"),sQuery(id+"F2.wireOp",EDGE,"E676.0.9")])]});
            var Q38;
            Q38=makeQuery(id+"F4.opExtrude","SWEPT_EDGE",EDGE,{"disambiguationData":[OSD([sQuery(id+"F2.wireOp",EDGE,"E676.0.0"),sQuery(id+"F2.wireOp",EDGE,"E676.0.1")])]});
            var Q39;
            Q39=makeQuery(id+"F4.opExtrude","SWEPT_EDGE",EDGE,{"disambiguationData":[OSD([sQuery(id+"F2.wireOp",EDGE,"E664.0.8"),sQuery(id+"F2.wireOp",EDGE,"E664.0.9")])]});
            var Q40;
            Q40=makeQuery(id+"F4.opExtrude","SWEPT_EDGE",EDGE,{"disambiguationData":[OSD([sQuery(id+"F2.wireOp",EDGE,"E667.0.2"),sQuery(id+"F2.wireOp",EDGE,"E667.0.3")])]});
            var Q41;
            Q41=makeQuery(id+"F4.opExtrude","SWEPT_EDGE",EDGE,{"disambiguationData":[OSD([sQuery(id+"F2.wireOp",EDGE,"E675.0.4"),sQuery(id+"F2.wireOp",EDGE,"E675.0.5")])]});
            var Q42;
            Q42=makeQuery(id+"F4.opExtrude","SWEPT_EDGE",EDGE,{"disambiguationData":[OSD([sQuery(id+"F2.wireOp",EDGE,"E664.0.2"),sQuery(id+"F2.wireOp",EDGE,"E664.0.3")])]});
            var Q43;
            Q43=makeQuery(id+"F4.opExtrude","SWEPT_EDGE",EDGE,{"disambiguationData":[OSD([sQuery(id+"F2.wireOp",EDGE,"E665.0.6"),sQuery(id+"F2.wireOp",EDGE,"E665.0.7")])]});
            var Q44;
            Q44=makeQuery(id+"F4.opExtrude","SWEPT_EDGE",EDGE,{"disambiguationData":[OSD([sQuery(id+"F2.wireOp",EDGE,"E667.0.8"),sQuery(id+"F2.wireOp",EDGE,"E667.0.9")])]});
            var Q45;
            Q45=makeQuery(id+"F4.opExtrude","SWEPT_EDGE",EDGE,{"disambiguationData":[OSD([sQuery(id+"F2.wireOp",EDGE,"E675.0.8"),sQuery(id+"F2.wireOp",EDGE,"E675.0.9")])]});
            var Q46;
            Q46=makeQuery(id+"F4.opExtrude","SWEPT_EDGE",EDGE,{"disambiguationData":[OSD([sQuery(id+"F2.wireOp",EDGE,"E675.0.0"),sQuery(id+"F2.wireOp",EDGE,"E675.0.1")])]});
            var Q47;
            Q47=makeQuery(id+"F4.opExtrude","SWEPT_EDGE",EDGE,{"disambiguationData":[OSD([sQuery(id+"F2.wireOp",EDGE,"E681.0.6"),sQuery(id+"F2.wireOp",EDGE,"E681.0.7")])]});
            var Q48;
            Q48=makeQuery(id+"F4.opExtrude","SWEPT_EDGE",EDGE,{"disambiguationData":[OSD([sQuery(id+"F2.wireOp",EDGE,"E681.0.2"),sQuery(id+"F2.wireOp",EDGE,"E681.0.3")])]});
            var Q49;
            Q49=makeQuery(id+"F4.opExtrude","SWEPT_EDGE",EDGE,{"disambiguationData":[OSD([sQuery(id+"F2.wireOp",EDGE,"E681.0.8"),sQuery(id+"F2.wireOp",EDGE,"E681.0.9")])]});
            var Q50;
            Q50=makeQuery(id+"F4.opExtrude","SWEPT_EDGE",EDGE,{"disambiguationData":[OSD([sQuery(id+"F2.wireOp",EDGE,"E680.0.2"),sQuery(id+"F2.wireOp",EDGE,"E680.0.3")])]});
            var Q51;
            Q51=makeQuery(id+"F4.opExtrude","SWEPT_EDGE",EDGE,{"disambiguationData":[OSD([sQuery(id+"F2.wireOp",EDGE,"E674.0.0"),sQuery(id+"F2.wireOp",EDGE,"E674.0.1")])]});
            var Q52;
            Q52=makeQuery(id+"F4.opExtrude","SWEPT_EDGE",EDGE,{"disambiguationData":[OSD([sQuery(id+"F2.wireOp",EDGE,"E674.0.2"),sQuery(id+"F2.wireOp",EDGE,"E674.0.3")])]});
            var Q53;
            Q53=makeQuery(id+"F4.opExtrude","SWEPT_EDGE",EDGE,{"disambiguationData":[OSD([sQuery(id+"F2.wireOp",EDGE,"E680.0.6"),sQuery(id+"F2.wireOp",EDGE,"E680.0.7")])]});
            var Q54;
            Q54=makeQuery(id+"F4.opExtrude","SWEPT_EDGE",EDGE,{"disambiguationData":[OSD([sQuery(id+"F2.wireOp",EDGE,"E680.0.8"),sQuery(id+"F2.wireOp",EDGE,"E680.0.9")])]});
            var Q55;
            Q55=makeQuery(id+"F4.opExtrude","SWEPT_EDGE",EDGE,{"disambiguationData":[OSD([sQuery(id+"F2.wireOp",EDGE,"E680.0.0"),sQuery(id+"F2.wireOp",EDGE,"E680.0.1")])]});
            var Q56;
            Q56=makeQuery(id+"F4.opExtrude","SWEPT_EDGE",EDGE,{"disambiguationData":[OSD([sQuery(id+"F2.wireOp",EDGE,"E706.0.0"),sQuery(id+"F2.wireOp",EDGE,"E706.0.1")])]});
            var Q57;
            Q57=makeQuery(id+"F4.opExtrude","SWEPT_EDGE",EDGE,{"disambiguationData":[OSD([sQuery(id+"F2.wireOp",EDGE,"E706.0.2"),sQuery(id+"F2.wireOp",EDGE,"E706.0.3")])]});
            var Q58;
            Q58=makeQuery(id+"F4.opExtrude","SWEPT_EDGE",EDGE,{"disambiguationData":[OSD([sQuery(id+"F2.wireOp",EDGE,"E706.0.8"),sQuery(id+"F2.wireOp",EDGE,"E706.0.9")])]});
            var Q59;
            Q59=makeQuery(id+"F4.opExtrude","SWEPT_EDGE",EDGE,{"disambiguationData":[OSD([sQuery(id+"F2.wireOp",EDGE,"E706.0.6"),sQuery(id+"F2.wireOp",EDGE,"E706.0.7")])]});
            var Q60;
            Q60=makeQuery(id+"F4.opExtrude","SWEPT_EDGE",EDGE,{"disambiguationData":[OSD([sQuery(id+"F2.wireOp",EDGE,"E674.0.8"),sQuery(id+"F2.wireOp",EDGE,"E674.0.9")])]});
            var Q61;
            Q61=makeQuery(id+"F4.opExtrude","SWEPT_EDGE",EDGE,{"disambiguationData":[OSD([sQuery(id+"F2.wireOp",EDGE,"E674.0.6"),sQuery(id+"F2.wireOp",EDGE,"E674.0.7")])]});
            var Q62;
            Q62=makeQuery(id+"F4.opExtrude","SWEPT_EDGE",EDGE,{"disambiguationData":[OSD([sQuery(id+"F2.wireOp",EDGE,"E679.0.2"),sQuery(id+"F2.wireOp",EDGE,"E679.0.3")])]});
            var Q63;
            Q63=makeQuery(id+"F4.opExtrude","SWEPT_EDGE",EDGE,{"disambiguationData":[OSD([sQuery(id+"F2.wireOp",EDGE,"E679.0.0"),sQuery(id+"F2.wireOp",EDGE,"E679.0.1")])]});
            var Q64;
            Q64=makeQuery(id+"F4.opExtrude","SWEPT_EDGE",EDGE,{"disambiguationData":[OSD([sQuery(id+"F2.wireOp",EDGE,"E679.0.8"),sQuery(id+"F2.wireOp",EDGE,"E679.0.9")])]});
            var Q65;
            Q65=makeQuery(id+"F4.opExtrude","SWEPT_EDGE",EDGE,{"disambiguationData":[OSD([sQuery(id+"F2.wireOp",EDGE,"E695.0.8"),sQuery(id+"F2.wireOp",EDGE,"E695.0.9")])]});
            var Q66;
            Q66=makeQuery(id+"F4.opExtrude","SWEPT_EDGE",EDGE,{"disambiguationData":[OSD([sQuery(id+"F2.wireOp",EDGE,"E695.0.0"),sQuery(id+"F2.wireOp",EDGE,"E695.0.1")])]});
            var Q67;
            Q67=makeQuery(id+"F4.opExtrude","SWEPT_EDGE",EDGE,{"disambiguationData":[OSD([sQuery(id+"F2.wireOp",EDGE,"E695.0.2"),sQuery(id+"F2.wireOp",EDGE,"E695.0.3")])]});
            var Q68;
            Q68=makeQuery(id+"F4.opExtrude","SWEPT_EDGE",EDGE,{"disambiguationData":[OSD([sQuery(id+"F2.wireOp",EDGE,"E695.0.6"),sQuery(id+"F2.wireOp",EDGE,"E695.0.7")])]});
            var Q69;
            Q69=makeQuery(id+"F4.opExtrude","SWEPT_EDGE",EDGE,{"disambiguationData":[OSD([sQuery(id+"F2.wireOp",EDGE,"E679.0.4"),sQuery(id+"F2.wireOp",EDGE,"E679.0.5")])]});
            var Q70;
            Q70=makeQuery(id+"F4.opExtrude","SWEPT_EDGE",EDGE,{"disambiguationData":[OSD([sQuery(id+"F2.wireOp",EDGE,"E674.0.4"),sQuery(id+"F2.wireOp",EDGE,"E674.0.5")])]});
            var Q71;
            Q71=makeQuery(id+"F4.opExtrude","SWEPT_EDGE",EDGE,{"disambiguationData":[OSD([sQuery(id+"F2.wireOp",EDGE,"E679.0.6"),sQuery(id+"F2.wireOp",EDGE,"E679.0.7")])]});
            var Q72;
            Q72=makeQuery(id+"F4.opExtrude","SWEPT_EDGE",EDGE,{"disambiguationData":[OSD([sQuery(id+"F2.wireOp",EDGE,"E690.0.4"),sQuery(id+"F2.wireOp",EDGE,"E690.0.5")])]});
            var Q73;
            Q73=makeQuery(id+"F4.opExtrude","SWEPT_EDGE",EDGE,{"disambiguationData":[OSD([sQuery(id+"F2.wireOp",EDGE,"E690.0.2"),sQuery(id+"F2.wireOp",EDGE,"E690.0.3")])]});
            var Q74;
            Q74=makeQuery(id+"F4.opExtrude","SWEPT_EDGE",EDGE,{"disambiguationData":[OSD([sQuery(id+"F2.wireOp",EDGE,"E668.0.2"),sQuery(id+"F2.wireOp",EDGE,"E668.0.3")])]});
            var Q75;
            Q75=makeQuery(id+"F4.opExtrude","SWEPT_EDGE",EDGE,{"disambiguationData":[OSD([sQuery(id+"F2.wireOp",EDGE,"E668.0.0"),sQuery(id+"F2.wireOp",EDGE,"E668.0.1")])]});
            var Q76;
            Q76=makeQuery(id+"F4.opExtrude","SWEPT_EDGE",EDGE,{"disambiguationData":[OSD([sQuery(id+"F2.wireOp",EDGE,"E663.0.0"),sQuery(id+"F2.wireOp",EDGE,"E663.0.1")])]});
            var Q77;
            Q77=makeQuery(id+"F4.opExtrude","SWEPT_EDGE",EDGE,{"disambiguationData":[OSD([sQuery(id+"F2.wireOp",EDGE,"E663.0.8"),sQuery(id+"F2.wireOp",EDGE,"E663.0.9")])]});
            var Q78;
            Q78=makeQuery(id+"F4.opExtrude","SWEPT_EDGE",EDGE,{"disambiguationData":[OSD([sQuery(id+"F2.wireOp",EDGE,"E707.0.0"),sQuery(id+"F2.wireOp",EDGE,"E707.0.1")])]});
            var Q79;
            Q79=makeQuery(id+"F4.opExtrude","SWEPT_EDGE",EDGE,{"disambiguationData":[OSD([sQuery(id+"F2.wireOp",EDGE,"E707.0.8"),sQuery(id+"F2.wireOp",EDGE,"E707.0.9")])]});
            var Q80;
            Q80=makeQuery(id+"F4.opExtrude","SWEPT_EDGE",EDGE,{"disambiguationData":[OSD([sQuery(id+"F2.wireOp",EDGE,"E704.0.0"),sQuery(id+"F2.wireOp",EDGE,"E704.0.1")])]});
            var Q81;
            Q81=makeQuery(id+"F4.opExtrude","SWEPT_EDGE",EDGE,{"disambiguationData":[OSD([sQuery(id+"F2.wireOp",EDGE,"E704.0.8"),sQuery(id+"F2.wireOp",EDGE,"E704.0.9")])]});
            var Q82;
            Q82=makeQuery(id+"F4.opExtrude","SWEPT_EDGE",EDGE,{"disambiguationData":[OSD([sQuery(id+"F2.wireOp",EDGE,"E703.0.8"),sQuery(id+"F2.wireOp",EDGE,"E703.0.9")])]});
            var Q83;
            Q83=makeQuery(id+"F4.opExtrude","SWEPT_EDGE",EDGE,{"disambiguationData":[OSD([sQuery(id+"F2.wireOp",EDGE,"E702.0.8"),sQuery(id+"F2.wireOp",EDGE,"E702.0.9")])]});
            var Q84;
            Q84=makeQuery(id+"F4.opExtrude","SWEPT_EDGE",EDGE,{"disambiguationData":[OSD([sQuery(id+"F2.wireOp",EDGE,"E702.0.0"),sQuery(id+"F2.wireOp",EDGE,"E702.0.1")])]});
            var Q85;
            Q85=makeQuery(id+"F4.opExtrude","SWEPT_EDGE",EDGE,{"disambiguationData":[OSD([sQuery(id+"F2.wireOp",EDGE,"E702.0.2"),sQuery(id+"F2.wireOp",EDGE,"E702.0.3")])]});
            var Q86;
            Q86=makeQuery(id+"F4.opExtrude","SWEPT_EDGE",EDGE,{"disambiguationData":[OSD([sQuery(id+"F2.wireOp",EDGE,"E702.0.6"),sQuery(id+"F2.wireOp",EDGE,"E702.0.7")])]});
            var Q87;
            Q87=makeQuery(id+"F4.opExtrude","SWEPT_EDGE",EDGE,{"disambiguationData":[OSD([sQuery(id+"F2.wireOp",EDGE,"E701.0.0"),sQuery(id+"F2.wireOp",EDGE,"E701.0.1")])]});
            var Q88;
            Q88=makeQuery(id+"F4.opExtrude","SWEPT_EDGE",EDGE,{"disambiguationData":[OSD([sQuery(id+"F2.wireOp",EDGE,"E701.0.2"),sQuery(id+"F2.wireOp",EDGE,"E701.0.3")])]});
            var Q89;
            Q89=makeQuery(id+"F4.opExtrude","SWEPT_EDGE",EDGE,{"disambiguationData":[OSD([sQuery(id+"F2.wireOp",EDGE,"E701.0.8"),sQuery(id+"F2.wireOp",EDGE,"E701.0.9")])]});
            var Q90;
            Q90=makeQuery(id+"F4.opExtrude","SWEPT_EDGE",EDGE,{"disambiguationData":[OSD([sQuery(id+"F2.wireOp",EDGE,"E700.0.2"),sQuery(id+"F2.wireOp",EDGE,"E700.0.3")])]});
            var Q91;
            Q91=makeQuery(id+"F4.opExtrude","SWEPT_EDGE",EDGE,{"disambiguationData":[OSD([sQuery(id+"F2.wireOp",EDGE,"E700.0.6"),sQuery(id+"F2.wireOp",EDGE,"E700.0.7")])]});
            var Q92;
            Q92=makeQuery(id+"F4.opExtrude","SWEPT_EDGE",EDGE,{"disambiguationData":[OSD([sQuery(id+"F2.wireOp",EDGE,"E700.0.4"),sQuery(id+"F2.wireOp",EDGE,"E700.0.5")])]});
            var Q93;
            Q93=makeQuery(id+"F4.opExtrude","SWEPT_EDGE",EDGE,{"disambiguationData":[OSD([sQuery(id+"F2.wireOp",EDGE,"E695.0.4"),sQuery(id+"F2.wireOp",EDGE,"E695.0.5")])]});
            var Q94;
            Q94=makeQuery(id+"F4.opExtrude","SWEPT_EDGE",EDGE,{"disambiguationData":[OSD([sQuery(id+"F2.wireOp",EDGE,"E701.0.6"),sQuery(id+"F2.wireOp",EDGE,"E701.0.7")])]});
            var Q95;
            Q95=makeQuery(id+"F4.opExtrude","SWEPT_EDGE",EDGE,{"disambiguationData":[OSD([sQuery(id+"F2.wireOp",EDGE,"E694.0.2"),sQuery(id+"F2.wireOp",EDGE,"E694.0.3")])]});
            var Q96;
            Q96=makeQuery(id+"F4.opExtrude","SWEPT_EDGE",EDGE,{"disambiguationData":[OSD([sQuery(id+"F2.wireOp",EDGE,"E663.0.4"),sQuery(id+"F2.wireOp",EDGE,"E663.0.5")])]});
            var Q97;
            Q97=makeQuery(id+"F4.opExtrude","SWEPT_EDGE",EDGE,{"disambiguationData":[OSD([sQuery(id+"F2.wireOp",EDGE,"E663.0.6"),sQuery(id+"F2.wireOp",EDGE,"E663.0.7")])]});
            var Q98;
            Q98=makeQuery(id+"F4.opExtrude","SWEPT_EDGE",EDGE,{"disambiguationData":[OSD([sQuery(id+"F2.wireOp",EDGE,"E668.0.4"),sQuery(id+"F2.wireOp",EDGE,"E668.0.5")])]});
            var Q99;
            Q99=makeQuery(id+"F4.opExtrude","SWEPT_EDGE",EDGE,{"disambiguationData":[OSD([sQuery(id+"F2.wireOp",EDGE,"E673.0.2"),sQuery(id+"F2.wireOp",EDGE,"E673.0.3")])]});
            var Q100;
            Q100=makeQuery(id+"F4.opExtrude","SWEPT_EDGE",EDGE,{"disambiguationData":[OSD([sQuery(id+"F2.wireOp",EDGE,"E673.0.4"),sQuery(id+"F2.wireOp",EDGE,"E673.0.5")])]});
            var Q101;
            Q101=makeQuery(id+"F4.opExtrude","SWEPT_EDGE",EDGE,{"disambiguationData":[OSD([sQuery(id+"F2.wireOp",EDGE,"E673.0.6"),sQuery(id+"F2.wireOp",EDGE,"E673.0.7")])]});
            var Q102;
            Q102=makeQuery(id+"F4.opExtrude","SWEPT_EDGE",EDGE,{"disambiguationData":[OSD([sQuery(id+"F2.wireOp",EDGE,"E673.0.8"),sQuery(id+"F2.wireOp",EDGE,"E673.0.9")])]});
            var Q103;
            Q103=makeQuery(id+"F4.opExtrude","SWEPT_EDGE",EDGE,{"disambiguationData":[OSD([sQuery(id+"F2.wireOp",EDGE,"E667.0.0"),sQuery(id+"F2.wireOp",EDGE,"E667.0.1")])]});
            var Q104;
            Q104=makeQuery(id+"F4.opExtrude","SWEPT_EDGE",EDGE,{"disambiguationData":[OSD([sQuery(id+"F2.wireOp",EDGE,"E662.0.2"),sQuery(id+"F2.wireOp",EDGE,"E662.0.3")])]});
            var Q105;
            Q105=makeQuery(id+"F4.opExtrude","SWEPT_EDGE",EDGE,{"disambiguationData":[OSD([sQuery(id+"F2.wireOp",EDGE,"E662.0.4"),sQuery(id+"F2.wireOp",EDGE,"E662.0.5")])]});
            var Q106;
            Q106=makeQuery(id+"F4.opExtrude","SWEPT_EDGE",EDGE,{"disambiguationData":[OSD([sQuery(id+"F2.wireOp",EDGE,"E662.0.0"),sQuery(id+"F2.wireOp",EDGE,"E662.0.1")])]});
            var Q107;
            Q107=makeQuery(id+"F4.opExtrude","SWEPT_EDGE",EDGE,{"disambiguationData":[OSD([sQuery(id+"F2.wireOp",EDGE,"E662.0.8"),sQuery(id+"F2.wireOp",EDGE,"E662.0.9")])]});
            var Q108;
            Q108=makeQuery(id+"F4.opExtrude","SWEPT_EDGE",EDGE,{"disambiguationData":[OSD([sQuery(id+"F2.wireOp",EDGE,"E662.0.6"),sQuery(id+"F2.wireOp",EDGE,"E662.0.7")])]});
            var Q109;
            Q109=makeQuery(id+"F4.opExtrude","SWEPT_EDGE",EDGE,{"disambiguationData":[OSD([sQuery(id+"F2.wireOp",EDGE,"E668.0.6"),sQuery(id+"F2.wireOp",EDGE,"E668.0.7")])]});
            var Q110;
            Q110=makeQuery(id+"F4.opExtrude","SWEPT_EDGE",EDGE,{"disambiguationData":[OSD([sQuery(id+"F2.wireOp",EDGE,"E668.0.8"),sQuery(id+"F2.wireOp",EDGE,"E668.0.9")])]});
            var Q111;
            Q111=makeQuery(id+"F4.opExtrude","SWEPT_EDGE",EDGE,{"disambiguationData":[OSD([sQuery(id+"F2.wireOp",EDGE,"E669.0.2"),sQuery(id+"F2.wireOp",EDGE,"E669.0.3")])]});
            var Q112;
            Q112=makeQuery(id+"F4.opExtrude","SWEPT_EDGE",EDGE,{"disambiguationData":[OSD([sQuery(id+"F2.wireOp",EDGE,"E669.0.4"),sQuery(id+"F2.wireOp",EDGE,"E669.0.5")])]});
            var Q113;
            Q113=makeQuery(id+"F4.opExtrude","SWEPT_EDGE",EDGE,{"disambiguationData":[OSD([sQuery(id+"F2.wireOp",EDGE,"E661.0.2"),sQuery(id+"F2.wireOp",EDGE,"E661.0.3")])]});
            var Q114;
            Q114=makeQuery(id+"F4.opExtrude","SWEPT_EDGE",EDGE,{"disambiguationData":[OSD([sQuery(id+"F2.wireOp",EDGE,"E661.0.0"),sQuery(id+"F2.wireOp",EDGE,"E661.0.1")])]});
            var Q115;
            Q115=makeQuery(id+"F4.opExtrude","SWEPT_EDGE",EDGE,{"disambiguationData":[OSD([sQuery(id+"F2.wireOp",EDGE,"E669.0.6"),sQuery(id+"F2.wireOp",EDGE,"E669.0.7")])]});
            var Q116;
            Q116=makeQuery(id+"F4.opExtrude","SWEPT_EDGE",EDGE,{"disambiguationData":[OSD([sQuery(id+"F2.wireOp",EDGE,"E669.0.0"),sQuery(id+"F2.wireOp",EDGE,"E669.0.1")])]});
            var Q117;
            Q117=makeQuery(id+"F4.opExtrude","SWEPT_EDGE",EDGE,{"disambiguationData":[OSD([sQuery(id+"F2.wireOp",EDGE,"E673.0.0"),sQuery(id+"F2.wireOp",EDGE,"E673.0.1")])]});
            var Q118;
            Q118=makeQuery(id+"F4.opExtrude","SWEPT_EDGE",EDGE,{"disambiguationData":[OSD([sQuery(id+"F2.wireOp",EDGE,"E669.0.8"),sQuery(id+"F2.wireOp",EDGE,"E669.0.9")])]});
            var Q119;
            Q119=makeQuery(id+"F4.opExtrude","SWEPT_EDGE",EDGE,{"disambiguationData":[OSD([sQuery(id+"F2.wireOp",EDGE,"E661.0.8"),sQuery(id+"F2.wireOp",EDGE,"E661.0.9")])]});
            var Q120;
            Q120=makeQuery(id+"F4.opExtrude","SWEPT_EDGE",EDGE,{"disambiguationData":[OSD([sQuery(id+"F2.wireOp",EDGE,"E670.0.2"),sQuery(id+"F2.wireOp",EDGE,"E670.0.3")])]});
            var Q121;
            Q121=makeQuery(id+"F4.opExtrude","SWEPT_EDGE",EDGE,{"disambiguationData":[OSD([sQuery(id+"F2.wireOp",EDGE,"E670.0.4"),sQuery(id+"F2.wireOp",EDGE,"E670.0.5")])]});
            var Q122;
            Q122=makeQuery(id+"F4.opExtrude","SWEPT_EDGE",EDGE,{"disambiguationData":[OSD([sQuery(id+"F2.wireOp",EDGE,"E672.0.2"),sQuery(id+"F2.wireOp",EDGE,"E672.0.3")])]});
            var Q123;
            Q123=makeQuery(id+"F4.opExtrude","SWEPT_EDGE",EDGE,{"disambiguationData":[OSD([sQuery(id+"F2.wireOp",EDGE,"E672.0.4"),sQuery(id+"F2.wireOp",EDGE,"E672.0.5")])]});
            var Q124;
            Q124=makeQuery(id+"F4.opExtrude","SWEPT_EDGE",EDGE,{"disambiguationData":[OSD([sQuery(id+"F2.wireOp",EDGE,"E678.0.2"),sQuery(id+"F2.wireOp",EDGE,"E678.0.3")])]});
            var Q125;
            Q125=makeQuery(id+"F4.opExtrude","SWEPT_EDGE",EDGE,{"disambiguationData":[OSD([sQuery(id+"F2.wireOp",EDGE,"E678.0.4"),sQuery(id+"F2.wireOp",EDGE,"E678.0.5")])]});
            var Q126;
            Q126=makeQuery(id+"F4.opExtrude","SWEPT_EDGE",EDGE,{"disambiguationData":[OSD([sQuery(id+"F2.wireOp",EDGE,"E670.0.0"),sQuery(id+"F2.wireOp",EDGE,"E670.0.1")])]});
            var Q127;
            Q127=makeQuery(id+"F4.opExtrude","SWEPT_EDGE",EDGE,{"disambiguationData":[OSD([sQuery(id+"F2.wireOp",EDGE,"E670.0.8"),sQuery(id+"F2.wireOp",EDGE,"E670.0.9")])]});
            var Q128;
            Q128=makeQuery(id+"F4.opExtrude","SWEPT_EDGE",EDGE,{"disambiguationData":[OSD([sQuery(id+"F2.wireOp",EDGE,"E672.0.0"),sQuery(id+"F2.wireOp",EDGE,"E672.0.1")])]});
            var Q129;
            Q129=makeQuery(id+"F4.opExtrude","SWEPT_EDGE",EDGE,{"disambiguationData":[OSD([sQuery(id+"F2.wireOp",EDGE,"E672.0.6"),sQuery(id+"F2.wireOp",EDGE,"E672.0.7")])]});
            var Q130;
            Q130=makeQuery(id+"F4.opExtrude","SWEPT_EDGE",EDGE,{"disambiguationData":[OSD([sQuery(id+"F2.wireOp",EDGE,"E660.0.2"),sQuery(id+"F2.wireOp",EDGE,"E660.0.3")])]});
            var Q131;
            Q131=makeQuery(id+"F4.opExtrude","SWEPT_EDGE",EDGE,{"disambiguationData":[OSD([sQuery(id+"F2.wireOp",EDGE,"E661.0.4"),sQuery(id+"F2.wireOp",EDGE,"E661.0.5")])]});
            var Q132;
            Q132=makeQuery(id+"F4.opExtrude","SWEPT_EDGE",EDGE,{"disambiguationData":[OSD([sQuery(id+"F2.wireOp",EDGE,"E661.0.6"),sQuery(id+"F2.wireOp",EDGE,"E661.0.7")])]});
            var Q133;
            Q133=makeQuery(id+"F4.opExtrude","SWEPT_EDGE",EDGE,{"disambiguationData":[OSD([sQuery(id+"F2.wireOp",EDGE,"E670.0.6"),sQuery(id+"F2.wireOp",EDGE,"E670.0.7")])]});
            var Q134;
            Q134=makeQuery(id+"F4.opExtrude","SWEPT_EDGE",EDGE,{"disambiguationData":[OSD([sQuery(id+"F2.wireOp",EDGE,"E660.0.8"),sQuery(id+"F2.wireOp",EDGE,"E660.0.9")])]});
            var Q135;
            Q135=makeQuery(id+"F4.opExtrude","SWEPT_EDGE",EDGE,{"disambiguationData":[OSD([sQuery(id+"F2.wireOp",EDGE,"E660.0.0"),sQuery(id+"F2.wireOp",EDGE,"E660.0.1")])]});
            var Q136;
            Q136=makeQuery(id+"F4.opExtrude","SWEPT_EDGE",EDGE,{"disambiguationData":[OSD([sQuery(id+"F2.wireOp",EDGE,"E660.0.6"),sQuery(id+"F2.wireOp",EDGE,"E660.0.7")])]});
            var Q137;
            Q137=makeQuery(id+"F4.opExtrude","SWEPT_EDGE",EDGE,{"disambiguationData":[OSD([sQuery(id+"F2.wireOp",EDGE,"E660.0.4"),sQuery(id+"F2.wireOp",EDGE,"E660.0.5")])]});
            var Q138;
            Q138=makeQuery(id+"F4.opExtrude","SWEPT_EDGE",EDGE,{"disambiguationData":[OSD([sQuery(id+"F2.wireOp",EDGE,"E672.0.8"),sQuery(id+"F2.wireOp",EDGE,"E672.0.9")])]});
            var Q139;
            Q139=makeQuery(id+"F4.opExtrude","SWEPT_EDGE",EDGE,{"disambiguationData":[OSD([sQuery(id+"F2.wireOp",EDGE,"E678.0.8"),sQuery(id+"F2.wireOp",EDGE,"E678.0.9")])]});
            var Q140;
            Q140=makeQuery(id+"F4.opExtrude","SWEPT_EDGE",EDGE,{"disambiguationData":[OSD([sQuery(id+"F2.wireOp",EDGE,"E678.0.6"),sQuery(id+"F2.wireOp",EDGE,"E678.0.7")])]});
            var Q141;
            Q141=makeQuery(id+"F4.opExtrude","SWEPT_EDGE",EDGE,{"disambiguationData":[OSD([sQuery(id+"F2.wireOp",EDGE,"E690.0.6"),sQuery(id+"F2.wireOp",EDGE,"E690.0.7")])]});
            var Q142;
            Q142=makeQuery(id+"F4.opExtrude","SWEPT_EDGE",EDGE,{"disambiguationData":[OSD([sQuery(id+"F2.wireOp",EDGE,"E690.0.8"),sQuery(id+"F2.wireOp",EDGE,"E690.0.9")])]});
            var Q143;
            Q143=makeQuery(id+"F4.opExtrude","SWEPT_EDGE",EDGE,{"disambiguationData":[OSD([sQuery(id+"F2.wireOp",EDGE,"E678.0.0"),sQuery(id+"F2.wireOp",EDGE,"E678.0.1")])]});
            var Q144;
            Q144=makeQuery(id+"F4.opExtrude","SWEPT_EDGE",EDGE,{"disambiguationData":[OSD([sQuery(id+"F2.wireOp",EDGE,"E671.0.6"),sQuery(id+"F2.wireOp",EDGE,"E671.0.7")])]});
            var Q145;
            Q145=makeQuery(id+"F4.opExtrude","SWEPT_EDGE",EDGE,{"disambiguationData":[OSD([sQuery(id+"F2.wireOp",EDGE,"E671.0.4"),sQuery(id+"F2.wireOp",EDGE,"E671.0.5")])]});
            var Q146;
            Q146=makeQuery(id+"F4.opExtrude","SWEPT_EDGE",EDGE,{"disambiguationData":[OSD([sQuery(id+"F2.wireOp",EDGE,"E671.0.0"),sQuery(id+"F2.wireOp",EDGE,"E671.0.1")])]});
            var Q147;
            Q147=makeQuery(id+"F4.opExtrude","SWEPT_EDGE",EDGE,{"disambiguationData":[OSD([sQuery(id+"F2.wireOp",EDGE,"E677.0.6"),sQuery(id+"F2.wireOp",EDGE,"E677.0.7")])]});
            var Q148;
            Q148=makeQuery(id+"F4.opExtrude","SWEPT_EDGE",EDGE,{"disambiguationData":[OSD([sQuery(id+"F2.wireOp",EDGE,"E671.0.8"),sQuery(id+"F2.wireOp",EDGE,"E671.0.9")])]});
            var Q149;
            Q149=makeQuery(id+"F4.opExtrude","SWEPT_EDGE",EDGE,{"disambiguationData":[OSD([sQuery(id+"F2.wireOp",EDGE,"E677.0.0"),sQuery(id+"F2.wireOp",EDGE,"E677.0.1")])]});
            var Q150;
            Q150=makeQuery(id+"F4.opExtrude","SWEPT_EDGE",EDGE,{"disambiguationData":[OSD([sQuery(id+"F2.wireOp",EDGE,"E683.0.4"),sQuery(id+"F2.wireOp",EDGE,"E683.0.5")])]});
            var Q151;
            Q151=makeQuery(id+"F4.opExtrude","SWEPT_EDGE",EDGE,{"disambiguationData":[OSD([sQuery(id+"F2.wireOp",EDGE,"E691.0.4"),sQuery(id+"F2.wireOp",EDGE,"E691.0.5")])]});
            var Q152;
            Q152=makeQuery(id+"F4.opExtrude","SWEPT_EDGE",EDGE,{"disambiguationData":[OSD([sQuery(id+"F2.wireOp",EDGE,"E671.0.2"),sQuery(id+"F2.wireOp",EDGE,"E671.0.3")])]});
            var Q153;
            Q153=makeQuery(id+"F4.opExtrude","SWEPT_EDGE",EDGE,{"disambiguationData":[OSD([sQuery(id+"F2.wireOp",EDGE,"E677.0.4"),sQuery(id+"F2.wireOp",EDGE,"E677.0.5")])]});
            var Q154;
            Q154=makeQuery(id+"F4.opExtrude","SWEPT_EDGE",EDGE,{"disambiguationData":[OSD([sQuery(id+"F2.wireOp",EDGE,"E677.0.2"),sQuery(id+"F2.wireOp",EDGE,"E677.0.3")])]});
            var Q155;
            Q155=makeQuery(id+"F4.opExtrude","SWEPT_EDGE",EDGE,{"disambiguationData":[OSD([sQuery(id+"F2.wireOp",EDGE,"E682.0.2"),sQuery(id+"F2.wireOp",EDGE,"E682.0.3")])]});
            var Q156;
            Q156=makeQuery(id+"F4.opExtrude","SWEPT_EDGE",EDGE,{"disambiguationData":[OSD([sQuery(id+"F2.wireOp",EDGE,"E682.0.4"),sQuery(id+"F2.wireOp",EDGE,"E682.0.5")])]});
            var Q157;
            Q157=makeQuery(id+"F4.opExtrude","SWEPT_EDGE",EDGE,{"disambiguationData":[OSD([sQuery(id+"F2.wireOp",EDGE,"E683.0.6"),sQuery(id+"F2.wireOp",EDGE,"E683.0.7")])]});
            var Q158;
            Q158=makeQuery(id+"F4.opExtrude","SWEPT_EDGE",EDGE,{"disambiguationData":[OSD([sQuery(id+"F2.wireOp",EDGE,"E682.0.0"),sQuery(id+"F2.wireOp",EDGE,"E682.0.1")])]});
            var Q159;
            Q159=makeQuery(id+"F4.opExtrude","SWEPT_EDGE",EDGE,{"disambiguationData":[OSD([sQuery(id+"F2.wireOp",EDGE,"E682.0.8"),sQuery(id+"F2.wireOp",EDGE,"E682.0.9")])]});
            var Q160;
            Q160=makeQuery(id+"F4.opExtrude","SWEPT_EDGE",EDGE,{"disambiguationData":[OSD([sQuery(id+"F2.wireOp",EDGE,"E684.0.6"),sQuery(id+"F2.wireOp",EDGE,"E684.0.7")])]});
            var Q161;
            Q161=makeQuery(id+"F4.opExtrude","SWEPT_EDGE",EDGE,{"disambiguationData":[OSD([sQuery(id+"F2.wireOp",EDGE,"E684.0.4"),sQuery(id+"F2.wireOp",EDGE,"E684.0.5")])]});
            var Q162;
            Q162=makeQuery(id+"F4.opExtrude","SWEPT_EDGE",EDGE,{"disambiguationData":[OSD([sQuery(id+"F2.wireOp",EDGE,"E683.0.8"),sQuery(id+"F2.wireOp",EDGE,"E683.0.9")])]});
            var Q163;
            Q163=makeQuery(id+"F4.opExtrude","SWEPT_EDGE",EDGE,{"disambiguationData":[OSD([sQuery(id+"F2.wireOp",EDGE,"E683.0.0"),sQuery(id+"F2.wireOp",EDGE,"E683.0.1")])]});
            var Q164;
            Q164=makeQuery(id+"F4.opExtrude","SWEPT_EDGE",EDGE,{"disambiguationData":[OSD([sQuery(id+"F2.wireOp",EDGE,"E682.0.6"),sQuery(id+"F2.wireOp",EDGE,"E682.0.7")])]});
            var Q165;
            Q165=makeQuery(id+"F4.opExtrude","SWEPT_EDGE",EDGE,{"disambiguationData":[OSD([sQuery(id+"F2.wireOp",EDGE,"E685.0.6"),sQuery(id+"F2.wireOp",EDGE,"E685.0.7")])]});
            var Q166;
            Q166=makeQuery(id+"F4.opExtrude","SWEPT_EDGE",EDGE,{"disambiguationData":[OSD([sQuery(id+"F2.wireOp",EDGE,"E685.0.8"),sQuery(id+"F2.wireOp",EDGE,"E685.0.9")])]});
            var Q167;
            Q167=makeQuery(id+"F4.opExtrude","SWEPT_EDGE",EDGE,{"disambiguationData":[OSD([sQuery(id+"F2.wireOp",EDGE,"E684.0.8"),sQuery(id+"F2.wireOp",EDGE,"E684.0.9")])]});
            var Q168;
            Q168=makeQuery(id+"F4.opExtrude","SWEPT_EDGE",EDGE,{"disambiguationData":[OSD([sQuery(id+"F2.wireOp",EDGE,"E688.0.6"),sQuery(id+"F2.wireOp",EDGE,"E688.0.7")])]});
            var Q169;
            Q169=makeQuery(id+"F4.opExtrude","SWEPT_EDGE",EDGE,{"disambiguationData":[OSD([sQuery(id+"F2.wireOp",EDGE,"E691.0.6"),sQuery(id+"F2.wireOp",EDGE,"E691.0.7")])]});
            var Q170;
            Q170=makeQuery(id+"F4.opExtrude","SWEPT_EDGE",EDGE,{"disambiguationData":[OSD([sQuery(id+"F2.wireOp",EDGE,"E691.0.8"),sQuery(id+"F2.wireOp",EDGE,"E691.0.9")])]});
            var Q171;
            Q171=makeQuery(id+"F4.opExtrude","SWEPT_EDGE",EDGE,{"disambiguationData":[OSD([sQuery(id+"F2.wireOp",EDGE,"E691.0.0"),sQuery(id+"F2.wireOp",EDGE,"E691.0.1")])]});
            var Q172;
            Q172=makeQuery(id+"F4.opExtrude","SWEPT_EDGE",EDGE,{"disambiguationData":[OSD([sQuery(id+"F2.wireOp",EDGE,"E699.0.6"),sQuery(id+"F2.wireOp",EDGE,"E699.0.7")])]});
            var Q173;
            Q173=makeQuery(id+"F4.opExtrude","SWEPT_EDGE",EDGE,{"disambiguationData":[OSD([sQuery(id+"F2.wireOp",EDGE,"E699.0.4"),sQuery(id+"F2.wireOp",EDGE,"E699.0.5")])]});
            var Q174;
            Q174=makeQuery(id+"F4.opExtrude","SWEPT_EDGE",EDGE,{"disambiguationData":[OSD([sQuery(id+"F2.wireOp",EDGE,"E685.0.4"),sQuery(id+"F2.wireOp",EDGE,"E685.0.5")])]});
            var Q175;
            Q175=makeQuery(id+"F4.opExtrude","SWEPT_EDGE",EDGE,{"disambiguationData":[OSD([sQuery(id+"F2.wireOp",EDGE,"E683.0.2"),sQuery(id+"F2.wireOp",EDGE,"E683.0.3")])]});
            var Q176;
            Q176=makeQuery(id+"F4.opExtrude","SWEPT_EDGE",EDGE,{"disambiguationData":[OSD([sQuery(id+"F2.wireOp",EDGE,"E690.0.0"),sQuery(id+"F2.wireOp",EDGE,"E690.0.1")])]});
            var Q177;
            Q177=makeQuery(id+"F4.opExtrude","SWEPT_EDGE",EDGE,{"disambiguationData":[OSD([sQuery(id+"F2.wireOp",EDGE,"E694.0.0"),sQuery(id+"F2.wireOp",EDGE,"E694.0.1")])]});
            var Q178;
            Q178=makeQuery(id+"F4.opExtrude","SWEPT_EDGE",EDGE,{"disambiguationData":[OSD([sQuery(id+"F2.wireOp",EDGE,"E694.0.4"),sQuery(id+"F2.wireOp",EDGE,"E694.0.5")])]});
            var Q179;
            Q179=makeQuery(id+"F4.opExtrude","SWEPT_EDGE",EDGE,{"disambiguationData":[OSD([sQuery(id+"F2.wireOp",EDGE,"E694.0.8"),sQuery(id+"F2.wireOp",EDGE,"E694.0.9")])]});
            var Q180;
            Q180=makeQuery(id+"F4.opExtrude","SWEPT_EDGE",EDGE,{"disambiguationData":[OSD([sQuery(id+"F2.wireOp",EDGE,"E699.0.0"),sQuery(id+"F2.wireOp",EDGE,"E699.0.1")])]});
            var Q181;
            Q181=makeQuery(id+"F4.opExtrude","SWEPT_EDGE",EDGE,{"disambiguationData":[OSD([sQuery(id+"F2.wireOp",EDGE,"E699.0.8"),sQuery(id+"F2.wireOp",EDGE,"E699.0.9")])]});
            var Q182;
            Q182=makeQuery(id+"F4.opExtrude","SWEPT_EDGE",EDGE,{"disambiguationData":[OSD([sQuery(id+"F2.wireOp",EDGE,"E693.0.8"),sQuery(id+"F2.wireOp",EDGE,"E693.0.9")])]});
            var Q183;
            Q183=makeQuery(id+"F4.opExtrude","SWEPT_EDGE",EDGE,{"disambiguationData":[OSD([sQuery(id+"F2.wireOp",EDGE,"E689.0.0"),sQuery(id+"F2.wireOp",EDGE,"E689.0.1")])]});
            var Q184;
            Q184=makeQuery(id+"F4.opExtrude","SWEPT_EDGE",EDGE,{"disambiguationData":[OSD([sQuery(id+"F2.wireOp",EDGE,"E689.0.8"),sQuery(id+"F2.wireOp",EDGE,"E689.0.9")])]});
            var Q185;
            Q185=makeQuery(id+"F4.opExtrude","SWEPT_EDGE",EDGE,{"disambiguationData":[OSD([sQuery(id+"F2.wireOp",EDGE,"E687.0.0"),sQuery(id+"F2.wireOp",EDGE,"E687.0.1")])]});
            var Q186;
            Q186=makeQuery(id+"F4.opExtrude","SWEPT_EDGE",EDGE,{"disambiguationData":[OSD([sQuery(id+"F2.wireOp",EDGE,"E687.0.8"),sQuery(id+"F2.wireOp",EDGE,"E687.0.9")])]});
            var Q187;
            Q187=makeQuery(id+"F4.opExtrude","SWEPT_EDGE",EDGE,{"disambiguationData":[OSD([sQuery(id+"F2.wireOp",EDGE,"E687.0.6"),sQuery(id+"F2.wireOp",EDGE,"E687.0.7")])]});
            var Q188;
            Q188=makeQuery(id+"F4.opExtrude","SWEPT_EDGE",EDGE,{"disambiguationData":[OSD([sQuery(id+"F2.wireOp",EDGE,"E686.0.0"),sQuery(id+"F2.wireOp",EDGE,"E686.0.1")])]});
            var Q189;
            Q189=makeQuery(id+"F4.opExtrude","SWEPT_EDGE",EDGE,{"disambiguationData":[OSD([sQuery(id+"F2.wireOp",EDGE,"E686.0.2"),sQuery(id+"F2.wireOp",EDGE,"E686.0.3")])]});
            var Q190;
            Q190=makeQuery(id+"F4.opExtrude","SWEPT_EDGE",EDGE,{"disambiguationData":[OSD([sQuery(id+"F2.wireOp",EDGE,"E688.0.0"),sQuery(id+"F2.wireOp",EDGE,"E688.0.1")])]});
            var Q191;
            Q191=makeQuery(id+"F4.opExtrude","SWEPT_EDGE",EDGE,{"disambiguationData":[OSD([sQuery(id+"F2.wireOp",EDGE,"E688.0.2"),sQuery(id+"F2.wireOp",EDGE,"E688.0.3")])]});
            var Q192;
            Q192=makeQuery(id+"F4.opExtrude","SWEPT_EDGE",EDGE,{"disambiguationData":[OSD([sQuery(id+"F2.wireOp",EDGE,"E688.0.8"),sQuery(id+"F2.wireOp",EDGE,"E688.0.9")])]});
            var Q193;
            Q193=makeQuery(id+"F4.opExtrude","SWEPT_EDGE",EDGE,{"disambiguationData":[OSD([sQuery(id+"F2.wireOp",EDGE,"E685.0.0"),sQuery(id+"F2.wireOp",EDGE,"E685.0.1")])]});
            var Q194;
            Q194=makeQuery(id+"F4.opExtrude","SWEPT_EDGE",EDGE,{"disambiguationData":[OSD([sQuery(id+"F2.wireOp",EDGE,"E685.0.2"),sQuery(id+"F2.wireOp",EDGE,"E685.0.3")])]});
            var Q195;
            Q195=makeQuery(id+"F4.opExtrude","SWEPT_EDGE",EDGE,{"disambiguationData":[OSD([sQuery(id+"F2.wireOp",EDGE,"E686.0.6"),sQuery(id+"F2.wireOp",EDGE,"E686.0.7")])]});
            var Q196;
            Q196=makeQuery(id+"F4.opExtrude","SWEPT_EDGE",EDGE,{"disambiguationData":[OSD([sQuery(id+"F2.wireOp",EDGE,"E686.0.8"),sQuery(id+"F2.wireOp",EDGE,"E686.0.9")])]});
            var Q197;
            Q197=makeQuery(id+"F4.opExtrude","SWEPT_EDGE",EDGE,{"disambiguationData":[OSD([sQuery(id+"F2.wireOp",EDGE,"E687.0.2"),sQuery(id+"F2.wireOp",EDGE,"E687.0.3")])]});
            var Q198;
            Q198=makeQuery(id+"F4.opExtrude","SWEPT_EDGE",EDGE,{"disambiguationData":[OSD([sQuery(id+"F2.wireOp",EDGE,"E692.0.0"),sQuery(id+"F2.wireOp",EDGE,"E692.0.1")])]});
            var Q199;
            Q199=makeQuery(id+"F4.opExtrude","SWEPT_EDGE",EDGE,{"disambiguationData":[OSD([sQuery(id+"F2.wireOp",EDGE,"E692.0.2"),sQuery(id+"F2.wireOp",EDGE,"E692.0.3")])]});
            var Q200;
            Q200=makeQuery(id+"F4.opExtrude","SWEPT_EDGE",EDGE,{"disambiguationData":[OSD([sQuery(id+"F2.wireOp",EDGE,"E692.0.8"),sQuery(id+"F2.wireOp",EDGE,"E692.0.9")])]});
            var Q201;
            Q201=makeQuery(id+"F4.opExtrude","SWEPT_EDGE",EDGE,{"disambiguationData":[OSD([sQuery(id+"F2.wireOp",EDGE,"E692.0.6"),sQuery(id+"F2.wireOp",EDGE,"E692.0.7")])]});
            var Q202;
            Q202=makeQuery(id+"F4.opExtrude","SWEPT_EDGE",EDGE,{"disambiguationData":[OSD([sQuery(id+"F2.wireOp",EDGE,"E696.0.8"),sQuery(id+"F2.wireOp",EDGE,"E696.0.9")])]});
            var Q203;
            Q203=makeQuery(id+"F4.opExtrude","SWEPT_EDGE",EDGE,{"disambiguationData":[OSD([sQuery(id+"F2.wireOp",EDGE,"E696.0.6"),sQuery(id+"F2.wireOp",EDGE,"E696.0.7")])]});
            var Q204;
            Q204=makeQuery(id+"F4.opExtrude","SWEPT_EDGE",EDGE,{"disambiguationData":[OSD([sQuery(id+"F2.wireOp",EDGE,"E696.0.0"),sQuery(id+"F2.wireOp",EDGE,"E696.0.1")])]});
            var Q205;
            Q205=makeQuery(id+"F4.opExtrude","SWEPT_EDGE",EDGE,{"disambiguationData":[OSD([sQuery(id+"F2.wireOp",EDGE,"E697.0.6"),sQuery(id+"F2.wireOp",EDGE,"E697.0.7")])]});
            var Q206;
            Q206=makeQuery(id+"F4.opExtrude","SWEPT_EDGE",EDGE,{"disambiguationData":[OSD([sQuery(id+"F2.wireOp",EDGE,"E697.0.2"),sQuery(id+"F2.wireOp",EDGE,"E697.0.3")])]});
            var Q207;
            Q207=makeQuery(id+"F4.opExtrude","SWEPT_EDGE",EDGE,{"disambiguationData":[OSD([sQuery(id+"F2.wireOp",EDGE,"E697.0.8"),sQuery(id+"F2.wireOp",EDGE,"E697.0.9")])]});
            var Q208;
            Q208=makeQuery(id+"F4.opExtrude","SWEPT_EDGE",EDGE,{"disambiguationData":[OSD([sQuery(id+"F2.wireOp",EDGE,"E693.0.0"),sQuery(id+"F2.wireOp",EDGE,"E693.0.1")])]});
            var Q209;
            Q209=makeQuery(id+"F4.opExtrude","SWEPT_EDGE",EDGE,{"disambiguationData":[OSD([sQuery(id+"F2.wireOp",EDGE,"E693.0.2"),sQuery(id+"F2.wireOp",EDGE,"E693.0.3")])]});
            var Q210;
            Q210=makeQuery(id+"F4.opExtrude","SWEPT_EDGE",EDGE,{"disambiguationData":[OSD([sQuery(id+"F2.wireOp",EDGE,"E689.0.2"),sQuery(id+"F2.wireOp",EDGE,"E689.0.3")])]});
            var Q211;
            Q211=makeQuery(id+"F4.opExtrude","SWEPT_EDGE",EDGE,{"disambiguationData":[OSD([sQuery(id+"F2.wireOp",EDGE,"E697.0.4"),sQuery(id+"F2.wireOp",EDGE,"E697.0.5")])]});
            var Q212;
            Q212=makeQuery(id+"F4.opExtrude","SWEPT_EDGE",EDGE,{"disambiguationData":[OSD([sQuery(id+"F2.wireOp",EDGE,"E700.0.0"),sQuery(id+"F2.wireOp",EDGE,"E700.0.1")])]});
            var Q213;
            Q213=makeQuery(id+"F4.opExtrude","SWEPT_EDGE",EDGE,{"disambiguationData":[OSD([sQuery(id+"F2.wireOp",EDGE,"E697.0.0"),sQuery(id+"F2.wireOp",EDGE,"E697.0.1")])]});
            var Q214;
            Q214=makeQuery(id+"F4.opExtrude","SWEPT_EDGE",EDGE,{"disambiguationData":[OSD([sQuery(id+"F2.wireOp",EDGE,"E708.0.8"),sQuery(id+"F2.wireOp",EDGE,"E708.0.9")])]});
            var Q215;
            Q215=makeQuery(id+"F4.opExtrude","SWEPT_EDGE",EDGE,{"disambiguationData":[OSD([sQuery(id+"F2.wireOp",EDGE,"E708.0.0"),sQuery(id+"F2.wireOp",EDGE,"E708.0.1")])]});
            var Q216;
            Q216=makeQuery(id+"F4.opExtrude","SWEPT_EDGE",EDGE,{"disambiguationData":[OSD([sQuery(id+"F2.wireOp",EDGE,"E709.0.4"),sQuery(id+"F2.wireOp",EDGE,"E709.0.5")])]});
            var Q217;
            Q217=makeQuery(id+"F4.opExtrude","SWEPT_EDGE",EDGE,{"disambiguationData":[OSD([sQuery(id+"F2.wireOp",EDGE,"E705.0.2"),sQuery(id+"F2.wireOp",EDGE,"E705.0.3")])]});
            var Q218;
            Q218=makeQuery(id+"F4.opExtrude","SWEPT_EDGE",EDGE,{"disambiguationData":[OSD([sQuery(id+"F2.wireOp",EDGE,"E705.0.0"),sQuery(id+"F2.wireOp",EDGE,"E705.0.1")])]});
            var Q219;
            Q219=makeQuery(id+"F4.opExtrude","SWEPT_EDGE",EDGE,{"disambiguationData":[OSD([sQuery(id+"F2.wireOp",EDGE,"E709.0.2"),sQuery(id+"F2.wireOp",EDGE,"E709.0.3")])]});
            var Q220;
            Q220=makeQuery(id+"F4.opExtrude","SWEPT_EDGE",EDGE,{"disambiguationData":[OSD([sQuery(id+"F2.wireOp",EDGE,"E709.0.0"),sQuery(id+"F2.wireOp",EDGE,"E709.0.1")])]});
            var Q221;
            Q221=makeQuery(id+"F4.opExtrude","SWEPT_EDGE",EDGE,{"disambiguationData":[OSD([sQuery(id+"F2.wireOp",EDGE,"E709.0.8"),sQuery(id+"F2.wireOp",EDGE,"E709.0.9")])]});
            var Q222;
            Q222=makeQuery(id+"F4.opExtrude","SWEPT_EDGE",EDGE,{"disambiguationData":[OSD([sQuery(id+"F2.wireOp",EDGE,"E708.0.2"),sQuery(id+"F2.wireOp",EDGE,"E708.0.3")])]});
            var Q223;
            Q223=makeQuery(id+"F4.opExtrude","SWEPT_EDGE",EDGE,{"disambiguationData":[OSD([sQuery(id+"F2.wireOp",EDGE,"E704.0.2"),sQuery(id+"F2.wireOp",EDGE,"E704.0.3")])]});
            var Q224;
            Q224=makeQuery(id+"F4.opExtrude","SWEPT_EDGE",EDGE,{"disambiguationData":[OSD([sQuery(id+"F2.wireOp",EDGE,"E698.0.2"),sQuery(id+"F2.wireOp",EDGE,"E698.0.3")])]});
            var Q225;
            Q225=makeQuery(id+"F4.opExtrude","SWEPT_EDGE",EDGE,{"disambiguationData":[OSD([sQuery(id+"F2.wireOp",EDGE,"E698.0.6"),sQuery(id+"F2.wireOp",EDGE,"E698.0.7")])]});
            var Q226;
            Q226=makeQuery(id+"F4.opExtrude","SWEPT_EDGE",EDGE,{"disambiguationData":[OSD([sQuery(id+"F2.wireOp",EDGE,"E696.0.4"),sQuery(id+"F2.wireOp",EDGE,"E696.0.5")])]});
            var Q227;
            Q227=makeQuery(id+"F4.opExtrude","SWEPT_EDGE",EDGE,{"disambiguationData":[OSD([sQuery(id+"F2.wireOp",EDGE,"E705.0.6"),sQuery(id+"F2.wireOp",EDGE,"E705.0.7")])]});
            var Q228;
            Q228=makeQuery(id+"F4.opExtrude","SWEPT_EDGE",EDGE,{"disambiguationData":[OSD([sQuery(id+"F2.wireOp",EDGE,"E709.0.6"),sQuery(id+"F2.wireOp",EDGE,"E709.0.7")])]});
            var Q229;
            Q229=makeQuery(id+"F4.opExtrude","SWEPT_EDGE",EDGE,{"disambiguationData":[OSD([sQuery(id+"F2.wireOp",EDGE,"E705.0.8"),sQuery(id+"F2.wireOp",EDGE,"E705.0.9")])]});
            var Q230;
            Q230=makeQuery(id+"F4.opExtrude","SWEPT_EDGE",EDGE,{"disambiguationData":[OSD([sQuery(id+"F2.wireOp",EDGE,"E698.0.0"),sQuery(id+"F2.wireOp",EDGE,"E698.0.1")])]});
            var Q231;
            Q231=makeQuery(id+"F4.opExtrude","SWEPT_EDGE",EDGE,{"disambiguationData":[OSD([sQuery(id+"F2.wireOp",EDGE,"E698.0.8"),sQuery(id+"F2.wireOp",EDGE,"E698.0.9")])]});
            var Q232;
            Q232=makeQuery(id+"F4.opExtrude","SWEPT_EDGE",EDGE,{"disambiguationData":[OSD([sQuery(id+"F2.wireOp",EDGE,"E696.0.2"),sQuery(id+"F2.wireOp",EDGE,"E696.0.3")])]});
            var Q233;
            Q233=makeQuery(id+"F4.opExtrude","SWEPT_EDGE",EDGE,{"disambiguationData":[OSD([sQuery(id+"F2.wireOp",EDGE,"E699.0.2"),sQuery(id+"F2.wireOp",EDGE,"E699.0.3")])]});
            var Q234;
            Q234=makeQuery(id+"F4.opExtrude","SWEPT_EDGE",EDGE,{"disambiguationData":[OSD([sQuery(id+"F2.wireOp",EDGE,"E700.0.8"),sQuery(id+"F2.wireOp",EDGE,"E700.0.9")])]});
            var Q235;
            Q235=makeQuery(id+"F4.opExtrude","SWEPT_EDGE",EDGE,{"disambiguationData":[OSD([sQuery(id+"F2.wireOp",EDGE,"E693.0.4"),sQuery(id+"F2.wireOp",EDGE,"E693.0.5")])]});
            var Q236;
            Q236=makeQuery(id+"F4.opExtrude","SWEPT_EDGE",EDGE,{"disambiguationData":[OSD([sQuery(id+"F2.wireOp",EDGE,"E693.0.6"),sQuery(id+"F2.wireOp",EDGE,"E693.0.7")])]});
            var Q237;
            Q237=makeQuery(id+"F4.opExtrude","SWEPT_EDGE",EDGE,{"disambiguationData":[OSD([sQuery(id+"F2.wireOp",EDGE,"E692.0.4"),sQuery(id+"F2.wireOp",EDGE,"E692.0.5")])]});
            var Q238;
            Q238=makeQuery(id+"F4.opExtrude","SWEPT_EDGE",EDGE,{"disambiguationData":[OSD([sQuery(id+"F2.wireOp",EDGE,"E688.0.4"),sQuery(id+"F2.wireOp",EDGE,"E688.0.5")])]});
            var Q239;
            Q239=makeQuery(id+"F4.opExtrude","SWEPT_EDGE",EDGE,{"disambiguationData":[OSD([sQuery(id+"F2.wireOp",EDGE,"E686.0.4"),sQuery(id+"F2.wireOp",EDGE,"E686.0.5")])]});
            var Q240;
            Q240=makeQuery(id+"F4.opExtrude","SWEPT_EDGE",EDGE,{"disambiguationData":[OSD([sQuery(id+"F2.wireOp",EDGE,"E689.0.4"),sQuery(id+"F2.wireOp",EDGE,"E689.0.5")])]});
            var Q241;
            Q241=makeQuery(id+"F4.opExtrude","SWEPT_EDGE",EDGE,{"disambiguationData":[OSD([sQuery(id+"F2.wireOp",EDGE,"E689.0.6"),sQuery(id+"F2.wireOp",EDGE,"E689.0.7")])]});
            var Q242;
            Q242=makeQuery(id+"F4.opExtrude","SWEPT_EDGE",EDGE,{"disambiguationData":[OSD([sQuery(id+"F2.wireOp",EDGE,"E687.0.4"),sQuery(id+"F2.wireOp",EDGE,"E687.0.5")])]});
            var Q243;
            Q243=makeQuery(id+"F4.opExtrude","SWEPT_EDGE",EDGE,{"disambiguationData":[OSD([sQuery(id+"F2.wireOp",EDGE,"E703.0.6"),sQuery(id+"F2.wireOp",EDGE,"E703.0.7")])]});
            var Q244;
            Q244=makeQuery(id+"F4.opExtrude","SWEPT_EDGE",EDGE,{"disambiguationData":[OSD([sQuery(id+"F2.wireOp",EDGE,"E691.0.2"),sQuery(id+"F2.wireOp",EDGE,"E691.0.3")])]});
            var Q245;
            Q245=makeQuery(id+"F4.opExtrude","SWEPT_EDGE",EDGE,{"disambiguationData":[OSD([sQuery(id+"F2.wireOp",EDGE,"E684.0.0"),sQuery(id+"F2.wireOp",EDGE,"E684.0.1")])]});
            var Q246;
            Q246=makeQuery(id+"F4.opExtrude","SWEPT_EDGE",EDGE,{"disambiguationData":[OSD([sQuery(id+"F2.wireOp",EDGE,"E684.0.2"),sQuery(id+"F2.wireOp",EDGE,"E684.0.3")])]});
            var Q247;
            Q247=makeQuery(id+"F4.opExtrude","SWEPT_EDGE",EDGE,{"disambiguationData":[OSD([sQuery(id+"F2.wireOp",EDGE,"E694.0.6"),sQuery(id+"F2.wireOp",EDGE,"E694.0.7")])]});
            var Q248;
            Q248=makeQuery(id+"F4.opExtrude","SWEPT_EDGE",EDGE,{"disambiguationData":[OSD([sQuery(id+"F2.wireOp",EDGE,"E677.0.8"),sQuery(id+"F2.wireOp",EDGE,"E677.0.9")])]});
            fillet(context, id + "F5", {"entities" : qUnion([Q0, Q1, Q2, Q3, Q4, Q5, Q6, Q7, Q8, Q9, Q10, Q11, Q12, Q13, Q14, Q15, Q16, Q17, Q18, Q19, Q20, Q21, Q22, Q23, Q24, Q25, Q26, Q27, Q28, Q29, Q30, Q31, Q32, Q33, Q34, Q35, Q36, Q37, Q38, Q39, Q40, Q41, Q42, Q43, Q44, Q45, Q46, Q47, Q48, Q49, Q50, Q51, Q52, Q53, Q54, Q55, Q56, Q57, Q58, Q59, Q60, Q61, Q62, Q63, Q64, Q65, Q66, Q67, Q68, Q69, Q70, Q71, Q72, Q73, Q74, Q75, Q76, Q77, Q78, Q79, Q80, Q81, Q82, Q83, Q84, Q85, Q86, Q87, Q88, Q89, Q90, Q91, Q92, Q93, Q94, Q95, Q96, Q97, Q98, Q99, Q100, Q101, Q102, Q103, Q104, Q105, Q106, Q107, Q108, Q109, Q110, Q111, Q112, Q113, Q114, Q115, Q116, Q117, Q118, Q119, Q120, Q121, Q122, Q123, Q124, Q125, Q126, Q127, Q128, Q129, Q130, Q131, Q132, Q133, Q134, Q135, Q136, Q137, Q138, Q139, Q140, Q141, Q142, Q143, Q144, Q145, Q146, Q147, Q148, Q149, Q150, Q151, Q152, Q153, Q154, Q155, Q156, Q157, Q158, Q159, Q160, Q161, Q162, Q163, Q164, Q165, Q166, Q167, Q168, Q169, Q170, Q171, Q172, Q173, Q174, Q175, Q176, Q177, Q178, Q179, Q180, Q181, Q182, Q183, Q184, Q185, Q186, Q187, Q188, Q189, Q190, Q191, Q192, Q193, Q194, Q195, Q196, Q197, Q198, Q199, Q200, Q201, Q202, Q203, Q204, Q205, Q206, Q207, Q208, Q209, Q210, Q211, Q212, Q213, Q214, Q215, Q216, Q217, Q218, Q219, Q220, Q221, Q222, Q223, Q224, Q225, Q226, Q227, Q228, Q229, Q230, Q231, Q232, Q233, Q234, Q235, Q236, Q237, Q238, Q239, Q240, Q241, Q242, Q243, Q244, Q245, Q246, Q247, Q248]), "radius" : 3.17 * mm, "tangentPropagation" : true});
        }
        {
            var Q0;
            Q0=makeQuery(id+"F4.opExtrude","SWEPT_BODY",BODY,{"disambiguationData":[OSD([sQuery(id+"F2.wireOp",EDGE,"E660.0.0"),sQuery(id+"F2.wireOp",EDGE,"E660.0.1"),sQuery(id+"F2.wireOp",EDGE,"E660.0.2"),sQuery(id+"F2.wireOp",EDGE,"E660.0.3"),sQuery(id+"F2.wireOp",EDGE,"E660.0.4"),sQuery(id+"F2.wireOp",EDGE,"E660.0.5"),sQuery(id+"F2.wireOp",EDGE,"E660.0.6"),sQuery(id+"F2.wireOp",EDGE,"E660.0.7"),sQuery(id+"F2.wireOp",EDGE,"E660.0.8"),sQuery(id+"F2.wireOp",EDGE,"E660.0.9")])]});
            var Q1;
            Q1=makeQuery(id+"F4.opExtrude","SWEPT_BODY",BODY,{"disambiguationData":[OSD([sQuery(id+"F2.wireOp",EDGE,"E661.0.0"),sQuery(id+"F2.wireOp",EDGE,"E661.0.1"),sQuery(id+"F2.wireOp",EDGE,"E661.0.2"),sQuery(id+"F2.wireOp",EDGE,"E661.0.3"),sQuery(id+"F2.wireOp",EDGE,"E661.0.4"),sQuery(id+"F2.wireOp",EDGE,"E661.0.5"),sQuery(id+"F2.wireOp",EDGE,"E661.0.6"),sQuery(id+"F2.wireOp",EDGE,"E661.0.7"),sQuery(id+"F2.wireOp",EDGE,"E661.0.8"),sQuery(id+"F2.wireOp",EDGE,"E661.0.9")])]});
            var Q2;
            Q2=makeQuery(id+"F4.opExtrude","SWEPT_BODY",BODY,{"disambiguationData":[OSD([sQuery(id+"F2.wireOp",EDGE,"E670.0.0"),sQuery(id+"F2.wireOp",EDGE,"E670.0.1"),sQuery(id+"F2.wireOp",EDGE,"E670.0.2"),sQuery(id+"F2.wireOp",EDGE,"E670.0.3"),sQuery(id+"F2.wireOp",EDGE,"E670.0.4"),sQuery(id+"F2.wireOp",EDGE,"E670.0.5"),sQuery(id+"F2.wireOp",EDGE,"E670.0.6"),sQuery(id+"F2.wireOp",EDGE,"E670.0.7"),sQuery(id+"F2.wireOp",EDGE,"E670.0.8"),sQuery(id+"F2.wireOp",EDGE,"E670.0.9")])]});
            var Q3;
            Q3=makeQuery(id+"F4.opExtrude","SWEPT_BODY",BODY,{"disambiguationData":[OSD([sQuery(id+"F2.wireOp",EDGE,"E671.0.0"),sQuery(id+"F2.wireOp",EDGE,"E671.0.1"),sQuery(id+"F2.wireOp",EDGE,"E671.0.2"),sQuery(id+"F2.wireOp",EDGE,"E671.0.3"),sQuery(id+"F2.wireOp",EDGE,"E671.0.4"),sQuery(id+"F2.wireOp",EDGE,"E671.0.5"),sQuery(id+"F2.wireOp",EDGE,"E671.0.6"),sQuery(id+"F2.wireOp",EDGE,"E671.0.7"),sQuery(id+"F2.wireOp",EDGE,"E671.0.8"),sQuery(id+"F2.wireOp",EDGE,"E671.0.9")])]});
            var Q4;
            Q4=makeQuery(id+"F4.opExtrude","SWEPT_BODY",BODY,{"disambiguationData":[OSD([sQuery(id+"F2.wireOp",EDGE,"E682.0.0"),sQuery(id+"F2.wireOp",EDGE,"E682.0.1"),sQuery(id+"F2.wireOp",EDGE,"E682.0.2"),sQuery(id+"F2.wireOp",EDGE,"E682.0.3"),sQuery(id+"F2.wireOp",EDGE,"E682.0.4"),sQuery(id+"F2.wireOp",EDGE,"E682.0.5"),sQuery(id+"F2.wireOp",EDGE,"E682.0.6"),sQuery(id+"F2.wireOp",EDGE,"E682.0.7"),sQuery(id+"F2.wireOp",EDGE,"E682.0.8"),sQuery(id+"F2.wireOp",EDGE,"E682.0.9")])]});
            var Q5;
            Q5=makeQuery(id+"F4.opExtrude","SWEPT_BODY",BODY,{"disambiguationData":[OSD([sQuery(id+"F2.wireOp",EDGE,"E672.0.0"),sQuery(id+"F2.wireOp",EDGE,"E672.0.1"),sQuery(id+"F2.wireOp",EDGE,"E672.0.2"),sQuery(id+"F2.wireOp",EDGE,"E672.0.3"),sQuery(id+"F2.wireOp",EDGE,"E672.0.4"),sQuery(id+"F2.wireOp",EDGE,"E672.0.5"),sQuery(id+"F2.wireOp",EDGE,"E672.0.6"),sQuery(id+"F2.wireOp",EDGE,"E672.0.7"),sQuery(id+"F2.wireOp",EDGE,"E672.0.8"),sQuery(id+"F2.wireOp",EDGE,"E672.0.9")])]});
            var Q6;
            Q6=makeQuery(id+"F4.opExtrude","SWEPT_BODY",BODY,{"disambiguationData":[OSD([sQuery(id+"F2.wireOp",EDGE,"E662.0.0"),sQuery(id+"F2.wireOp",EDGE,"E662.0.1"),sQuery(id+"F2.wireOp",EDGE,"E662.0.2"),sQuery(id+"F2.wireOp",EDGE,"E662.0.3"),sQuery(id+"F2.wireOp",EDGE,"E662.0.4"),sQuery(id+"F2.wireOp",EDGE,"E662.0.5"),sQuery(id+"F2.wireOp",EDGE,"E662.0.6"),sQuery(id+"F2.wireOp",EDGE,"E662.0.7"),sQuery(id+"F2.wireOp",EDGE,"E662.0.8"),sQuery(id+"F2.wireOp",EDGE,"E662.0.9")])]});
            var Q7;
            Q7=makeQuery(id+"F4.opExtrude","SWEPT_BODY",BODY,{"disambiguationData":[OSD([sQuery(id+"F2.wireOp",EDGE,"E669.0.0"),sQuery(id+"F2.wireOp",EDGE,"E669.0.1"),sQuery(id+"F2.wireOp",EDGE,"E669.0.2"),sQuery(id+"F2.wireOp",EDGE,"E669.0.3"),sQuery(id+"F2.wireOp",EDGE,"E669.0.4"),sQuery(id+"F2.wireOp",EDGE,"E669.0.5"),sQuery(id+"F2.wireOp",EDGE,"E669.0.6"),sQuery(id+"F2.wireOp",EDGE,"E669.0.7"),sQuery(id+"F2.wireOp",EDGE,"E669.0.8"),sQuery(id+"F2.wireOp",EDGE,"E669.0.9")])]});
            var Q8;
            Q8=makeQuery(id+"F4.opExtrude","SWEPT_BODY",BODY,{"disambiguationData":[OSD([sQuery(id+"F2.wireOp",EDGE,"E663.0.0"),sQuery(id+"F2.wireOp",EDGE,"E663.0.1"),sQuery(id+"F2.wireOp",EDGE,"E663.0.2"),sQuery(id+"F2.wireOp",EDGE,"E663.0.3"),sQuery(id+"F2.wireOp",EDGE,"E663.0.4"),sQuery(id+"F2.wireOp",EDGE,"E663.0.5"),sQuery(id+"F2.wireOp",EDGE,"E663.0.6"),sQuery(id+"F2.wireOp",EDGE,"E663.0.7"),sQuery(id+"F2.wireOp",EDGE,"E663.0.8"),sQuery(id+"F2.wireOp",EDGE,"E663.0.9")])]});
            var Q9;
            Q9=makeQuery(id+"F4.opExtrude","SWEPT_BODY",BODY,{"disambiguationData":[OSD([sQuery(id+"F2.wireOp",EDGE,"E668.0.0"),sQuery(id+"F2.wireOp",EDGE,"E668.0.1"),sQuery(id+"F2.wireOp",EDGE,"E668.0.2"),sQuery(id+"F2.wireOp",EDGE,"E668.0.3"),sQuery(id+"F2.wireOp",EDGE,"E668.0.4"),sQuery(id+"F2.wireOp",EDGE,"E668.0.5"),sQuery(id+"F2.wireOp",EDGE,"E668.0.6"),sQuery(id+"F2.wireOp",EDGE,"E668.0.7"),sQuery(id+"F2.wireOp",EDGE,"E668.0.8"),sQuery(id+"F2.wireOp",EDGE,"E668.0.9")])]});
            var Q10;
            Q10=makeQuery(id+"F4.opExtrude","SWEPT_BODY",BODY,{"disambiguationData":[OSD([sQuery(id+"F2.wireOp",EDGE,"E673.0.0"),sQuery(id+"F2.wireOp",EDGE,"E673.0.1"),sQuery(id+"F2.wireOp",EDGE,"E673.0.2"),sQuery(id+"F2.wireOp",EDGE,"E673.0.3"),sQuery(id+"F2.wireOp",EDGE,"E673.0.4"),sQuery(id+"F2.wireOp",EDGE,"E673.0.5"),sQuery(id+"F2.wireOp",EDGE,"E673.0.6"),sQuery(id+"F2.wireOp",EDGE,"E673.0.7"),sQuery(id+"F2.wireOp",EDGE,"E673.0.8"),sQuery(id+"F2.wireOp",EDGE,"E673.0.9")])]});
            var Q11;
            Q11=makeQuery(id+"F4.opExtrude","SWEPT_BODY",BODY,{"disambiguationData":[OSD([sQuery(id+"F2.wireOp",EDGE,"E678.0.0"),sQuery(id+"F2.wireOp",EDGE,"E678.0.1"),sQuery(id+"F2.wireOp",EDGE,"E678.0.2"),sQuery(id+"F2.wireOp",EDGE,"E678.0.3"),sQuery(id+"F2.wireOp",EDGE,"E678.0.4"),sQuery(id+"F2.wireOp",EDGE,"E678.0.5"),sQuery(id+"F2.wireOp",EDGE,"E678.0.6"),sQuery(id+"F2.wireOp",EDGE,"E678.0.7"),sQuery(id+"F2.wireOp",EDGE,"E678.0.8"),sQuery(id+"F2.wireOp",EDGE,"E678.0.9")])]});
            var Q12;
            Q12=makeQuery(id+"F4.opExtrude","SWEPT_BODY",BODY,{"disambiguationData":[OSD([sQuery(id+"F2.wireOp",EDGE,"E677.0.0"),sQuery(id+"F2.wireOp",EDGE,"E677.0.1"),sQuery(id+"F2.wireOp",EDGE,"E677.0.2"),sQuery(id+"F2.wireOp",EDGE,"E677.0.3"),sQuery(id+"F2.wireOp",EDGE,"E677.0.4"),sQuery(id+"F2.wireOp",EDGE,"E677.0.5"),sQuery(id+"F2.wireOp",EDGE,"E677.0.6"),sQuery(id+"F2.wireOp",EDGE,"E677.0.7"),sQuery(id+"F2.wireOp",EDGE,"E677.0.8"),sQuery(id+"F2.wireOp",EDGE,"E677.0.9")])]});
            var Q13;
            Q13=makeQuery(id+"F4.opExtrude","SWEPT_BODY",BODY,{"disambiguationData":[OSD([sQuery(id+"F2.wireOp",EDGE,"E683.0.0"),sQuery(id+"F2.wireOp",EDGE,"E683.0.1"),sQuery(id+"F2.wireOp",EDGE,"E683.0.2"),sQuery(id+"F2.wireOp",EDGE,"E683.0.3"),sQuery(id+"F2.wireOp",EDGE,"E683.0.4"),sQuery(id+"F2.wireOp",EDGE,"E683.0.5"),sQuery(id+"F2.wireOp",EDGE,"E683.0.6"),sQuery(id+"F2.wireOp",EDGE,"E683.0.7"),sQuery(id+"F2.wireOp",EDGE,"E683.0.8"),sQuery(id+"F2.wireOp",EDGE,"E683.0.9")])]});
            var Q14;
            Q14=makeQuery(id+"F4.opExtrude","SWEPT_BODY",BODY,{"disambiguationData":[OSD([sQuery(id+"F2.wireOp",EDGE,"E684.0.0"),sQuery(id+"F2.wireOp",EDGE,"E684.0.1"),sQuery(id+"F2.wireOp",EDGE,"E684.0.2"),sQuery(id+"F2.wireOp",EDGE,"E684.0.3"),sQuery(id+"F2.wireOp",EDGE,"E684.0.4"),sQuery(id+"F2.wireOp",EDGE,"E684.0.5"),sQuery(id+"F2.wireOp",EDGE,"E684.0.6"),sQuery(id+"F2.wireOp",EDGE,"E684.0.7"),sQuery(id+"F2.wireOp",EDGE,"E684.0.8"),sQuery(id+"F2.wireOp",EDGE,"E684.0.9")])]});
            var Q15;
            Q15=makeQuery(id+"F4.opExtrude","SWEPT_BODY",BODY,{"disambiguationData":[OSD([sQuery(id+"F2.wireOp",EDGE,"E685.0.0"),sQuery(id+"F2.wireOp",EDGE,"E685.0.1"),sQuery(id+"F2.wireOp",EDGE,"E685.0.2"),sQuery(id+"F2.wireOp",EDGE,"E685.0.3"),sQuery(id+"F2.wireOp",EDGE,"E685.0.4"),sQuery(id+"F2.wireOp",EDGE,"E685.0.5"),sQuery(id+"F2.wireOp",EDGE,"E685.0.6"),sQuery(id+"F2.wireOp",EDGE,"E685.0.7"),sQuery(id+"F2.wireOp",EDGE,"E685.0.8"),sQuery(id+"F2.wireOp",EDGE,"E685.0.9")])]});
            var Q16;
            Q16=makeQuery(id+"F4.opExtrude","SWEPT_BODY",BODY,{"disambiguationData":[OSD([sQuery(id+"F2.wireOp",EDGE,"E664.0.0"),sQuery(id+"F2.wireOp",EDGE,"E664.0.1"),sQuery(id+"F2.wireOp",EDGE,"E664.0.2"),sQuery(id+"F2.wireOp",EDGE,"E664.0.3"),sQuery(id+"F2.wireOp",EDGE,"E664.0.4"),sQuery(id+"F2.wireOp",EDGE,"E664.0.5"),sQuery(id+"F2.wireOp",EDGE,"E664.0.6"),sQuery(id+"F2.wireOp",EDGE,"E664.0.7"),sQuery(id+"F2.wireOp",EDGE,"E664.0.8"),sQuery(id+"F2.wireOp",EDGE,"E664.0.9")])]});
            var Q17;
            Q17=makeQuery(id+"F4.opExtrude","SWEPT_BODY",BODY,{"disambiguationData":[OSD([sQuery(id+"F2.wireOp",EDGE,"E667.0.0"),sQuery(id+"F2.wireOp",EDGE,"E667.0.1"),sQuery(id+"F2.wireOp",EDGE,"E667.0.2"),sQuery(id+"F2.wireOp",EDGE,"E667.0.3"),sQuery(id+"F2.wireOp",EDGE,"E667.0.4"),sQuery(id+"F2.wireOp",EDGE,"E667.0.5"),sQuery(id+"F2.wireOp",EDGE,"E667.0.6"),sQuery(id+"F2.wireOp",EDGE,"E667.0.7"),sQuery(id+"F2.wireOp",EDGE,"E667.0.8"),sQuery(id+"F2.wireOp",EDGE,"E667.0.9")])]});
            var Q18;
            Q18=makeQuery(id+"F4.opExtrude","SWEPT_BODY",BODY,{"disambiguationData":[OSD([sQuery(id+"F2.wireOp",EDGE,"E674.0.0"),sQuery(id+"F2.wireOp",EDGE,"E674.0.1"),sQuery(id+"F2.wireOp",EDGE,"E674.0.2"),sQuery(id+"F2.wireOp",EDGE,"E674.0.3"),sQuery(id+"F2.wireOp",EDGE,"E674.0.4"),sQuery(id+"F2.wireOp",EDGE,"E674.0.5"),sQuery(id+"F2.wireOp",EDGE,"E674.0.6"),sQuery(id+"F2.wireOp",EDGE,"E674.0.7"),sQuery(id+"F2.wireOp",EDGE,"E674.0.8"),sQuery(id+"F2.wireOp",EDGE,"E674.0.9")])]});
            var Q19;
            Q19=makeQuery(id+"F4.opExtrude","SWEPT_BODY",BODY,{"disambiguationData":[OSD([sQuery(id+"F2.wireOp",EDGE,"E679.0.0"),sQuery(id+"F2.wireOp",EDGE,"E679.0.1"),sQuery(id+"F2.wireOp",EDGE,"E679.0.2"),sQuery(id+"F2.wireOp",EDGE,"E679.0.3"),sQuery(id+"F2.wireOp",EDGE,"E679.0.4"),sQuery(id+"F2.wireOp",EDGE,"E679.0.5"),sQuery(id+"F2.wireOp",EDGE,"E679.0.6"),sQuery(id+"F2.wireOp",EDGE,"E679.0.7"),sQuery(id+"F2.wireOp",EDGE,"E679.0.8"),sQuery(id+"F2.wireOp",EDGE,"E679.0.9")])]});
            var Q20;
            Q20=makeQuery(id+"F4.opExtrude","SWEPT_BODY",BODY,{"disambiguationData":[OSD([sQuery(id+"F2.wireOp",EDGE,"E690.0.0"),sQuery(id+"F2.wireOp",EDGE,"E690.0.1"),sQuery(id+"F2.wireOp",EDGE,"E690.0.2"),sQuery(id+"F2.wireOp",EDGE,"E690.0.3"),sQuery(id+"F2.wireOp",EDGE,"E690.0.4"),sQuery(id+"F2.wireOp",EDGE,"E690.0.5"),sQuery(id+"F2.wireOp",EDGE,"E690.0.6"),sQuery(id+"F2.wireOp",EDGE,"E690.0.7"),sQuery(id+"F2.wireOp",EDGE,"E690.0.8"),sQuery(id+"F2.wireOp",EDGE,"E690.0.9")])]});
            var Q21;
            Q21=makeQuery(id+"F4.opExtrude","SWEPT_BODY",BODY,{"disambiguationData":[OSD([sQuery(id+"F2.wireOp",EDGE,"E691.0.0"),sQuery(id+"F2.wireOp",EDGE,"E691.0.1"),sQuery(id+"F2.wireOp",EDGE,"E691.0.2"),sQuery(id+"F2.wireOp",EDGE,"E691.0.3"),sQuery(id+"F2.wireOp",EDGE,"E691.0.4"),sQuery(id+"F2.wireOp",EDGE,"E691.0.5"),sQuery(id+"F2.wireOp",EDGE,"E691.0.6"),sQuery(id+"F2.wireOp",EDGE,"E691.0.7"),sQuery(id+"F2.wireOp",EDGE,"E691.0.8"),sQuery(id+"F2.wireOp",EDGE,"E691.0.9")])]});
            var Q22;
            Q22=makeQuery(id+"F4.opExtrude","SWEPT_BODY",BODY,{"disambiguationData":[OSD([sQuery(id+"F2.wireOp",EDGE,"E688.0.0"),sQuery(id+"F2.wireOp",EDGE,"E688.0.1"),sQuery(id+"F2.wireOp",EDGE,"E688.0.2"),sQuery(id+"F2.wireOp",EDGE,"E688.0.3"),sQuery(id+"F2.wireOp",EDGE,"E688.0.4"),sQuery(id+"F2.wireOp",EDGE,"E688.0.5"),sQuery(id+"F2.wireOp",EDGE,"E688.0.6"),sQuery(id+"F2.wireOp",EDGE,"E688.0.7"),sQuery(id+"F2.wireOp",EDGE,"E688.0.8"),sQuery(id+"F2.wireOp",EDGE,"E688.0.9")])]});
            var Q23;
            Q23=makeQuery(id+"F4.opExtrude","SWEPT_BODY",BODY,{"disambiguationData":[OSD([sQuery(id+"F2.wireOp",EDGE,"E686.0.0"),sQuery(id+"F2.wireOp",EDGE,"E686.0.1"),sQuery(id+"F2.wireOp",EDGE,"E686.0.2"),sQuery(id+"F2.wireOp",EDGE,"E686.0.3"),sQuery(id+"F2.wireOp",EDGE,"E686.0.4"),sQuery(id+"F2.wireOp",EDGE,"E686.0.5"),sQuery(id+"F2.wireOp",EDGE,"E686.0.6"),sQuery(id+"F2.wireOp",EDGE,"E686.0.7"),sQuery(id+"F2.wireOp",EDGE,"E686.0.8"),sQuery(id+"F2.wireOp",EDGE,"E686.0.9")])]});
            var Q24;
            Q24=makeQuery(id+"F4.opExtrude","SWEPT_BODY",BODY,{"disambiguationData":[OSD([sQuery(id+"F2.wireOp",EDGE,"E687.0.0"),sQuery(id+"F2.wireOp",EDGE,"E687.0.1"),sQuery(id+"F2.wireOp",EDGE,"E687.0.2"),sQuery(id+"F2.wireOp",EDGE,"E687.0.3"),sQuery(id+"F2.wireOp",EDGE,"E687.0.4"),sQuery(id+"F2.wireOp",EDGE,"E687.0.5"),sQuery(id+"F2.wireOp",EDGE,"E687.0.6"),sQuery(id+"F2.wireOp",EDGE,"E687.0.7"),sQuery(id+"F2.wireOp",EDGE,"E687.0.8"),sQuery(id+"F2.wireOp",EDGE,"E687.0.9")])]});
            var Q25;
            Q25=makeQuery(id+"F4.opExtrude","SWEPT_BODY",BODY,{"disambiguationData":[OSD([sQuery(id+"F2.wireOp",EDGE,"E665.0.0"),sQuery(id+"F2.wireOp",EDGE,"E665.0.1"),sQuery(id+"F2.wireOp",EDGE,"E665.0.2"),sQuery(id+"F2.wireOp",EDGE,"E665.0.3"),sQuery(id+"F2.wireOp",EDGE,"E665.0.4"),sQuery(id+"F2.wireOp",EDGE,"E665.0.5"),sQuery(id+"F2.wireOp",EDGE,"E665.0.6"),sQuery(id+"F2.wireOp",EDGE,"E665.0.7"),sQuery(id+"F2.wireOp",EDGE,"E665.0.8"),sQuery(id+"F2.wireOp",EDGE,"E665.0.9")])]});
            var Q26;
            Q26=makeQuery(id+"F4.opExtrude","SWEPT_BODY",BODY,{"disambiguationData":[OSD([sQuery(id+"F2.wireOp",EDGE,"E666.0.0"),sQuery(id+"F2.wireOp",EDGE,"E666.0.1"),sQuery(id+"F2.wireOp",EDGE,"E666.0.2"),sQuery(id+"F2.wireOp",EDGE,"E666.0.3"),sQuery(id+"F2.wireOp",EDGE,"E666.0.4"),sQuery(id+"F2.wireOp",EDGE,"E666.0.5"),sQuery(id+"F2.wireOp",EDGE,"E666.0.6"),sQuery(id+"F2.wireOp",EDGE,"E666.0.7"),sQuery(id+"F2.wireOp",EDGE,"E666.0.8"),sQuery(id+"F2.wireOp",EDGE,"E666.0.9")])]});
            var Q27;
            Q27=makeQuery(id+"F4.opExtrude","SWEPT_BODY",BODY,{"disambiguationData":[OSD([sQuery(id+"F2.wireOp",EDGE,"E675.0.0"),sQuery(id+"F2.wireOp",EDGE,"E675.0.1"),sQuery(id+"F2.wireOp",EDGE,"E675.0.2"),sQuery(id+"F2.wireOp",EDGE,"E675.0.3"),sQuery(id+"F2.wireOp",EDGE,"E675.0.4"),sQuery(id+"F2.wireOp",EDGE,"E675.0.5"),sQuery(id+"F2.wireOp",EDGE,"E675.0.6"),sQuery(id+"F2.wireOp",EDGE,"E675.0.7"),sQuery(id+"F2.wireOp",EDGE,"E675.0.8"),sQuery(id+"F2.wireOp",EDGE,"E675.0.9")])]});
            var Q28;
            Q28=makeQuery(id+"F4.opExtrude","SWEPT_BODY",BODY,{"disambiguationData":[OSD([sQuery(id+"F2.wireOp",EDGE,"E680.0.0"),sQuery(id+"F2.wireOp",EDGE,"E680.0.1"),sQuery(id+"F2.wireOp",EDGE,"E680.0.2"),sQuery(id+"F2.wireOp",EDGE,"E680.0.3"),sQuery(id+"F2.wireOp",EDGE,"E680.0.4"),sQuery(id+"F2.wireOp",EDGE,"E680.0.5"),sQuery(id+"F2.wireOp",EDGE,"E680.0.6"),sQuery(id+"F2.wireOp",EDGE,"E680.0.7"),sQuery(id+"F2.wireOp",EDGE,"E680.0.8"),sQuery(id+"F2.wireOp",EDGE,"E680.0.9")])]});
            var Q29;
            Q29=makeQuery(id+"F4.opExtrude","SWEPT_BODY",BODY,{"disambiguationData":[OSD([sQuery(id+"F2.wireOp",EDGE,"E695.0.0"),sQuery(id+"F2.wireOp",EDGE,"E695.0.1"),sQuery(id+"F2.wireOp",EDGE,"E695.0.2"),sQuery(id+"F2.wireOp",EDGE,"E695.0.3"),sQuery(id+"F2.wireOp",EDGE,"E695.0.4"),sQuery(id+"F2.wireOp",EDGE,"E695.0.5"),sQuery(id+"F2.wireOp",EDGE,"E695.0.6"),sQuery(id+"F2.wireOp",EDGE,"E695.0.7"),sQuery(id+"F2.wireOp",EDGE,"E695.0.8"),sQuery(id+"F2.wireOp",EDGE,"E695.0.9")])]});
            var Q30;
            Q30=makeQuery(id+"F4.opExtrude","SWEPT_BODY",BODY,{"disambiguationData":[OSD([sQuery(id+"F2.wireOp",EDGE,"E694.0.0"),sQuery(id+"F2.wireOp",EDGE,"E694.0.1"),sQuery(id+"F2.wireOp",EDGE,"E694.0.2"),sQuery(id+"F2.wireOp",EDGE,"E694.0.3"),sQuery(id+"F2.wireOp",EDGE,"E694.0.4"),sQuery(id+"F2.wireOp",EDGE,"E694.0.5"),sQuery(id+"F2.wireOp",EDGE,"E694.0.6"),sQuery(id+"F2.wireOp",EDGE,"E694.0.7"),sQuery(id+"F2.wireOp",EDGE,"E694.0.8"),sQuery(id+"F2.wireOp",EDGE,"E694.0.9")])]});
            var Q31;
            Q31=makeQuery(id+"F4.opExtrude","SWEPT_BODY",BODY,{"disambiguationData":[OSD([sQuery(id+"F2.wireOp",EDGE,"E699.0.0"),sQuery(id+"F2.wireOp",EDGE,"E699.0.1"),sQuery(id+"F2.wireOp",EDGE,"E699.0.2"),sQuery(id+"F2.wireOp",EDGE,"E699.0.3"),sQuery(id+"F2.wireOp",EDGE,"E699.0.4"),sQuery(id+"F2.wireOp",EDGE,"E699.0.5"),sQuery(id+"F2.wireOp",EDGE,"E699.0.6"),sQuery(id+"F2.wireOp",EDGE,"E699.0.7"),sQuery(id+"F2.wireOp",EDGE,"E699.0.8"),sQuery(id+"F2.wireOp",EDGE,"E699.0.9")])]});
            var Q32;
            Q32=makeQuery(id+"F4.opExtrude","SWEPT_BODY",BODY,{"disambiguationData":[OSD([sQuery(id+"F2.wireOp",EDGE,"E692.0.0"),sQuery(id+"F2.wireOp",EDGE,"E692.0.1"),sQuery(id+"F2.wireOp",EDGE,"E692.0.2"),sQuery(id+"F2.wireOp",EDGE,"E692.0.3"),sQuery(id+"F2.wireOp",EDGE,"E692.0.4"),sQuery(id+"F2.wireOp",EDGE,"E692.0.5"),sQuery(id+"F2.wireOp",EDGE,"E692.0.6"),sQuery(id+"F2.wireOp",EDGE,"E692.0.7"),sQuery(id+"F2.wireOp",EDGE,"E692.0.8"),sQuery(id+"F2.wireOp",EDGE,"E692.0.9")])]});
            var Q33;
            Q33=makeQuery(id+"F4.opExtrude","SWEPT_BODY",BODY,{"disambiguationData":[OSD([sQuery(id+"F2.wireOp",EDGE,"E676.0.0"),sQuery(id+"F2.wireOp",EDGE,"E676.0.1"),sQuery(id+"F2.wireOp",EDGE,"E676.0.2"),sQuery(id+"F2.wireOp",EDGE,"E676.0.3"),sQuery(id+"F2.wireOp",EDGE,"E676.0.4"),sQuery(id+"F2.wireOp",EDGE,"E676.0.5"),sQuery(id+"F2.wireOp",EDGE,"E676.0.6"),sQuery(id+"F2.wireOp",EDGE,"E676.0.7"),sQuery(id+"F2.wireOp",EDGE,"E676.0.8"),sQuery(id+"F2.wireOp",EDGE,"E676.0.9")])]});
            var Q34;
            Q34=makeQuery(id+"F4.opExtrude","SWEPT_BODY",BODY,{"disambiguationData":[OSD([sQuery(id+"F2.wireOp",EDGE,"E681.0.0"),sQuery(id+"F2.wireOp",EDGE,"E681.0.1"),sQuery(id+"F2.wireOp",EDGE,"E681.0.2"),sQuery(id+"F2.wireOp",EDGE,"E681.0.3"),sQuery(id+"F2.wireOp",EDGE,"E681.0.4"),sQuery(id+"F2.wireOp",EDGE,"E681.0.5"),sQuery(id+"F2.wireOp",EDGE,"E681.0.6"),sQuery(id+"F2.wireOp",EDGE,"E681.0.7"),sQuery(id+"F2.wireOp",EDGE,"E681.0.8"),sQuery(id+"F2.wireOp",EDGE,"E681.0.9")])]});
            var Q35;
            Q35=makeQuery(id+"F4.opExtrude","SWEPT_BODY",BODY,{"disambiguationData":[OSD([sQuery(id+"F2.wireOp",EDGE,"E706.0.0"),sQuery(id+"F2.wireOp",EDGE,"E706.0.1"),sQuery(id+"F2.wireOp",EDGE,"E706.0.2"),sQuery(id+"F2.wireOp",EDGE,"E706.0.3"),sQuery(id+"F2.wireOp",EDGE,"E706.0.4"),sQuery(id+"F2.wireOp",EDGE,"E706.0.5"),sQuery(id+"F2.wireOp",EDGE,"E706.0.6"),sQuery(id+"F2.wireOp",EDGE,"E706.0.7"),sQuery(id+"F2.wireOp",EDGE,"E706.0.8"),sQuery(id+"F2.wireOp",EDGE,"E706.0.9")])]});
            var Q36;
            Q36=makeQuery(id+"F4.opExtrude","SWEPT_BODY",BODY,{"disambiguationData":[OSD([sQuery(id+"F2.wireOp",EDGE,"E701.0.0"),sQuery(id+"F2.wireOp",EDGE,"E701.0.1"),sQuery(id+"F2.wireOp",EDGE,"E701.0.2"),sQuery(id+"F2.wireOp",EDGE,"E701.0.3"),sQuery(id+"F2.wireOp",EDGE,"E701.0.4"),sQuery(id+"F2.wireOp",EDGE,"E701.0.5"),sQuery(id+"F2.wireOp",EDGE,"E701.0.6"),sQuery(id+"F2.wireOp",EDGE,"E701.0.7"),sQuery(id+"F2.wireOp",EDGE,"E701.0.8"),sQuery(id+"F2.wireOp",EDGE,"E701.0.9")])]});
            var Q37;
            Q37=makeQuery(id+"F4.opExtrude","SWEPT_BODY",BODY,{"disambiguationData":[OSD([sQuery(id+"F2.wireOp",EDGE,"E700.0.0"),sQuery(id+"F2.wireOp",EDGE,"E700.0.1"),sQuery(id+"F2.wireOp",EDGE,"E700.0.2"),sQuery(id+"F2.wireOp",EDGE,"E700.0.3"),sQuery(id+"F2.wireOp",EDGE,"E700.0.4"),sQuery(id+"F2.wireOp",EDGE,"E700.0.5"),sQuery(id+"F2.wireOp",EDGE,"E700.0.6"),sQuery(id+"F2.wireOp",EDGE,"E700.0.7"),sQuery(id+"F2.wireOp",EDGE,"E700.0.8"),sQuery(id+"F2.wireOp",EDGE,"E700.0.9")])]});
            var Q38;
            Q38=makeQuery(id+"F4.opExtrude","SWEPT_BODY",BODY,{"disambiguationData":[OSD([sQuery(id+"F2.wireOp",EDGE,"E696.0.0"),sQuery(id+"F2.wireOp",EDGE,"E696.0.1"),sQuery(id+"F2.wireOp",EDGE,"E696.0.2"),sQuery(id+"F2.wireOp",EDGE,"E696.0.3"),sQuery(id+"F2.wireOp",EDGE,"E696.0.4"),sQuery(id+"F2.wireOp",EDGE,"E696.0.5"),sQuery(id+"F2.wireOp",EDGE,"E696.0.6"),sQuery(id+"F2.wireOp",EDGE,"E696.0.7"),sQuery(id+"F2.wireOp",EDGE,"E696.0.8"),sQuery(id+"F2.wireOp",EDGE,"E696.0.9")])]});
            var Q39;
            Q39=makeQuery(id+"F4.opExtrude","SWEPT_BODY",BODY,{"disambiguationData":[OSD([sQuery(id+"F2.wireOp",EDGE,"E707.0.0"),sQuery(id+"F2.wireOp",EDGE,"E707.0.1"),sQuery(id+"F2.wireOp",EDGE,"E707.0.2"),sQuery(id+"F2.wireOp",EDGE,"E707.0.3"),sQuery(id+"F2.wireOp",EDGE,"E707.0.4"),sQuery(id+"F2.wireOp",EDGE,"E707.0.5"),sQuery(id+"F2.wireOp",EDGE,"E707.0.6"),sQuery(id+"F2.wireOp",EDGE,"E707.0.7"),sQuery(id+"F2.wireOp",EDGE,"E707.0.8"),sQuery(id+"F2.wireOp",EDGE,"E707.0.9")])]});
            var Q40;
            Q40=makeQuery(id+"F4.opExtrude","SWEPT_BODY",BODY,{"disambiguationData":[OSD([sQuery(id+"F2.wireOp",EDGE,"E703.0.0"),sQuery(id+"F2.wireOp",EDGE,"E703.0.1"),sQuery(id+"F2.wireOp",EDGE,"E703.0.2"),sQuery(id+"F2.wireOp",EDGE,"E703.0.3"),sQuery(id+"F2.wireOp",EDGE,"E703.0.4"),sQuery(id+"F2.wireOp",EDGE,"E703.0.5"),sQuery(id+"F2.wireOp",EDGE,"E703.0.6"),sQuery(id+"F2.wireOp",EDGE,"E703.0.7"),sQuery(id+"F2.wireOp",EDGE,"E703.0.8"),sQuery(id+"F2.wireOp",EDGE,"E703.0.9")])]});
            var Q41;
            Q41=makeQuery(id+"F4.opExtrude","SWEPT_BODY",BODY,{"disambiguationData":[OSD([sQuery(id+"F2.wireOp",EDGE,"E704.0.0"),sQuery(id+"F2.wireOp",EDGE,"E704.0.1"),sQuery(id+"F2.wireOp",EDGE,"E704.0.2"),sQuery(id+"F2.wireOp",EDGE,"E704.0.3"),sQuery(id+"F2.wireOp",EDGE,"E704.0.4"),sQuery(id+"F2.wireOp",EDGE,"E704.0.5"),sQuery(id+"F2.wireOp",EDGE,"E704.0.6"),sQuery(id+"F2.wireOp",EDGE,"E704.0.7"),sQuery(id+"F2.wireOp",EDGE,"E704.0.8"),sQuery(id+"F2.wireOp",EDGE,"E704.0.9")])]});
            var Q42;
            Q42=makeQuery(id+"F4.opExtrude","SWEPT_BODY",BODY,{"disambiguationData":[OSD([sQuery(id+"F2.wireOp",EDGE,"E705.0.0"),sQuery(id+"F2.wireOp",EDGE,"E705.0.1"),sQuery(id+"F2.wireOp",EDGE,"E705.0.2"),sQuery(id+"F2.wireOp",EDGE,"E705.0.3"),sQuery(id+"F2.wireOp",EDGE,"E705.0.4"),sQuery(id+"F2.wireOp",EDGE,"E705.0.5"),sQuery(id+"F2.wireOp",EDGE,"E705.0.6"),sQuery(id+"F2.wireOp",EDGE,"E705.0.7"),sQuery(id+"F2.wireOp",EDGE,"E705.0.8"),sQuery(id+"F2.wireOp",EDGE,"E705.0.9")])]});
            var Q43;
            Q43=makeQuery(id+"F4.opExtrude","SWEPT_BODY",BODY,{"disambiguationData":[OSD([sQuery(id+"F2.wireOp",EDGE,"E698.0.0"),sQuery(id+"F2.wireOp",EDGE,"E698.0.1"),sQuery(id+"F2.wireOp",EDGE,"E698.0.2"),sQuery(id+"F2.wireOp",EDGE,"E698.0.3"),sQuery(id+"F2.wireOp",EDGE,"E698.0.4"),sQuery(id+"F2.wireOp",EDGE,"E698.0.5"),sQuery(id+"F2.wireOp",EDGE,"E698.0.6"),sQuery(id+"F2.wireOp",EDGE,"E698.0.7"),sQuery(id+"F2.wireOp",EDGE,"E698.0.8"),sQuery(id+"F2.wireOp",EDGE,"E698.0.9")])]});
            var Q44;
            Q44=makeQuery(id+"F4.opExtrude","SWEPT_BODY",BODY,{"disambiguationData":[OSD([sQuery(id+"F2.wireOp",EDGE,"E709.0.0"),sQuery(id+"F2.wireOp",EDGE,"E709.0.1"),sQuery(id+"F2.wireOp",EDGE,"E709.0.2"),sQuery(id+"F2.wireOp",EDGE,"E709.0.3"),sQuery(id+"F2.wireOp",EDGE,"E709.0.4"),sQuery(id+"F2.wireOp",EDGE,"E709.0.5"),sQuery(id+"F2.wireOp",EDGE,"E709.0.6"),sQuery(id+"F2.wireOp",EDGE,"E709.0.7"),sQuery(id+"F2.wireOp",EDGE,"E709.0.8"),sQuery(id+"F2.wireOp",EDGE,"E709.0.9")])]});
            var Q45;
            Q45=makeQuery(id+"F4.opExtrude","SWEPT_BODY",BODY,{"disambiguationData":[OSD([sQuery(id+"F2.wireOp",EDGE,"E708.0.0"),sQuery(id+"F2.wireOp",EDGE,"E708.0.1"),sQuery(id+"F2.wireOp",EDGE,"E708.0.2"),sQuery(id+"F2.wireOp",EDGE,"E708.0.3"),sQuery(id+"F2.wireOp",EDGE,"E708.0.4"),sQuery(id+"F2.wireOp",EDGE,"E708.0.5"),sQuery(id+"F2.wireOp",EDGE,"E708.0.6"),sQuery(id+"F2.wireOp",EDGE,"E708.0.7"),sQuery(id+"F2.wireOp",EDGE,"E708.0.8"),sQuery(id+"F2.wireOp",EDGE,"E708.0.9")])]});
            var Q46;
            Q46=makeQuery(id+"F4.opExtrude","SWEPT_BODY",BODY,{"disambiguationData":[OSD([sQuery(id+"F2.wireOp",EDGE,"E697.0.0"),sQuery(id+"F2.wireOp",EDGE,"E697.0.1"),sQuery(id+"F2.wireOp",EDGE,"E697.0.2"),sQuery(id+"F2.wireOp",EDGE,"E697.0.3"),sQuery(id+"F2.wireOp",EDGE,"E697.0.4"),sQuery(id+"F2.wireOp",EDGE,"E697.0.5"),sQuery(id+"F2.wireOp",EDGE,"E697.0.6"),sQuery(id+"F2.wireOp",EDGE,"E697.0.7"),sQuery(id+"F2.wireOp",EDGE,"E697.0.8"),sQuery(id+"F2.wireOp",EDGE,"E697.0.9")])]});
            var Q47;
            Q47=makeQuery(id+"F4.opExtrude","SWEPT_BODY",BODY,{"disambiguationData":[OSD([sQuery(id+"F2.wireOp",EDGE,"E693.0.0"),sQuery(id+"F2.wireOp",EDGE,"E693.0.1"),sQuery(id+"F2.wireOp",EDGE,"E693.0.2"),sQuery(id+"F2.wireOp",EDGE,"E693.0.3"),sQuery(id+"F2.wireOp",EDGE,"E693.0.4"),sQuery(id+"F2.wireOp",EDGE,"E693.0.5"),sQuery(id+"F2.wireOp",EDGE,"E693.0.6"),sQuery(id+"F2.wireOp",EDGE,"E693.0.7"),sQuery(id+"F2.wireOp",EDGE,"E693.0.8"),sQuery(id+"F2.wireOp",EDGE,"E693.0.9")])]});
            var Q48;
            Q48=makeQuery(id+"F4.opExtrude","SWEPT_BODY",BODY,{"disambiguationData":[OSD([sQuery(id+"F2.wireOp",EDGE,"E689.0.0"),sQuery(id+"F2.wireOp",EDGE,"E689.0.1"),sQuery(id+"F2.wireOp",EDGE,"E689.0.2"),sQuery(id+"F2.wireOp",EDGE,"E689.0.3"),sQuery(id+"F2.wireOp",EDGE,"E689.0.4"),sQuery(id+"F2.wireOp",EDGE,"E689.0.5"),sQuery(id+"F2.wireOp",EDGE,"E689.0.6"),sQuery(id+"F2.wireOp",EDGE,"E689.0.7"),sQuery(id+"F2.wireOp",EDGE,"E689.0.8"),sQuery(id+"F2.wireOp",EDGE,"E689.0.9")])]});
            var Q49;
            Q49=makeQuery(id+"F4.opExtrude","SWEPT_BODY",BODY,{"disambiguationData":[OSD([sQuery(id+"F2.wireOp",EDGE,"E702.0.0"),sQuery(id+"F2.wireOp",EDGE,"E702.0.1"),sQuery(id+"F2.wireOp",EDGE,"E702.0.2"),sQuery(id+"F2.wireOp",EDGE,"E702.0.3"),sQuery(id+"F2.wireOp",EDGE,"E702.0.4"),sQuery(id+"F2.wireOp",EDGE,"E702.0.5"),sQuery(id+"F2.wireOp",EDGE,"E702.0.6"),sQuery(id+"F2.wireOp",EDGE,"E702.0.7"),sQuery(id+"F2.wireOp",EDGE,"E702.0.8"),sQuery(id+"F2.wireOp",EDGE,"E702.0.9")])]});
            var Q50;
            Q50=makeQuery(id+"F3.opExtrude","SWEPT_BODY",BODY,{"disambiguationData":[OSD([sQuery(id+"F0.wireOp",EDGE,"E27"),sQuery(id+"F0.wireOp",EDGE,"E28"),sQuery(id+"F0.wireOp",EDGE,"E34"),sQuery(id+"F0.wireOp",EDGE,"E39")])]});
            var Q51;
            Q51=makeQuery(id+"F3.opExtrude","SWEPT_BODY",BODY,{"disambiguationData":[OSD([sQuery(id+"F0.wireOp",EDGE,"E31"),sQuery(id+"F0.wireOp",EDGE,"E36"),sQuery(id+"F0.wireOp",EDGE,"E41")])]});
            var Q52;
            Q52=makeQuery(id+"F3.opExtrude","SWEPT_BODY",BODY,{"disambiguationData":[OSD([sQuery(id+"F0.wireOp",EDGE,"E29"),sQuery(id+"F0.wireOp",EDGE,"E30"),sQuery(id+"F0.wireOp",EDGE,"E35"),sQuery(id+"F0.wireOp",EDGE,"E40")])]});
            var Q53;
            Q53=makeQuery(id+"F3.opExtrude","SWEPT_BODY",BODY,{"disambiguationData":[OSD([sQuery(id+"F0.wireOp",EDGE,"E25"),sQuery(id+"F0.wireOp",EDGE,"E26"),sQuery(id+"F0.wireOp",EDGE,"E33"),sQuery(id+"F0.wireOp",EDGE,"E38")])]});
            var Q54;
            Q54=makeQuery(id+"F3.opExtrude","SWEPT_BODY",BODY,{"disambiguationData":[OSD([sQuery(id+"F0.wireOp",EDGE,"E23"),sQuery(id+"F0.wireOp",EDGE,"E24"),sQuery(id+"F0.wireOp",EDGE,"E32"),sQuery(id+"F0.wireOp",EDGE,"E37")])]});
            var Q55;
            Q55=makeQuery(id+"F3.opExtrude","SWEPT_BODY",BODY,{"disambiguationData":[OSD([sQuery(id+"F0.wireOp",EDGE,"E4"),sQuery(id+"F0.wireOp",EDGE,"E5"),sQuery(id+"F0.wireOp",EDGE,"E13"),sQuery(id+"F0.wireOp",EDGE,"E18")])]});
            var Q56;
            Q56=makeQuery(id+"F3.opExtrude","SWEPT_BODY",BODY,{"disambiguationData":[OSD([sQuery(id+"F0.wireOp",EDGE,"E6"),sQuery(id+"F0.wireOp",EDGE,"E7"),sQuery(id+"F0.wireOp",EDGE,"E14"),sQuery(id+"F0.wireOp",EDGE,"E19")])]});
            var Q57;
            Q57=makeQuery(id+"F3.opExtrude","SWEPT_BODY",BODY,{"disambiguationData":[OSD([sQuery(id+"F0.wireOp",EDGE,"E8"),sQuery(id+"F0.wireOp",EDGE,"E9"),sQuery(id+"F0.wireOp",EDGE,"E15"),sQuery(id+"F0.wireOp",EDGE,"E20")])]});
            var Q58;
            Q58=makeQuery(id+"F3.opExtrude","SWEPT_BODY",BODY,{"disambiguationData":[OSD([sQuery(id+"F0.wireOp",EDGE,"E10"),sQuery(id+"F0.wireOp",EDGE,"E11"),sQuery(id+"F0.wireOp",EDGE,"E16"),sQuery(id+"F0.wireOp",EDGE,"E21")])]});
            var Q59;
            Q59=makeQuery(id+"F3.opExtrude","SWEPT_BODY",BODY,{"disambiguationData":[OSD([sQuery(id+"F0.wireOp",EDGE,"E12"),sQuery(id+"F0.wireOp",EDGE,"E17"),sQuery(id+"F0.wireOp",EDGE,"E22")])]});
            booleanBodies(context, id + "F6", {"operationType" : BooleanOperationType.SUBTRACTION, "tools" : qUnion([Q0, Q1, Q2, Q3, Q4, Q5, Q6, Q7, Q8, Q9, Q10, Q11, Q12, Q13, Q14, Q15, Q16, Q17, Q18, Q19, Q20, Q21, Q22, Q23, Q24, Q25, Q26, Q27, Q28, Q29, Q30, Q31, Q32, Q33, Q34, Q35, Q36, Q37, Q38, Q39, Q40, Q41, Q42, Q43, Q44, Q45, Q46, Q47, Q48, Q49]), "targets" : qUnion([Q50, Q51, Q52, Q53, Q54, Q55, Q56, Q57, Q58, Q59])});
        }
    });
